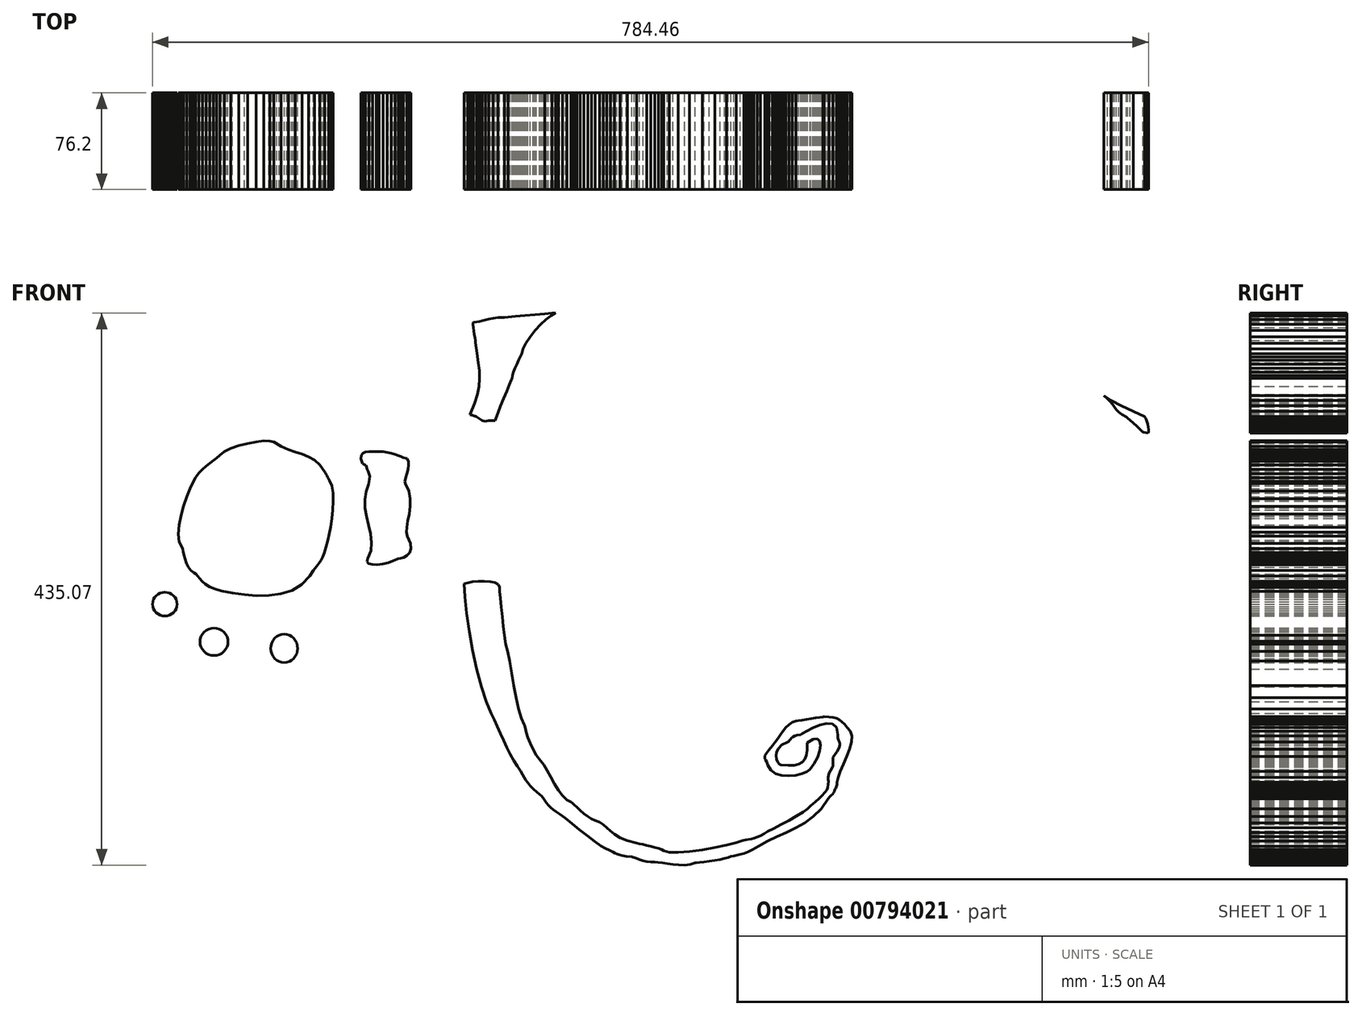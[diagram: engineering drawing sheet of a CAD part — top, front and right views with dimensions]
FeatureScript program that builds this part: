
annotation { "Feature Type Name" : "Feature", "Feature Type Description" : "" }
export const myFeature = defineFeature(function(context is Context, id is Id, definition is map)
    precondition{}
    {
        {
            var Q0;
            Q0=qCreatedBy(makeId("Front.planeOp"),FACE);
            var sketch = newSketch(context, id + "F0", { "sketchPlane" : qUnion([Q0])});
            skLineSegment(sketch, "E0", {"start": v(-208.35, -37.14) * mm, "end": v(-209.4, -40.75) * mm});
            skLineSegment(sketch, "E1", {"start": v(-209.4, -40.75) * mm, "end": v(-211.93, -45.37) * mm});
            skLineSegment(sketch, "E2", {"start": v(-211.93, -45.37) * mm, "end": v(-215.55, -50.61) * mm});
            skLineSegment(sketch, "E3", {"start": v(-215.55, -50.61) * mm, "end": v(-219.86, -56.1) * mm});
            skLineSegment(sketch, "E4", {"start": v(-219.86, -56.1) * mm, "end": v(-224.45, -61.4) * mm});
            skLineSegment(sketch, "E5", {"start": v(-224.45, -61.4) * mm, "end": v(-228.92, -66.17) * mm});
            skLineSegment(sketch, "E6", {"start": v(-228.92, -66.17) * mm, "end": v(-232.89, -69.99) * mm});
            skLineSegment(sketch, "E7", {"start": v(-232.89, -69.99) * mm, "end": v(-235.95, -72.46) * mm});
            skLineSegment(sketch, "E8", {"start": v(-235.95, -72.46) * mm, "end": v(-243.86, -77.98) * mm});
            skLineSegment(sketch, "E9", {"start": v(-243.86, -77.98) * mm, "end": v(-251.56, -83.5) * mm});
            skLineSegment(sketch, "E10", {"start": v(-251.56, -83.5) * mm, "end": v(-259.2, -88.85) * mm});
            skLineSegment(sketch, "E11", {"start": v(-259.2, -88.85) * mm, "end": v(-266.91, -93.92) * mm});
            skLineSegment(sketch, "E12", {"start": v(-266.91, -93.92) * mm, "end": v(-274.89, -98.55) * mm});
            skLineSegment(sketch, "E13", {"start": v(-274.89, -98.55) * mm, "end": v(-283.27, -102.63) * mm});
            skLineSegment(sketch, "E14", {"start": v(-283.27, -102.63) * mm, "end": v(-292.21, -106) * mm});
            skLineSegment(sketch, "E15", {"start": v(-292.21, -106) * mm, "end": v(-301.88, -108.52) * mm});
            skLineSegment(sketch, "E16", {"start": v(-301.88, -108.52) * mm, "end": v(-307.2, -109.6) * mm});
            skLineSegment(sketch, "E17", {"start": v(-307.2, -109.6) * mm, "end": v(-312.55, -110.63) * mm});
            skLineSegment(sketch, "E18", {"start": v(-312.55, -110.63) * mm, "end": v(-317.94, -111.58) * mm});
            skLineSegment(sketch, "E19", {"start": v(-317.94, -111.58) * mm, "end": v(-323.38, -112.42) * mm});
            skLineSegment(sketch, "E20", {"start": v(-323.38, -112.42) * mm, "end": v(-328.86, -113.1) * mm});
            skLineSegment(sketch, "E21", {"start": v(-328.86, -113.1) * mm, "end": v(-334.38, -113.56) * mm});
            skLineSegment(sketch, "E22", {"start": v(-334.38, -113.56) * mm, "end": v(-339.94, -113.79) * mm});
            skLineSegment(sketch, "E23", {"start": v(-339.94, -113.79) * mm, "end": v(-345.54, -113.72) * mm});
            skLineSegment(sketch, "E24", {"start": v(-345.54, -113.72) * mm, "end": v(-350.27, -113.48) * mm});
            skLineSegment(sketch, "E25", {"start": v(-350.27, -113.48) * mm, "end": v(-353.56, -113.18) * mm});
            skLineSegment(sketch, "E26", {"start": v(-353.56, -113.18) * mm, "end": v(-355.78, -112.84) * mm});
            skLineSegment(sketch, "E27", {"start": v(-355.78, -112.84) * mm, "end": v(-357.32, -112.47) * mm});
            skLineSegment(sketch, "E28", {"start": v(-357.32, -112.47) * mm, "end": v(-358.56, -112.08) * mm});
            skLineSegment(sketch, "E29", {"start": v(-358.56, -112.08) * mm, "end": v(-359.89, -111.67) * mm});
            skLineSegment(sketch, "E30", {"start": v(-359.89, -111.67) * mm, "end": v(-361.68, -111.27) * mm});
            skLineSegment(sketch, "E31", {"start": v(-361.68, -111.27) * mm, "end": v(-364.33, -110.87) * mm});
            skLineSegment(sketch, "E32", {"start": v(-364.33, -110.87) * mm, "end": v(-370.95, -109.7) * mm});
            skLineSegment(sketch, "E33", {"start": v(-370.95, -109.7) * mm, "end": v(-378.12, -107.85) * mm});
            skLineSegment(sketch, "E34", {"start": v(-378.12, -107.85) * mm, "end": v(-385.58, -105.38) * mm});
            skLineSegment(sketch, "E35", {"start": v(-385.58, -105.38) * mm, "end": v(-393.1, -102.4) * mm});
            skLineSegment(sketch, "E36", {"start": v(-393.1, -102.4) * mm, "end": v(-400.45, -99.03) * mm});
            skLineSegment(sketch, "E37", {"start": v(-400.45, -99.03) * mm, "end": v(-407.36, -95.36) * mm});
            skLineSegment(sketch, "E38", {"start": v(-407.36, -95.36) * mm, "end": v(-413.61, -91.48) * mm});
            skLineSegment(sketch, "E39", {"start": v(-413.61, -91.48) * mm, "end": v(-418.95, -87.5) * mm});
            skLineSegment(sketch, "E40", {"start": v(-418.95, -87.5) * mm, "end": v(-420.34, -86.72) * mm});
            skLineSegment(sketch, "E41", {"start": v(-420.34, -86.72) * mm, "end": v(-421.81, -86.45) * mm});
            skLineSegment(sketch, "E42", {"start": v(-421.81, -86.45) * mm, "end": v(-423.56, -86.22) * mm});
            skLineSegment(sketch, "E43", {"start": v(-423.56, -86.22) * mm, "end": v(-425.77, -85.58) * mm});
            skLineSegment(sketch, "E44", {"start": v(-425.77, -85.58) * mm, "end": v(-428.66, -84.05) * mm});
            skLineSegment(sketch, "E45", {"start": v(-428.66, -84.05) * mm, "end": v(-432.42, -81.17) * mm});
            skLineSegment(sketch, "E46", {"start": v(-432.42, -81.17) * mm, "end": v(-437.25, -76.48) * mm});
            skLineSegment(sketch, "E47", {"start": v(-437.25, -76.48) * mm, "end": v(-443.34, -69.52) * mm});
            skLineSegment(sketch, "E48", {"start": v(-443.34, -69.52) * mm, "end": v(-446.37, -65.99) * mm});
            skLineSegment(sketch, "E49", {"start": v(-446.37, -65.99) * mm, "end": v(-449.48, -62.55) * mm});
            skLineSegment(sketch, "E50", {"start": v(-449.48, -62.55) * mm, "end": v(-452.63, -59.14) * mm});
            skLineSegment(sketch, "E51", {"start": v(-452.63, -59.14) * mm, "end": v(-455.78, -55.7) * mm});
            skLineSegment(sketch, "E52", {"start": v(-455.78, -55.7) * mm, "end": v(-458.87, -52.18) * mm});
            skLineSegment(sketch, "E53", {"start": v(-458.87, -52.18) * mm, "end": v(-461.86, -48.5) * mm});
            skLineSegment(sketch, "E54", {"start": v(-461.86, -48.5) * mm, "end": v(-464.7, -44.6) * mm});
            skLineSegment(sketch, "E55", {"start": v(-464.7, -44.6) * mm, "end": v(-467.34, -40.43) * mm});
            skLineSegment(sketch, "E56", {"start": v(-467.34, -40.43) * mm, "end": v(-471.05, -34.4) * mm});
            skLineSegment(sketch, "E57", {"start": v(-471.05, -34.4) * mm, "end": v(-474.16, -29.72) * mm});
            skLineSegment(sketch, "E58", {"start": v(-474.16, -29.72) * mm, "end": v(-476.73, -25.85) * mm});
            skLineSegment(sketch, "E59", {"start": v(-476.73, -25.85) * mm, "end": v(-478.83, -22.2) * mm});
            skLineSegment(sketch, "E60", {"start": v(-478.83, -22.2) * mm, "end": v(-480.55, -18.2) * mm});
            skLineSegment(sketch, "E61", {"start": v(-480.55, -18.2) * mm, "end": v(-481.95, -13.26) * mm});
            skLineSegment(sketch, "E62", {"start": v(-481.95, -13.26) * mm, "end": v(-483.1, -6.8) * mm});
            skLineSegment(sketch, "E63", {"start": v(-483.1, -6.8) * mm, "end": v(-484.1, 1.73) * mm});
            skLineSegment(sketch, "E64", {"start": v(-484.1, 1.73) * mm, "end": v(-484.63, 4.71) * mm});
            skLineSegment(sketch, "E65", {"start": v(-484.63, 4.71) * mm, "end": v(-485.63, 8.34) * mm});
            skLineSegment(sketch, "E66", {"start": v(-485.63, 8.34) * mm, "end": v(-486.93, 12.53) * mm});
            skLineSegment(sketch, "E67", {"start": v(-486.93, 12.53) * mm, "end": v(-488.36, 17.21) * mm});
            skLineSegment(sketch, "E68", {"start": v(-488.36, 17.21) * mm, "end": v(-489.76, 22.29) * mm});
            skLineSegment(sketch, "E69", {"start": v(-489.76, 22.29) * mm, "end": v(-490.96, 27.69) * mm});
            skLineSegment(sketch, "E70", {"start": v(-490.96, 27.69) * mm, "end": v(-491.8, 33.33) * mm});
            skLineSegment(sketch, "E71", {"start": v(-491.8, 33.33) * mm, "end": v(-492.12, 39.13) * mm});
            skLineSegment(sketch, "E72", {"start": v(-492.12, 39.13) * mm, "end": v(-492.1, 43.83) * mm});
            skLineSegment(sketch, "E73", {"start": v(-492.1, 43.83) * mm, "end": v(-491.96, 49.13) * mm});
            skLineSegment(sketch, "E74", {"start": v(-491.96, 49.13) * mm, "end": v(-491.67, 54.8) * mm});
            skLineSegment(sketch, "E75", {"start": v(-491.67, 54.8) * mm, "end": v(-491.16, 60.58) * mm});
            skLineSegment(sketch, "E76", {"start": v(-491.16, 60.58) * mm, "end": v(-490.37, 66.27) * mm});
            skLineSegment(sketch, "E77", {"start": v(-490.37, 66.27) * mm, "end": v(-489.23, 71.63) * mm});
            skLineSegment(sketch, "E78", {"start": v(-489.23, 71.63) * mm, "end": v(-487.68, 76.43) * mm});
            skLineSegment(sketch, "E79", {"start": v(-487.68, 76.43) * mm, "end": v(-485.66, 80.43) * mm});
            skLineSegment(sketch, "E80", {"start": v(-485.66, 80.43) * mm, "end": v(-484, 84.07) * mm});
            skLineSegment(sketch, "E81", {"start": v(-484, 84.07) * mm, "end": v(-482.62, 88.9) * mm});
            skLineSegment(sketch, "E82", {"start": v(-482.62, 88.9) * mm, "end": v(-481.28, 94.53) * mm});
            skLineSegment(sketch, "E83", {"start": v(-481.28, 94.53) * mm, "end": v(-479.78, 100.6) * mm});
            skLineSegment(sketch, "E84", {"start": v(-479.78, 100.6) * mm, "end": v(-477.88, 106.75) * mm});
            skLineSegment(sketch, "E85", {"start": v(-477.88, 106.75) * mm, "end": v(-475.38, 112.57) * mm});
            skLineSegment(sketch, "E86", {"start": v(-475.38, 112.57) * mm, "end": v(-472.04, 117.7) * mm});
            skLineSegment(sketch, "E87", {"start": v(-472.04, 117.7) * mm, "end": v(-467.65, 121.78) * mm});
            skLineSegment(sketch, "E88", {"start": v(-467.65, 121.78) * mm, "end": v(-466.26, 123.27) * mm});
            skLineSegment(sketch, "E89", {"start": v(-466.26, 123.27) * mm, "end": v(-464.7, 125.77) * mm});
            skLineSegment(sketch, "E90", {"start": v(-464.7, 125.77) * mm, "end": v(-462.86, 129.05) * mm});
            skLineSegment(sketch, "E91", {"start": v(-462.86, 129.05) * mm, "end": v(-460.63, 132.87) * mm});
            skLineSegment(sketch, "E92", {"start": v(-460.63, 132.87) * mm, "end": v(-457.91, 137.02) * mm});
            skLineSegment(sketch, "E93", {"start": v(-457.91, 137.02) * mm, "end": v(-454.6, 141.25) * mm});
            skLineSegment(sketch, "E94", {"start": v(-454.6, 141.25) * mm, "end": v(-450.57, 145.34) * mm});
            skLineSegment(sketch, "E95", {"start": v(-450.57, 145.34) * mm, "end": v(-445.73, 149.07) * mm});
            skLineSegment(sketch, "E96", {"start": v(-445.73, 149.07) * mm, "end": v(-442.4, 151.6) * mm});
            skLineSegment(sketch, "E97", {"start": v(-442.4, 151.6) * mm, "end": v(-438.2, 155.26) * mm});
            skLineSegment(sketch, "E98", {"start": v(-438.2, 155.26) * mm, "end": v(-433.33, 159.6) * mm});
            skLineSegment(sketch, "E99", {"start": v(-433.33, 159.6) * mm, "end": v(-428.08, 164.2) * mm});
            skLineSegment(sketch, "E100", {"start": v(-428.08, 164.2) * mm, "end": v(-422.67, 168.63) * mm});
            skLineSegment(sketch, "E101", {"start": v(-422.67, 168.63) * mm, "end": v(-417.35, 172.46) * mm});
            skLineSegment(sketch, "E102", {"start": v(-417.35, 172.46) * mm, "end": v(-412.37, 175.25) * mm});
            skLineSegment(sketch, "E103", {"start": v(-412.37, 175.25) * mm, "end": v(-407.98, 176.59) * mm});
            skLineSegment(sketch, "E104", {"start": v(-407.98, 176.59) * mm, "end": v(-407.04, 176.9) * mm});
            skLineSegment(sketch, "E105", {"start": v(-407.04, 176.9) * mm, "end": v(-405.7, 177.63) * mm});
            skLineSegment(sketch, "E106", {"start": v(-405.7, 177.63) * mm, "end": v(-404.1, 178.65) * mm});
            skLineSegment(sketch, "E107", {"start": v(-404.1, 178.65) * mm, "end": v(-402.42, 179.84) * mm});
            skLineSegment(sketch, "E108", {"start": v(-402.42, 179.84) * mm, "end": v(-400.79, 181.1) * mm});
            skLineSegment(sketch, "E109", {"start": v(-400.79, 181.1) * mm, "end": v(-399.35, 182.32) * mm});
            skLineSegment(sketch, "E110", {"start": v(-399.35, 182.32) * mm, "end": v(-398.27, 183.37) * mm});
            skLineSegment(sketch, "E111", {"start": v(-398.27, 183.37) * mm, "end": v(-397.69, 184.15) * mm});
            skLineSegment(sketch, "E112", {"start": v(-397.69, 184.15) * mm, "end": v(-397.28, 184.12) * mm});
            skLineSegment(sketch, "E113", {"start": v(-397.28, 184.12) * mm, "end": v(-396.96, 184.1) * mm});
            skLineSegment(sketch, "E114", {"start": v(-396.96, 184.1) * mm, "end": v(-396.82, 184.1) * mm});
            skLineSegment(sketch, "E115", {"start": v(-396.82, 184.1) * mm, "end": v(-396.68, 184.13) * mm});
            skLineSegment(sketch, "E116", {"start": v(-396.68, 184.13) * mm, "end": v(-396.54, 184.18) * mm});
            skLineSegment(sketch, "E117", {"start": v(-396.54, 184.18) * mm, "end": v(-396.4, 184.27) * mm});
            skLineSegment(sketch, "E118", {"start": v(-396.4, 184.27) * mm, "end": v(-392.15, 186.6) * mm});
            skLineSegment(sketch, "E119", {"start": v(-392.15, 186.6) * mm, "end": v(-387.6, 188.05) * mm});
            skLineSegment(sketch, "E120", {"start": v(-387.6, 188.05) * mm, "end": v(-382.84, 188.9) * mm});
            skLineSegment(sketch, "E121", {"start": v(-382.84, 188.9) * mm, "end": v(-378, 189.41) * mm});
            skLineSegment(sketch, "E122", {"start": v(-378, 189.41) * mm, "end": v(-373.21, 189.91) * mm});
            skLineSegment(sketch, "E123", {"start": v(-373.21, 189.91) * mm, "end": v(-368.57, 190.67) * mm});
            skLineSegment(sketch, "E124", {"start": v(-368.57, 190.67) * mm, "end": v(-364.2, 191.98) * mm});
            skLineSegment(sketch, "E125", {"start": v(-364.2, 191.98) * mm, "end": v(-360.22, 194.13) * mm});
            skLineSegment(sketch, "E126", {"start": v(-360.22, 194.13) * mm, "end": v(-357.32, 195.4) * mm});
            skLineSegment(sketch, "E127", {"start": v(-357.32, 195.4) * mm, "end": v(-353.37, 196.1) * mm});
            skLineSegment(sketch, "E128", {"start": v(-353.37, 196.1) * mm, "end": v(-348.73, 196.36) * mm});
            skLineSegment(sketch, "E129", {"start": v(-348.73, 196.36) * mm, "end": v(-343.75, 196.3) * mm});
            skLineSegment(sketch, "E130", {"start": v(-343.75, 196.3) * mm, "end": v(-338.8, 196.04) * mm});
            skLineSegment(sketch, "E131", {"start": v(-338.8, 196.04) * mm, "end": v(-334.23, 195.72) * mm});
            skLineSegment(sketch, "E132", {"start": v(-334.23, 195.72) * mm, "end": v(-330.4, 195.47) * mm});
            skLineSegment(sketch, "E133", {"start": v(-330.4, 195.47) * mm, "end": v(-327.68, 195.42) * mm});
            skLineSegment(sketch, "E134", {"start": v(-327.68, 195.42) * mm, "end": v(-322.8, 195.26) * mm});
            skLineSegment(sketch, "E135", {"start": v(-322.8, 195.26) * mm, "end": v(-317.16, 194.53) * mm});
            skLineSegment(sketch, "E136", {"start": v(-317.16, 194.53) * mm, "end": v(-311.19, 193.4) * mm});
            skLineSegment(sketch, "E137", {"start": v(-311.19, 193.4) * mm, "end": v(-305.32, 192.08) * mm});
            skLineSegment(sketch, "E138", {"start": v(-305.32, 192.08) * mm, "end": v(-299.98, 190.73) * mm});
            skLineSegment(sketch, "E139", {"start": v(-299.98, 190.73) * mm, "end": v(-295.6, 189.54) * mm});
            skLineSegment(sketch, "E140", {"start": v(-295.6, 189.54) * mm, "end": v(-292.64, 188.7) * mm});
            skLineSegment(sketch, "E141", {"start": v(-292.64, 188.7) * mm, "end": v(-291.5, 188.37) * mm});
            skLineSegment(sketch, "E142", {"start": v(-291.5, 188.37) * mm, "end": v(-288.2, 188.12) * mm});
            skLineSegment(sketch, "E143", {"start": v(-288.2, 188.12) * mm, "end": v(-284.6, 187.19) * mm});
            skLineSegment(sketch, "E144", {"start": v(-284.6, 187.19) * mm, "end": v(-280.81, 185.77) * mm});
            skLineSegment(sketch, "E145", {"start": v(-280.81, 185.77) * mm, "end": v(-276.94, 184.04) * mm});
            skLineSegment(sketch, "E146", {"start": v(-276.94, 184.04) * mm, "end": v(-273.1, 182.17) * mm});
            skLineSegment(sketch, "E147", {"start": v(-273.1, 182.17) * mm, "end": v(-269.41, 180.34) * mm});
            skLineSegment(sketch, "E148", {"start": v(-269.41, 180.34) * mm, "end": v(-265.98, 178.72) * mm});
            skLineSegment(sketch, "E149", {"start": v(-265.98, 178.72) * mm, "end": v(-262.93, 177.49) * mm});
            skLineSegment(sketch, "E150", {"start": v(-262.93, 177.49) * mm, "end": v(-262.03, 176.24) * mm});
            skLineSegment(sketch, "E151", {"start": v(-262.03, 176.24) * mm, "end": v(-259.93, 174.4) * mm});
            skLineSegment(sketch, "E152", {"start": v(-259.93, 174.4) * mm, "end": v(-257, 172.17) * mm});
            skLineSegment(sketch, "E153", {"start": v(-257, 172.17) * mm, "end": v(-253.61, 169.8) * mm});
            skLineSegment(sketch, "E154", {"start": v(-253.61, 169.8) * mm, "end": v(-250.12, 167.5) * mm});
            skLineSegment(sketch, "E155", {"start": v(-250.12, 167.5) * mm, "end": v(-246.89, 165.53) * mm});
            skLineSegment(sketch, "E156", {"start": v(-246.89, 165.53) * mm, "end": v(-244.29, 164.1) * mm});
            skLineSegment(sketch, "E157", {"start": v(-244.29, 164.1) * mm, "end": v(-242.68, 163.43) * mm});
            skLineSegment(sketch, "E158", {"start": v(-242.68, 163.43) * mm, "end": v(-239.6, 161.8) * mm});
            skLineSegment(sketch, "E159", {"start": v(-239.6, 161.8) * mm, "end": v(-235.25, 158.26) * mm});
            skLineSegment(sketch, "E160", {"start": v(-235.25, 158.26) * mm, "end": v(-230.13, 153.46) * mm});
            skLineSegment(sketch, "E161", {"start": v(-230.13, 153.46) * mm, "end": v(-224.7, 148.03) * mm});
            skLineSegment(sketch, "E162", {"start": v(-224.7, 148.03) * mm, "end": v(-219.48, 142.62) * mm});
            skLineSegment(sketch, "E163", {"start": v(-219.48, 142.62) * mm, "end": v(-214.92, 137.88) * mm});
            skLineSegment(sketch, "E164", {"start": v(-214.92, 137.88) * mm, "end": v(-211.52, 134.43) * mm});
            skLineSegment(sketch, "E165", {"start": v(-211.52, 134.43) * mm, "end": v(-209.76, 132.93) * mm});
            skLineSegment(sketch, "E166", {"start": v(-209.76, 132.93) * mm, "end": v(-206.84, 132.26) * mm});
            skLineSegment(sketch, "E167", {"start": v(-206.84, 132.26) * mm, "end": v(-204.6, 133.15) * mm});
            skLineSegment(sketch, "E168", {"start": v(-204.6, 133.15) * mm, "end": v(-202.9, 135.25) * mm});
            skLineSegment(sketch, "E169", {"start": v(-202.9, 135.25) * mm, "end": v(-201.58, 138.19) * mm});
            skLineSegment(sketch, "E170", {"start": v(-201.58, 138.19) * mm, "end": v(-200.52, 141.61) * mm});
            skLineSegment(sketch, "E171", {"start": v(-200.52, 141.61) * mm, "end": v(-199.56, 145.17) * mm});
            skLineSegment(sketch, "E172", {"start": v(-199.56, 145.17) * mm, "end": v(-198.56, 148.5) * mm});
            skLineSegment(sketch, "E173", {"start": v(-198.56, 148.5) * mm, "end": v(-197.38, 151.26) * mm});
            skLineSegment(sketch, "E174", {"start": v(-197.38, 151.26) * mm, "end": v(-195.83, 155.22) * mm});
            skLineSegment(sketch, "E175", {"start": v(-195.83, 155.22) * mm, "end": v(-194.87, 160.31) * mm});
            skLineSegment(sketch, "E176", {"start": v(-194.87, 160.31) * mm, "end": v(-194.47, 166.12) * mm});
            skLineSegment(sketch, "E177", {"start": v(-194.47, 166.12) * mm, "end": v(-194.63, 172.25) * mm});
            skLineSegment(sketch, "E178", {"start": v(-194.63, 172.25) * mm, "end": v(-195.34, 178.29) * mm});
            skLineSegment(sketch, "E179", {"start": v(-195.34, 178.29) * mm, "end": v(-196.59, 183.83) * mm});
            skLineSegment(sketch, "E180", {"start": v(-196.59, 183.83) * mm, "end": v(-198.37, 188.48) * mm});
            skLineSegment(sketch, "E181", {"start": v(-198.37, 188.48) * mm, "end": v(-200.67, 191.82) * mm});
            skLineSegment(sketch, "E182", {"start": v(-200.67, 191.82) * mm, "end": v(-203.2, 194.14) * mm});
            skLineSegment(sketch, "E183", {"start": v(-203.2, 194.14) * mm, "end": v(-206.46, 196.97) * mm});
            skLineSegment(sketch, "E184", {"start": v(-206.46, 196.97) * mm, "end": v(-209.95, 200.1) * mm});
            skLineSegment(sketch, "E185", {"start": v(-209.95, 200.1) * mm, "end": v(-213.15, 203.36) * mm});
            skLineSegment(sketch, "E186", {"start": v(-213.15, 203.36) * mm, "end": v(-215.57, 206.55) * mm});
            skLineSegment(sketch, "E187", {"start": v(-215.57, 206.55) * mm, "end": v(-216.7, 209.49) * mm});
            skLineSegment(sketch, "E188", {"start": v(-216.7, 209.49) * mm, "end": v(-216.06, 211.97) * mm});
            skLineSegment(sketch, "E189", {"start": v(-216.06, 211.97) * mm, "end": v(-213.12, 213.83) * mm});
            skLineSegment(sketch, "E190", {"start": v(-213.12, 213.83) * mm, "end": v(-209.96, 215.34) * mm});
            skLineSegment(sketch, "E191", {"start": v(-209.96, 215.34) * mm, "end": v(-202.14, 216.57) * mm});
            skLineSegment(sketch, "E192", {"start": v(-202.14, 216.57) * mm, "end": v(-191.16, 217.6) * mm});
            skLineSegment(sketch, "E193", {"start": v(-191.16, 217.6) * mm, "end": v(-178.53, 218.51) * mm});
            skLineSegment(sketch, "E194", {"start": v(-178.53, 218.51) * mm, "end": v(-165.72, 219.37) * mm});
            skLineSegment(sketch, "E195", {"start": v(-165.72, 219.37) * mm, "end": v(-154.22, 220.26) * mm});
            skLineSegment(sketch, "E196", {"start": v(-154.22, 220.26) * mm, "end": v(-145.54, 221.25) * mm});
            skLineSegment(sketch, "E197", {"start": v(-145.54, 221.25) * mm, "end": v(-141.16, 222.43) * mm});
            skLineSegment(sketch, "E198", {"start": v(-141.16, 222.43) * mm, "end": v(-137.78, 223.77) * mm});
            skLineSegment(sketch, "E199", {"start": v(-137.78, 223.77) * mm, "end": v(-131.88, 224.98) * mm});
            skLineSegment(sketch, "E200", {"start": v(-131.88, 224.98) * mm, "end": v(-124.22, 226.12) * mm});
            skLineSegment(sketch, "E201", {"start": v(-124.22, 226.12) * mm, "end": v(-115.53, 227.22) * mm});
            skLineSegment(sketch, "E202", {"start": v(-115.53, 227.22) * mm, "end": v(-106.55, 228.34) * mm});
            skLineSegment(sketch, "E203", {"start": v(-106.55, 228.34) * mm, "end": v(-98.01, 229.5) * mm});
            skLineSegment(sketch, "E204", {"start": v(-98.01, 229.5) * mm, "end": v(-90.67, 230.78) * mm});
            skLineSegment(sketch, "E205", {"start": v(-90.67, 230.78) * mm, "end": v(-85.25, 232.19) * mm});
            skLineSegment(sketch, "E206", {"start": v(-85.25, 232.19) * mm, "end": v(-81.66, 233.2) * mm});
            skLineSegment(sketch, "E207", {"start": v(-81.66, 233.2) * mm, "end": v(-75.46, 234.69) * mm});
            skLineSegment(sketch, "E208", {"start": v(-75.46, 234.69) * mm, "end": v(-67.62, 236.36) * mm});
            skLineSegment(sketch, "E209", {"start": v(-67.62, 236.36) * mm, "end": v(-59.07, 237.98) * mm});
            skLineSegment(sketch, "E210", {"start": v(-59.07, 237.98) * mm, "end": v(-50.78, 239.28) * mm});
            skLineSegment(sketch, "E211", {"start": v(-50.78, 239.28) * mm, "end": v(-43.68, 240) * mm});
            skLineSegment(sketch, "E212", {"start": v(-43.68, 240) * mm, "end": v(-38.72, 239.87) * mm});
            skLineSegment(sketch, "E213", {"start": v(-38.72, 239.87) * mm, "end": v(-36.86, 238.65) * mm});
            skLineSegment(sketch, "E214", {"start": v(-36.86, 238.65) * mm, "end": v(-37.05, 235.1) * mm});
            skLineSegment(sketch, "E215", {"start": v(-37.05, 235.1) * mm, "end": v(-37.65, 232.95) * mm});
            skLineSegment(sketch, "E216", {"start": v(-37.65, 232.95) * mm, "end": v(-38.68, 231.73) * mm});
            skLineSegment(sketch, "E217", {"start": v(-38.68, 231.73) * mm, "end": v(-40.17, 231) * mm});
            skLineSegment(sketch, "E218", {"start": v(-40.17, 231) * mm, "end": v(-42.15, 230.3) * mm});
            skLineSegment(sketch, "E219", {"start": v(-42.15, 230.3) * mm, "end": v(-44.64, 229.2) * mm});
            skLineSegment(sketch, "E220", {"start": v(-44.64, 229.2) * mm, "end": v(-47.67, 227.21) * mm});
            skLineSegment(sketch, "E221", {"start": v(-47.67, 227.21) * mm, "end": v(-51.26, 223.92) * mm});
            skLineSegment(sketch, "E222", {"start": v(-51.26, 223.92) * mm, "end": v(-55.17, 220.71) * mm});
            skLineSegment(sketch, "E223", {"start": v(-55.17, 220.71) * mm, "end": v(-60.25, 217.76) * mm});
            skLineSegment(sketch, "E224", {"start": v(-60.25, 217.76) * mm, "end": v(-66.1, 215) * mm});
            skLineSegment(sketch, "E225", {"start": v(-66.1, 215) * mm, "end": v(-72.28, 212.33) * mm});
            skLineSegment(sketch, "E226", {"start": v(-72.28, 212.33) * mm, "end": v(-78.42, 209.7) * mm});
            skLineSegment(sketch, "E227", {"start": v(-78.42, 209.7) * mm, "end": v(-84.1, 207.01) * mm});
            skLineSegment(sketch, "E228", {"start": v(-84.1, 207.01) * mm, "end": v(-88.9, 204.2) * mm});
            skLineSegment(sketch, "E229", {"start": v(-88.9, 204.2) * mm, "end": v(-92.42, 201.18) * mm});
            skLineSegment(sketch, "E230", {"start": v(-92.42, 201.18) * mm, "end": v(-95.18, 198.51) * mm});
            skLineSegment(sketch, "E231", {"start": v(-95.18, 198.51) * mm, "end": v(-98.28, 196.21) * mm});
            skLineSegment(sketch, "E232", {"start": v(-98.28, 196.21) * mm, "end": v(-101.68, 194) * mm});
            skLineSegment(sketch, "E233", {"start": v(-101.68, 194) * mm, "end": v(-105.31, 191.64) * mm});
            skLineSegment(sketch, "E234", {"start": v(-105.31, 191.64) * mm, "end": v(-109.12, 188.84) * mm});
            skLineSegment(sketch, "E235", {"start": v(-109.12, 188.84) * mm, "end": v(-113.06, 185.34) * mm});
            skLineSegment(sketch, "E236", {"start": v(-113.06, 185.34) * mm, "end": v(-117.06, 180.9) * mm});
            skLineSegment(sketch, "E237", {"start": v(-117.06, 180.9) * mm, "end": v(-121.08, 175.22) * mm});
            skLineSegment(sketch, "E238", {"start": v(-121.08, 175.22) * mm, "end": v(-123.48, 171.6) * mm});
            skLineSegment(sketch, "E239", {"start": v(-123.48, 171.6) * mm, "end": v(-125.98, 168.05) * mm});
            skLineSegment(sketch, "E240", {"start": v(-125.98, 168.05) * mm, "end": v(-128.46, 164.5) * mm});
            skLineSegment(sketch, "E241", {"start": v(-128.46, 164.5) * mm, "end": v(-130.82, 160.87) * mm});
            skLineSegment(sketch, "E242", {"start": v(-130.82, 160.87) * mm, "end": v(-132.96, 157.05) * mm});
            skLineSegment(sketch, "E243", {"start": v(-132.96, 157.05) * mm, "end": v(-134.75, 152.98) * mm});
            skLineSegment(sketch, "E244", {"start": v(-134.75, 152.98) * mm, "end": v(-136.1, 148.55) * mm});
            skLineSegment(sketch, "E245", {"start": v(-136.1, 148.55) * mm, "end": v(-136.9, 143.7) * mm});
            skLineSegment(sketch, "E246", {"start": v(-136.9, 143.7) * mm, "end": v(-137.12, 143.45) * mm});
            skLineSegment(sketch, "E247", {"start": v(-137.12, 143.45) * mm, "end": v(-137.73, 142.78) * mm});
            skLineSegment(sketch, "E248", {"start": v(-137.73, 142.78) * mm, "end": v(-138.58, 141.78) * mm});
            skLineSegment(sketch, "E249", {"start": v(-138.58, 141.78) * mm, "end": v(-139.56, 140.5) * mm});
            skLineSegment(sketch, "E250", {"start": v(-139.56, 140.5) * mm, "end": v(-140.52, 139.05) * mm});
            skLineSegment(sketch, "E251", {"start": v(-140.52, 139.05) * mm, "end": v(-141.35, 137.5) * mm});
            skLineSegment(sketch, "E252", {"start": v(-141.35, 137.5) * mm, "end": v(-141.92, 135.9) * mm});
            skLineSegment(sketch, "E253", {"start": v(-141.92, 135.9) * mm, "end": v(-142.1, 134.34) * mm});
            skLineSegment(sketch, "E254", {"start": v(-142.1, 134.34) * mm, "end": v(-142.36, 130.26) * mm});
            skLineSegment(sketch, "E255", {"start": v(-142.36, 130.26) * mm, "end": v(-143.18, 126.12) * mm});
            skLineSegment(sketch, "E256", {"start": v(-143.18, 126.12) * mm, "end": v(-144.16, 122) * mm});
            skLineSegment(sketch, "E257", {"start": v(-144.16, 122) * mm, "end": v(-144.93, 117.97) * mm});
            skLineSegment(sketch, "E258", {"start": v(-144.93, 117.97) * mm, "end": v(-145.07, 114.13) * mm});
            skLineSegment(sketch, "E259", {"start": v(-145.07, 114.13) * mm, "end": v(-144.2, 110.53) * mm});
            skLineSegment(sketch, "E260", {"start": v(-144.2, 110.53) * mm, "end": v(-141.92, 107.28) * mm});
            skLineSegment(sketch, "E261", {"start": v(-141.92, 107.28) * mm, "end": v(-137.83, 104.44) * mm});
            skLineSegment(sketch, "E262", {"start": v(-137.83, 104.44) * mm, "end": v(-137.13, 103.9) * mm});
            skLineSegment(sketch, "E263", {"start": v(-137.13, 103.9) * mm, "end": v(-136.78, 103.32) * mm});
            skLineSegment(sketch, "E264", {"start": v(-136.78, 103.32) * mm, "end": v(-136.48, 102.66) * mm});
            skLineSegment(sketch, "E265", {"start": v(-136.48, 102.66) * mm, "end": v(-135.93, 101.93) * mm});
            skLineSegment(sketch, "E266", {"start": v(-135.93, 101.93) * mm, "end": v(-134.82, 101.12) * mm});
            skLineSegment(sketch, "E267", {"start": v(-134.82, 101.12) * mm, "end": v(-132.85, 100.24) * mm});
            skLineSegment(sketch, "E268", {"start": v(-132.85, 100.24) * mm, "end": v(-129.73, 99.27) * mm});
            skLineSegment(sketch, "E269", {"start": v(-129.73, 99.27) * mm, "end": v(-125.15, 98.2) * mm});
            skLineSegment(sketch, "E270", {"start": v(-125.15, 98.2) * mm, "end": v(-124.24, 98.04) * mm});
            skLineSegment(sketch, "E271", {"start": v(-124.24, 98.04) * mm, "end": v(-122.97, 97.84) * mm});
            skLineSegment(sketch, "E272", {"start": v(-122.97, 97.84) * mm, "end": v(-121.5, 97.62) * mm});
            skLineSegment(sketch, "E273", {"start": v(-121.5, 97.62) * mm, "end": v(-119.96, 97.39) * mm});
            skLineSegment(sketch, "E274", {"start": v(-119.96, 97.39) * mm, "end": v(-118.47, 97.17) * mm});
            skLineSegment(sketch, "E275", {"start": v(-118.47, 97.17) * mm, "end": v(-117.2, 96.98) * mm});
            skLineSegment(sketch, "E276", {"start": v(-117.2, 96.98) * mm, "end": v(-116.25, 96.84) * mm});
            skLineSegment(sketch, "E277", {"start": v(-116.25, 96.84) * mm, "end": v(-115.79, 96.76) * mm});
            skLineSegment(sketch, "E278", {"start": v(-182.98, 129.65) * mm, "end": v(-179.53, 137.98) * mm});
            skLineSegment(sketch, "E279", {"start": v(-179.53, 137.98) * mm, "end": v(-177.27, 145.15) * mm});
            skLineSegment(sketch, "E280", {"start": v(-177.27, 145.15) * mm, "end": v(-176.03, 151.55) * mm});
            skLineSegment(sketch, "E281", {"start": v(-176.03, 151.55) * mm, "end": v(-175.63, 157.58) * mm});
            skLineSegment(sketch, "E282", {"start": v(-175.63, 157.58) * mm, "end": v(-175.88, 163.64) * mm});
            skLineSegment(sketch, "E283", {"start": v(-175.88, 163.64) * mm, "end": v(-176.61, 170.13) * mm});
            skLineSegment(sketch, "E284", {"start": v(-176.61, 170.13) * mm, "end": v(-177.64, 177.46) * mm});
            skLineSegment(sketch, "E285", {"start": v(-177.64, 177.46) * mm, "end": v(-178.79, 186.02) * mm});
            skLineSegment(sketch, "E286", {"start": v(-178.79, 186.02) * mm, "end": v(-179, 187.58) * mm});
            skLineSegment(sketch, "E287", {"start": v(-179, 187.58) * mm, "end": v(-179.35, 189.8) * mm});
            skLineSegment(sketch, "E288", {"start": v(-179.35, 189.8) * mm, "end": v(-179.76, 192.41) * mm});
            skLineSegment(sketch, "E289", {"start": v(-179.76, 192.41) * mm, "end": v(-180.17, 195.15) * mm});
            skLineSegment(sketch, "E290", {"start": v(-180.17, 195.15) * mm, "end": v(-180.52, 197.75) * mm});
            skLineSegment(sketch, "E291", {"start": v(-180.52, 197.75) * mm, "end": v(-180.75, 199.93) * mm});
            skLineSegment(sketch, "E292", {"start": v(-180.75, 199.93) * mm, "end": v(-180.8, 201.44) * mm});
            skLineSegment(sketch, "E293", {"start": v(-180.8, 201.44) * mm, "end": v(-180.63, 202) * mm});
            skLineSegment(sketch, "E294", {"start": v(-180.63, 202) * mm, "end": v(-178.02, 202.16) * mm});
            skLineSegment(sketch, "E295", {"start": v(-178.02, 202.16) * mm, "end": v(-175.69, 202.59) * mm});
            skLineSegment(sketch, "E296", {"start": v(-175.69, 202.59) * mm, "end": v(-173.43, 203.19) * mm});
            skLineSegment(sketch, "E297", {"start": v(-173.43, 203.19) * mm, "end": v(-171.04, 203.88) * mm});
            skLineSegment(sketch, "E298", {"start": v(-171.04, 203.88) * mm, "end": v(-168.33, 204.57) * mm});
            skLineSegment(sketch, "E299", {"start": v(-168.33, 204.57) * mm, "end": v(-165.08, 205.17) * mm});
            skLineSegment(sketch, "E300", {"start": v(-165.08, 205.17) * mm, "end": v(-161.1, 205.6) * mm});
            skLineSegment(sketch, "E301", {"start": v(-161.1, 205.6) * mm, "end": v(-156.2, 205.76) * mm});
            skLineSegment(sketch, "E302", {"start": v(-156.2, 205.76) * mm, "end": v(-153.2, 205.97) * mm});
            skLineSegment(sketch, "E303", {"start": v(-153.2, 205.97) * mm, "end": v(-147.4, 206.51) * mm});
            skLineSegment(sketch, "E304", {"start": v(-147.4, 206.51) * mm, "end": v(-139.93, 207.24) * mm});
            skLineSegment(sketch, "E305", {"start": v(-139.93, 207.24) * mm, "end": v(-131.9, 208) * mm});
            skLineSegment(sketch, "E306", {"start": v(-131.9, 208) * mm, "end": v(-124.45, 208.66) * mm});
            skLineSegment(sketch, "E307", {"start": v(-124.45, 208.66) * mm, "end": v(-118.7, 209.08) * mm});
            skLineSegment(sketch, "E308", {"start": v(-118.7, 209.08) * mm, "end": v(-115.76, 209.1) * mm});
            skLineSegment(sketch, "E309", {"start": v(-115.76, 209.1) * mm, "end": v(-116.77, 208.58) * mm});
            skLineSegment(sketch, "E310", {"start": v(-116.77, 208.58) * mm, "end": v(-119.65, 207.13) * mm});
            skLineSegment(sketch, "E311", {"start": v(-119.65, 207.13) * mm, "end": v(-123.38, 204.2) * mm});
            skLineSegment(sketch, "E312", {"start": v(-123.38, 204.2) * mm, "end": v(-127.57, 200.17) * mm});
            skLineSegment(sketch, "E313", {"start": v(-127.57, 200.17) * mm, "end": v(-131.86, 195.44) * mm});
            skLineSegment(sketch, "E314", {"start": v(-131.86, 195.44) * mm, "end": v(-135.87, 190.38) * mm});
            skLineSegment(sketch, "E315", {"start": v(-135.87, 190.38) * mm, "end": v(-139.23, 185.38) * mm});
            skLineSegment(sketch, "E316", {"start": v(-139.23, 185.38) * mm, "end": v(-141.58, 180.83) * mm});
            skLineSegment(sketch, "E317", {"start": v(-141.58, 180.83) * mm, "end": v(-142.53, 177.1) * mm});
            skLineSegment(sketch, "E318", {"start": v(-142.53, 177.1) * mm, "end": v(-142.86, 176.42) * mm});
            skLineSegment(sketch, "E319", {"start": v(-142.86, 176.42) * mm, "end": v(-143.74, 174.64) * mm});
            skLineSegment(sketch, "E320", {"start": v(-143.74, 174.64) * mm, "end": v(-144.97, 172.08) * mm});
            skLineSegment(sketch, "E321", {"start": v(-144.97, 172.08) * mm, "end": v(-146.37, 169.02) * mm});
            skLineSegment(sketch, "E322", {"start": v(-146.37, 169.02) * mm, "end": v(-147.77, 165.76) * mm});
            skLineSegment(sketch, "E323", {"start": v(-147.77, 165.76) * mm, "end": v(-148.98, 162.62) * mm});
            skLineSegment(sketch, "E324", {"start": v(-148.98, 162.62) * mm, "end": v(-149.81, 159.87) * mm});
            skLineSegment(sketch, "E325", {"start": v(-149.81, 159.87) * mm, "end": v(-150.09, 157.84) * mm});
            skLineSegment(sketch, "E326", {"start": v(-150.09, 157.84) * mm, "end": v(-150.65, 156.44) * mm});
            skLineSegment(sketch, "E327", {"start": v(-150.65, 156.44) * mm, "end": v(-152.14, 152.82) * mm});
            skLineSegment(sketch, "E328", {"start": v(-152.14, 152.82) * mm, "end": v(-154.25, 147.7) * mm});
            skLineSegment(sketch, "E329", {"start": v(-154.25, 147.7) * mm, "end": v(-156.66, 141.79) * mm});
            skLineSegment(sketch, "E330", {"start": v(-156.66, 141.79) * mm, "end": v(-159.08, 135.8) * mm});
            skLineSegment(sketch, "E331", {"start": v(-159.08, 135.8) * mm, "end": v(-161.19, 130.44) * mm});
            skLineSegment(sketch, "E332", {"start": v(-161.19, 130.44) * mm, "end": v(-162.68, 126.43) * mm});
            skLineSegment(sketch, "E333", {"start": v(-162.68, 126.43) * mm, "end": v(-163.24, 124.48) * mm});
            skLineSegment(sketch, "E334", {"start": v(-163.24, 124.48) * mm, "end": v(-166.31, 124.57) * mm});
            skLineSegment(sketch, "E335", {"start": v(-166.31, 124.57) * mm, "end": v(-168.43, 124.39) * mm});
            skLineSegment(sketch, "E336", {"start": v(-168.43, 124.39) * mm, "end": v(-169.92, 124.11) * mm});
            skLineSegment(sketch, "E337", {"start": v(-169.92, 124.11) * mm, "end": v(-171.06, 123.93) * mm});
            skLineSegment(sketch, "E338", {"start": v(-171.06, 123.93) * mm, "end": v(-172.18, 124) * mm});
            skLineSegment(sketch, "E339", {"start": v(-172.18, 124) * mm, "end": v(-173.57, 124.53) * mm});
            skLineSegment(sketch, "E340", {"start": v(-173.57, 124.53) * mm, "end": v(-175.54, 125.69) * mm});
            skLineSegment(sketch, "E341", {"start": v(-175.54, 125.69) * mm, "end": v(-178.4, 127.65) * mm});
            skLineSegment(sketch, "E342", {"start": v(-178.4, 127.65) * mm, "end": v(-178.8, 127.83) * mm});
            skLineSegment(sketch, "E343", {"start": v(-178.8, 127.83) * mm, "end": v(-179.44, 128.03) * mm});
            skLineSegment(sketch, "E344", {"start": v(-179.44, 128.03) * mm, "end": v(-180.24, 128.25) * mm});
            skLineSegment(sketch, "E345", {"start": v(-180.24, 128.25) * mm, "end": v(-181.08, 128.49) * mm});
            skLineSegment(sketch, "E346", {"start": v(-181.08, 128.49) * mm, "end": v(-181.87, 128.75) * mm});
            skLineSegment(sketch, "E347", {"start": v(-181.87, 128.75) * mm, "end": v(-182.52, 129.03) * mm});
            skLineSegment(sketch, "E348", {"start": v(-182.52, 129.03) * mm, "end": v(-182.92, 129.33) * mm});
            skLineSegment(sketch, "E349", {"start": v(-182.92, 129.33) * mm, "end": v(-182.98, 129.65) * mm});
            skLineSegment(sketch, "E350", {"start": v(-297.61, 84.07) * mm, "end": v(-301.34, 89.4) * mm});
            skLineSegment(sketch, "E351", {"start": v(-301.34, 89.4) * mm, "end": v(-305.6, 93.22) * mm});
            skLineSegment(sketch, "E352", {"start": v(-305.6, 93.22) * mm, "end": v(-310.32, 95.94) * mm});
            skLineSegment(sketch, "E353", {"start": v(-310.32, 95.94) * mm, "end": v(-315.4, 97.96) * mm});
            skLineSegment(sketch, "E354", {"start": v(-315.4, 97.96) * mm, "end": v(-320.77, 99.7) * mm});
            skLineSegment(sketch, "E355", {"start": v(-320.77, 99.7) * mm, "end": v(-326.33, 101.6) * mm});
            skLineSegment(sketch, "E356", {"start": v(-326.33, 101.6) * mm, "end": v(-332, 104.04) * mm});
            skLineSegment(sketch, "E357", {"start": v(-332, 104.04) * mm, "end": v(-337.67, 107.44) * mm});
            skLineSegment(sketch, "E358", {"start": v(-337.67, 107.44) * mm, "end": v(-340.72, 108.36) * mm});
            skLineSegment(sketch, "E359", {"start": v(-340.72, 108.36) * mm, "end": v(-345.59, 108.42) * mm});
            skLineSegment(sketch, "E360", {"start": v(-345.59, 108.42) * mm, "end": v(-351.69, 107.74) * mm});
            skLineSegment(sketch, "E361", {"start": v(-351.69, 107.74) * mm, "end": v(-358.44, 106.43) * mm});
            skLineSegment(sketch, "E362", {"start": v(-358.44, 106.43) * mm, "end": v(-365.26, 104.61) * mm});
            skLineSegment(sketch, "E363", {"start": v(-365.26, 104.61) * mm, "end": v(-371.57, 102.4) * mm});
            skLineSegment(sketch, "E364", {"start": v(-371.57, 102.4) * mm, "end": v(-376.78, 99.9) * mm});
            skLineSegment(sketch, "E365", {"start": v(-376.78, 99.9) * mm, "end": v(-380.3, 97.23) * mm});
            skLineSegment(sketch, "E366", {"start": v(-380.3, 97.23) * mm, "end": v(-382.66, 94.97) * mm});
            skLineSegment(sketch, "E367", {"start": v(-382.66, 94.97) * mm, "end": v(-385.32, 92.86) * mm});
            skLineSegment(sketch, "E368", {"start": v(-385.32, 92.86) * mm, "end": v(-388.18, 90.76) * mm});
            skLineSegment(sketch, "E369", {"start": v(-388.18, 90.76) * mm, "end": v(-391.12, 88.53) * mm});
            skLineSegment(sketch, "E370", {"start": v(-391.12, 88.53) * mm, "end": v(-394.04, 86.03) * mm});
            skLineSegment(sketch, "E371", {"start": v(-394.04, 86.03) * mm, "end": v(-396.83, 83.14) * mm});
            skLineSegment(sketch, "E372", {"start": v(-396.83, 83.14) * mm, "end": v(-399.39, 79.71) * mm});
            skLineSegment(sketch, "E373", {"start": v(-399.39, 79.71) * mm, "end": v(-401.6, 75.62) * mm});
            skLineSegment(sketch, "E374", {"start": v(-401.6, 75.62) * mm, "end": v(-403.73, 70.68) * mm});
            skLineSegment(sketch, "E375", {"start": v(-403.73, 70.68) * mm, "end": v(-406.2, 64.4) * mm});
            skLineSegment(sketch, "E376", {"start": v(-406.2, 64.4) * mm, "end": v(-408.66, 57.25) * mm});
            skLineSegment(sketch, "E377", {"start": v(-408.66, 57.25) * mm, "end": v(-410.82, 49.66) * mm});
            skLineSegment(sketch, "E378", {"start": v(-410.82, 49.66) * mm, "end": v(-412.34, 42.09) * mm});
            skLineSegment(sketch, "E379", {"start": v(-412.34, 42.09) * mm, "end": v(-412.9, 34.98) * mm});
            skLineSegment(sketch, "E380", {"start": v(-412.9, 34.98) * mm, "end": v(-412.18, 28.8) * mm});
            skLineSegment(sketch, "E381", {"start": v(-412.18, 28.8) * mm, "end": v(-409.86, 23.97) * mm});
            skLineSegment(sketch, "E382", {"start": v(-409.86, 23.97) * mm, "end": v(-409.57, 23.05) * mm});
            skLineSegment(sketch, "E383", {"start": v(-409.57, 23.05) * mm, "end": v(-409.15, 21.09) * mm});
            skLineSegment(sketch, "E384", {"start": v(-409.15, 21.09) * mm, "end": v(-408.54, 18.4) * mm});
            skLineSegment(sketch, "E385", {"start": v(-408.54, 18.4) * mm, "end": v(-407.69, 15.27) * mm});
            skLineSegment(sketch, "E386", {"start": v(-407.69, 15.27) * mm, "end": v(-406.52, 12) * mm});
            skLineSegment(sketch, "E387", {"start": v(-406.52, 12) * mm, "end": v(-404.97, 8.9) * mm});
            skLineSegment(sketch, "E388", {"start": v(-404.97, 8.9) * mm, "end": v(-402.97, 6.25) * mm});
            skLineSegment(sketch, "E389", {"start": v(-402.97, 6.25) * mm, "end": v(-400.46, 4.36) * mm});
            skLineSegment(sketch, "E390", {"start": v(-400.46, 4.36) * mm, "end": v(-399.1, 3.33) * mm});
            skLineSegment(sketch, "E391", {"start": v(-399.1, 3.33) * mm, "end": v(-397.7, 1.78) * mm});
            skLineSegment(sketch, "E392", {"start": v(-397.7, 1.78) * mm, "end": v(-396.1, -0.14) * mm});
            skLineSegment(sketch, "E393", {"start": v(-396.1, -0.14) * mm, "end": v(-394.12, -2.27) * mm});
            skLineSegment(sketch, "E394", {"start": v(-394.12, -2.27) * mm, "end": v(-391.6, -4.46) * mm});
            skLineSegment(sketch, "E395", {"start": v(-391.6, -4.46) * mm, "end": v(-388.32, -6.55) * mm});
            skLineSegment(sketch, "E396", {"start": v(-388.32, -6.55) * mm, "end": v(-384.13, -8.4) * mm});
            skLineSegment(sketch, "E397", {"start": v(-384.13, -8.4) * mm, "end": v(-378.85, -9.85) * mm});
            skLineSegment(sketch, "E398", {"start": v(-378.85, -9.85) * mm, "end": v(-370.32, -11.46) * mm});
            skLineSegment(sketch, "E399", {"start": v(-370.32, -11.46) * mm, "end": v(-361.01, -12.81) * mm});
            skLineSegment(sketch, "E400", {"start": v(-361.01, -12.81) * mm, "end": v(-351.31, -13.6) * mm});
            skLineSegment(sketch, "E401", {"start": v(-351.31, -13.6) * mm, "end": v(-341.57, -13.5) * mm});
            skLineSegment(sketch, "E402", {"start": v(-341.57, -13.5) * mm, "end": v(-332.15, -12.2) * mm});
            skLineSegment(sketch, "E403", {"start": v(-332.15, -12.2) * mm, "end": v(-323.43, -9.42) * mm});
            skLineSegment(sketch, "E404", {"start": v(-323.43, -9.42) * mm, "end": v(-315.75, -4.82) * mm});
            skLineSegment(sketch, "E405", {"start": v(-315.75, -4.82) * mm, "end": v(-309.48, 1.9) * mm});
            skLineSegment(sketch, "E406", {"start": v(-309.48, 1.9) * mm, "end": v(-306.44, 6.16) * mm});
            skLineSegment(sketch, "E407", {"start": v(-306.44, 6.16) * mm, "end": v(-304.06, 9.36) * mm});
            skLineSegment(sketch, "E408", {"start": v(-304.06, 9.36) * mm, "end": v(-302.19, 11.9) * mm});
            skLineSegment(sketch, "E409", {"start": v(-302.19, 11.9) * mm, "end": v(-300.67, 14.24) * mm});
            skLineSegment(sketch, "E410", {"start": v(-300.67, 14.24) * mm, "end": v(-299.37, 16.8) * mm});
            skLineSegment(sketch, "E411", {"start": v(-299.37, 16.8) * mm, "end": v(-298.14, 20) * mm});
            skLineSegment(sketch, "E412", {"start": v(-298.14, 20) * mm, "end": v(-296.82, 24.26) * mm});
            skLineSegment(sketch, "E413", {"start": v(-296.82, 24.26) * mm, "end": v(-295.26, 30.04) * mm});
            skLineSegment(sketch, "E414", {"start": v(-295.26, 30.04) * mm, "end": v(-294.18, 34.7) * mm});
            skLineSegment(sketch, "E415", {"start": v(-294.18, 34.7) * mm, "end": v(-293.04, 40.53) * mm});
            skLineSegment(sketch, "E416", {"start": v(-293.04, 40.53) * mm, "end": v(-292.01, 47.12) * mm});
            skLineSegment(sketch, "E417", {"start": v(-292.01, 47.12) * mm, "end": v(-291.24, 54.05) * mm});
            skLineSegment(sketch, "E418", {"start": v(-291.24, 54.05) * mm, "end": v(-290.88, 60.93) * mm});
            skLineSegment(sketch, "E419", {"start": v(-290.88, 60.93) * mm, "end": v(-291.07, 67.34) * mm});
            skLineSegment(sketch, "E420", {"start": v(-291.07, 67.34) * mm, "end": v(-291.97, 72.88) * mm});
            skLineSegment(sketch, "E421", {"start": v(-291.97, 72.88) * mm, "end": v(-293.73, 77.15) * mm});
            skLineSegment(sketch, "E422", {"start": v(-293.73, 77.15) * mm, "end": v(-294.02, 77.62) * mm});
            skLineSegment(sketch, "E423", {"start": v(-294.02, 77.62) * mm, "end": v(-294.4, 78.28) * mm});
            skLineSegment(sketch, "E424", {"start": v(-294.4, 78.28) * mm, "end": v(-294.86, 79.08) * mm});
            skLineSegment(sketch, "E425", {"start": v(-294.86, 79.08) * mm, "end": v(-295.37, 80) * mm});
            skLineSegment(sketch, "E426", {"start": v(-295.37, 80) * mm, "end": v(-295.92, 81) * mm});
            skLineSegment(sketch, "E427", {"start": v(-295.92, 81) * mm, "end": v(-296.5, 82.03) * mm});
            skLineSegment(sketch, "E428", {"start": v(-296.5, 82.03) * mm, "end": v(-297.06, 83.07) * mm});
            skLineSegment(sketch, "E429", {"start": v(-297.06, 83.07) * mm, "end": v(-297.61, 84.07) * mm});
            skLineSegment(sketch, "E430", {"start": v(-265.2, 93) * mm, "end": v(-264.93, 89.11) * mm});
            skLineSegment(sketch, "E431", {"start": v(-264.93, 89.11) * mm, "end": v(-264.27, 86.41) * mm});
            skLineSegment(sketch, "E432", {"start": v(-264.27, 86.41) * mm, "end": v(-263.45, 84.42) * mm});
            skLineSegment(sketch, "E433", {"start": v(-263.45, 84.42) * mm, "end": v(-262.7, 82.67) * mm});
            skLineSegment(sketch, "E434", {"start": v(-262.7, 82.67) * mm, "end": v(-262.23, 80.68) * mm});
            skLineSegment(sketch, "E435", {"start": v(-262.23, 80.68) * mm, "end": v(-262.28, 77.99) * mm});
            skLineSegment(sketch, "E436", {"start": v(-262.28, 77.99) * mm, "end": v(-263.08, 74.1) * mm});
            skLineSegment(sketch, "E437", {"start": v(-263.08, 74.1) * mm, "end": v(-264.85, 68.57) * mm});
            skLineSegment(sketch, "E438", {"start": v(-264.85, 68.57) * mm, "end": v(-266.08, 62.28) * mm});
            skLineSegment(sketch, "E439", {"start": v(-266.08, 62.28) * mm, "end": v(-265.8, 55.67) * mm});
            skLineSegment(sketch, "E440", {"start": v(-265.8, 55.67) * mm, "end": v(-264.59, 48.85) * mm});
            skLineSegment(sketch, "E441", {"start": v(-264.59, 48.85) * mm, "end": v(-262.97, 41.95) * mm});
            skLineSegment(sketch, "E442", {"start": v(-262.97, 41.95) * mm, "end": v(-261.52, 35.07) * mm});
            skLineSegment(sketch, "E443", {"start": v(-261.52, 35.07) * mm, "end": v(-260.78, 28.35) * mm});
            skLineSegment(sketch, "E444", {"start": v(-260.78, 28.35) * mm, "end": v(-261.31, 21.9) * mm});
            skLineSegment(sketch, "E445", {"start": v(-261.31, 21.9) * mm, "end": v(-263.66, 15.83) * mm});
            skLineSegment(sketch, "E446", {"start": v(-263.66, 15.83) * mm, "end": v(-264.3, 13.3) * mm});
            skLineSegment(sketch, "E447", {"start": v(-264.3, 13.3) * mm, "end": v(-262.95, 11.73) * mm});
            skLineSegment(sketch, "E448", {"start": v(-262.95, 11.73) * mm, "end": v(-260.1, 10.97) * mm});
            skLineSegment(sketch, "E449", {"start": v(-260.1, 10.97) * mm, "end": v(-256.25, 10.92) * mm});
            skLineSegment(sketch, "E450", {"start": v(-256.25, 10.92) * mm, "end": v(-251.88, 11.45) * mm});
            skLineSegment(sketch, "E451", {"start": v(-251.88, 11.45) * mm, "end": v(-247.5, 12.45) * mm});
            skLineSegment(sketch, "E452", {"start": v(-247.5, 12.45) * mm, "end": v(-243.59, 13.8) * mm});
            skLineSegment(sketch, "E453", {"start": v(-243.59, 13.8) * mm, "end": v(-240.64, 15.36) * mm});
            skLineSegment(sketch, "E454", {"start": v(-240.64, 15.36) * mm, "end": v(-239.86, 15.44) * mm});
            skLineSegment(sketch, "E455", {"start": v(-239.86, 15.44) * mm, "end": v(-237.93, 15.79) * mm});
            skLineSegment(sketch, "E456", {"start": v(-237.93, 15.79) * mm, "end": v(-235.4, 16.57) * mm});
            skLineSegment(sketch, "E457", {"start": v(-235.4, 16.57) * mm, "end": v(-232.8, 17.97) * mm});
            skLineSegment(sketch, "E458", {"start": v(-232.8, 17.97) * mm, "end": v(-230.68, 20.17) * mm});
            skLineSegment(sketch, "E459", {"start": v(-230.68, 20.17) * mm, "end": v(-229.6, 23.37) * mm});
            skLineSegment(sketch, "E460", {"start": v(-229.6, 23.37) * mm, "end": v(-230.07, 27.73) * mm});
            skLineSegment(sketch, "E461", {"start": v(-230.07, 27.73) * mm, "end": v(-232.66, 33.45) * mm});
            skLineSegment(sketch, "E462", {"start": v(-232.66, 33.45) * mm, "end": v(-233.36, 36.37) * mm});
            skLineSegment(sketch, "E463", {"start": v(-233.36, 36.37) * mm, "end": v(-233.05, 40.38) * mm});
            skLineSegment(sketch, "E464", {"start": v(-233.05, 40.38) * mm, "end": v(-232.15, 45.26) * mm});
            skLineSegment(sketch, "E465", {"start": v(-232.15, 45.26) * mm, "end": v(-231.1, 50.78) * mm});
            skLineSegment(sketch, "E466", {"start": v(-231.1, 50.78) * mm, "end": v(-230.33, 56.72) * mm});
            skLineSegment(sketch, "E467", {"start": v(-230.33, 56.72) * mm, "end": v(-230.28, 62.85) * mm});
            skLineSegment(sketch, "E468", {"start": v(-230.28, 62.85) * mm, "end": v(-231.38, 68.95) * mm});
            skLineSegment(sketch, "E469", {"start": v(-231.38, 68.95) * mm, "end": v(-234.07, 74.8) * mm});
            skLineSegment(sketch, "E470", {"start": v(-234.07, 74.8) * mm, "end": v(-234.34, 76.6) * mm});
            skLineSegment(sketch, "E471", {"start": v(-234.34, 76.6) * mm, "end": v(-233.85, 79.31) * mm});
            skLineSegment(sketch, "E472", {"start": v(-233.85, 79.31) * mm, "end": v(-232.97, 82.6) * mm});
            skLineSegment(sketch, "E473", {"start": v(-232.97, 82.6) * mm, "end": v(-232.07, 86.12) * mm});
            skLineSegment(sketch, "E474", {"start": v(-232.07, 86.12) * mm, "end": v(-231.53, 89.5) * mm});
            skLineSegment(sketch, "E475", {"start": v(-231.53, 89.5) * mm, "end": v(-231.72, 92.4) * mm});
            skLineSegment(sketch, "E476", {"start": v(-231.72, 92.4) * mm, "end": v(-233.01, 94.45) * mm});
            skLineSegment(sketch, "E477", {"start": v(-233.01, 94.45) * mm, "end": v(-235.78, 95.3) * mm});
            skLineSegment(sketch, "E478", {"start": v(-235.78, 95.3) * mm, "end": v(-236.28, 95.53) * mm});
            skLineSegment(sketch, "E479", {"start": v(-236.28, 95.53) * mm, "end": v(-237.63, 96.1) * mm});
            skLineSegment(sketch, "E480", {"start": v(-237.63, 96.1) * mm, "end": v(-239.66, 96.9) * mm});
            skLineSegment(sketch, "E481", {"start": v(-239.66, 96.9) * mm, "end": v(-242.23, 97.8) * mm});
            skLineSegment(sketch, "E482", {"start": v(-242.23, 97.8) * mm, "end": v(-245.19, 98.7) * mm});
            skLineSegment(sketch, "E483", {"start": v(-245.19, 98.7) * mm, "end": v(-248.38, 99.44) * mm});
            skLineSegment(sketch, "E484", {"start": v(-248.38, 99.44) * mm, "end": v(-251.65, 99.94) * mm});
            skLineSegment(sketch, "E485", {"start": v(-251.65, 99.94) * mm, "end": v(-254.86, 100.05) * mm});
            skLineSegment(sketch, "E486", {"start": v(-254.86, 100.05) * mm, "end": v(-257.16, 100.06) * mm});
            skLineSegment(sketch, "E487", {"start": v(-257.16, 100.06) * mm, "end": v(-259.9, 100.13) * mm});
            skLineSegment(sketch, "E488", {"start": v(-259.9, 100.13) * mm, "end": v(-262.79, 100.05) * mm});
            skLineSegment(sketch, "E489", {"start": v(-262.79, 100.05) * mm, "end": v(-265.47, 99.63) * mm});
            skLineSegment(sketch, "E490", {"start": v(-265.47, 99.63) * mm, "end": v(-267.63, 98.67) * mm});
            skLineSegment(sketch, "E491", {"start": v(-267.63, 98.67) * mm, "end": v(-268.94, 96.98) * mm});
            skLineSegment(sketch, "E492", {"start": v(-268.94, 96.98) * mm, "end": v(-269.07, 94.36) * mm});
            skLineSegment(sketch, "E493", {"start": v(-269.07, 94.36) * mm, "end": v(-267.7, 90.6) * mm});
            skLineSegment(sketch, "E494", {"start": v(-267.7, 90.6) * mm, "end": v(-267.53, 90.45) * mm});
            skLineSegment(sketch, "E495", {"start": v(-267.53, 90.45) * mm, "end": v(-267.16, 90.22) * mm});
            skLineSegment(sketch, "E496", {"start": v(-267.16, 90.22) * mm, "end": v(-266.65, 89.93) * mm});
            skLineSegment(sketch, "E497", {"start": v(-266.65, 89.93) * mm, "end": v(-266.07, 89.62) * mm});
            skLineSegment(sketch, "E498", {"start": v(-266.07, 89.62) * mm, "end": v(-265.48, 89.32) * mm});
            skLineSegment(sketch, "E499", {"start": v(-265.48, 89.32) * mm, "end": v(-264.94, 89.06) * mm});
            skLineSegment(sketch, "E500", {"start": v(-264.94, 89.06) * mm, "end": v(-264.5, 88.87) * mm});
            skLineSegment(sketch, "E501", {"start": v(-264.5, 88.87) * mm, "end": v(-264.26, 88.77) * mm});
            skLineSegment(sketch, "E502", {"start": v(-208.35, -37.14) * mm, "end": v(-207.25, -36.1) * mm});
            skLineSegment(sketch, "E503", {"start": v(-207.25, -36.1) * mm, "end": v(-205.8, -35.28) * mm});
            skLineSegment(sketch, "E504", {"start": v(-205.8, -35.28) * mm, "end": v(-204.13, -34.85) * mm});
            skLineSegment(sketch, "E505", {"start": v(-204.13, -34.85) * mm, "end": v(-202.43, -34.91) * mm});
            skLineSegment(sketch, "E506", {"start": v(-202.43, -34.91) * mm, "end": v(-200.86, -35.6) * mm});
            skLineSegment(sketch, "E507", {"start": v(-200.86, -35.6) * mm, "end": v(-199.57, -37.05) * mm});
            skLineSegment(sketch, "E508", {"start": v(-199.57, -37.05) * mm, "end": v(-198.72, -39.4) * mm});
            skLineSegment(sketch, "E509", {"start": v(-198.72, -39.4) * mm, "end": v(-198.48, -42.74) * mm});
            skLineSegment(sketch, "E510", {"start": v(-198.48, -42.74) * mm, "end": v(-198.16, -44.16) * mm});
            skLineSegment(sketch, "E511", {"start": v(-198.16, -44.16) * mm, "end": v(-197.3, -47.3) * mm});
            skLineSegment(sketch, "E512", {"start": v(-197.3, -47.3) * mm, "end": v(-196.06, -51.63) * mm});
            skLineSegment(sketch, "E513", {"start": v(-196.06, -51.63) * mm, "end": v(-194.61, -56.58) * mm});
            skLineSegment(sketch, "E514", {"start": v(-194.61, -56.58) * mm, "end": v(-193.13, -61.59) * mm});
            skLineSegment(sketch, "E515", {"start": v(-193.13, -61.59) * mm, "end": v(-191.77, -66.11) * mm});
            skLineSegment(sketch, "E516", {"start": v(-191.77, -66.11) * mm, "end": v(-190.7, -69.6) * mm});
            skLineSegment(sketch, "E517", {"start": v(-190.7, -69.6) * mm, "end": v(-190.1, -71.48) * mm});
            skLineSegment(sketch, "E518", {"start": v(-190.1, -71.48) * mm, "end": v(-188.77, -75.18) * mm});
            skLineSegment(sketch, "E519", {"start": v(-188.77, -75.18) * mm, "end": v(-187.72, -77.8) * mm});
            skLineSegment(sketch, "E520", {"start": v(-187.72, -77.8) * mm, "end": v(-186.87, -79.76) * mm});
            skLineSegment(sketch, "E521", {"start": v(-186.87, -79.76) * mm, "end": v(-186.16, -81.45) * mm});
            skLineSegment(sketch, "E522", {"start": v(-186.16, -81.45) * mm, "end": v(-185.5, -83.28) * mm});
            skLineSegment(sketch, "E523", {"start": v(-185.5, -83.28) * mm, "end": v(-184.8, -85.64) * mm});
            skLineSegment(sketch, "E524", {"start": v(-184.8, -85.64) * mm, "end": v(-184, -88.93) * mm});
            skLineSegment(sketch, "E525", {"start": v(-184, -88.93) * mm, "end": v(-183.02, -93.56) * mm});
            skLineSegment(sketch, "E526", {"start": v(-183.02, -93.56) * mm, "end": v(-181.56, -98.04) * mm});
            skLineSegment(sketch, "E527", {"start": v(-181.56, -98.04) * mm, "end": v(-178.46, -106.08) * mm});
            skLineSegment(sketch, "E528", {"start": v(-178.46, -106.08) * mm, "end": v(-174.23, -116.45) * mm});
            skLineSegment(sketch, "E529", {"start": v(-174.23, -116.45) * mm, "end": v(-169.4, -127.88) * mm});
            skLineSegment(sketch, "E530", {"start": v(-169.4, -127.88) * mm, "end": v(-164.46, -139.12) * mm});
            skLineSegment(sketch, "E531", {"start": v(-164.46, -139.12) * mm, "end": v(-159.96, -148.92) * mm});
            skLineSegment(sketch, "E532", {"start": v(-159.96, -148.92) * mm, "end": v(-156.39, -156.03) * mm});
            skLineSegment(sketch, "E533", {"start": v(-156.39, -156.03) * mm, "end": v(-154.28, -159.18) * mm});
            skLineSegment(sketch, "E534", {"start": v(-154.28, -159.18) * mm, "end": v(-153.54, -160.23) * mm});
            skLineSegment(sketch, "E535", {"start": v(-153.54, -160.23) * mm, "end": v(-151.66, -163) * mm});
            skLineSegment(sketch, "E536", {"start": v(-151.66, -163) * mm, "end": v(-148.89, -166.97) * mm});
            skLineSegment(sketch, "E537", {"start": v(-148.89, -166.97) * mm, "end": v(-145.49, -171.68) * mm});
            skLineSegment(sketch, "E538", {"start": v(-145.49, -171.68) * mm, "end": v(-141.73, -176.63) * mm});
            skLineSegment(sketch, "E539", {"start": v(-141.73, -176.63) * mm, "end": v(-137.86, -181.34) * mm});
            skLineSegment(sketch, "E540", {"start": v(-137.86, -181.34) * mm, "end": v(-134.15, -185.32) * mm});
            skLineSegment(sketch, "E541", {"start": v(-134.15, -185.32) * mm, "end": v(-130.86, -188.08) * mm});
            skLineSegment(sketch, "E542", {"start": v(-130.86, -188.08) * mm, "end": v(-128.36, -190.07) * mm});
            skLineSegment(sketch, "E543", {"start": v(-128.36, -190.07) * mm, "end": v(-125.52, -192.8) * mm});
            skLineSegment(sketch, "E544", {"start": v(-125.52, -192.8) * mm, "end": v(-122.37, -196.02) * mm});
            skLineSegment(sketch, "E545", {"start": v(-122.37, -196.02) * mm, "end": v(-118.93, -199.5) * mm});
            skLineSegment(sketch, "E546", {"start": v(-118.93, -199.5) * mm, "end": v(-115.22, -203.04) * mm});
            skLineSegment(sketch, "E547", {"start": v(-115.22, -203.04) * mm, "end": v(-111.25, -206.39) * mm});
            skLineSegment(sketch, "E548", {"start": v(-111.25, -206.39) * mm, "end": v(-107.05, -209.32) * mm});
            skLineSegment(sketch, "E549", {"start": v(-107.05, -209.32) * mm, "end": v(-102.63, -211.61) * mm});
            skLineSegment(sketch, "E550", {"start": v(-102.63, -211.61) * mm, "end": v(-100.39, -212.67) * mm});
            skLineSegment(sketch, "E551", {"start": v(-100.39, -212.67) * mm, "end": v(-97.24, -214.3) * mm});
            skLineSegment(sketch, "E552", {"start": v(-97.24, -214.3) * mm, "end": v(-93.52, -216.36) * mm});
            skLineSegment(sketch, "E553", {"start": v(-93.52, -216.36) * mm, "end": v(-89.55, -218.65) * mm});
            skLineSegment(sketch, "E554", {"start": v(-89.55, -218.65) * mm, "end": v(-85.65, -221.01) * mm});
            skLineSegment(sketch, "E555", {"start": v(-85.65, -221.01) * mm, "end": v(-82.15, -223.28) * mm});
            skLineSegment(sketch, "E556", {"start": v(-82.15, -223.28) * mm, "end": v(-79.36, -225.28) * mm});
            skLineSegment(sketch, "E557", {"start": v(-79.36, -225.28) * mm, "end": v(-77.61, -226.83) * mm});
            skLineSegment(sketch, "E558", {"start": v(-77.61, -226.83) * mm, "end": v(-75.35, -227.85) * mm});
            skLineSegment(sketch, "E559", {"start": v(-75.35, -227.85) * mm, "end": v(-70.27, -229.48) * mm});
            skLineSegment(sketch, "E560", {"start": v(-70.27, -229.48) * mm, "end": v(-63.27, -231.5) * mm});
            skLineSegment(sketch, "E561", {"start": v(-63.27, -231.5) * mm, "end": v(-55.27, -233.67) * mm});
            skLineSegment(sketch, "E562", {"start": v(-55.27, -233.67) * mm, "end": v(-47.16, -235.76) * mm});
            skLineSegment(sketch, "E563", {"start": v(-47.16, -235.76) * mm, "end": v(-39.87, -237.53) * mm});
            skLineSegment(sketch, "E564", {"start": v(-39.87, -237.53) * mm, "end": v(-34.3, -238.74) * mm});
            skLineSegment(sketch, "E565", {"start": v(-34.3, -238.74) * mm, "end": v(-31.34, -239.17) * mm});
            skLineSegment(sketch, "E566", {"start": v(-31.34, -239.17) * mm, "end": v(-28.5, -239.2) * mm});
            skLineSegment(sketch, "E567", {"start": v(-28.5, -239.2) * mm, "end": v(-25.13, -239.41) * mm});
            skLineSegment(sketch, "E568", {"start": v(-25.13, -239.41) * mm, "end": v(-21.38, -239.68) * mm});
            skLineSegment(sketch, "E569", {"start": v(-21.38, -239.68) * mm, "end": v(-17.41, -239.9) * mm});
            skLineSegment(sketch, "E570", {"start": v(-17.41, -239.9) * mm, "end": v(-13.39, -240) * mm});
            skLineSegment(sketch, "E571", {"start": v(-13.39, -240) * mm, "end": v(-9.46, -239.83) * mm});
            skLineSegment(sketch, "E572", {"start": v(-9.46, -239.83) * mm, "end": v(-5.8, -239.32) * mm});
            skLineSegment(sketch, "E573", {"start": v(-5.8, -239.32) * mm, "end": v(-2.56, -238.35) * mm});
            skLineSegment(sketch, "E574", {"start": v(-2.56, -238.35) * mm, "end": v(0.9, -237.4) * mm});
            skLineSegment(sketch, "E575", {"start": v(0.9, -237.4) * mm, "end": v(6.54, -236.32) * mm});
            skLineSegment(sketch, "E576", {"start": v(6.54, -236.32) * mm, "end": v(13.62, -235.08) * mm});
            skLineSegment(sketch, "E577", {"start": v(13.62, -235.08) * mm, "end": v(21.38, -233.7) * mm});
            skLineSegment(sketch, "E578", {"start": v(21.38, -233.7) * mm, "end": v(29.08, -232.14) * mm});
            skLineSegment(sketch, "E579", {"start": v(29.08, -232.14) * mm, "end": v(35.97, -230.43) * mm});
            skLineSegment(sketch, "E580", {"start": v(35.97, -230.43) * mm, "end": v(41.3, -228.54) * mm});
            skLineSegment(sketch, "E581", {"start": v(41.3, -228.54) * mm, "end": v(44.3, -226.48) * mm});
            skLineSegment(sketch, "E582", {"start": v(44.3, -226.48) * mm, "end": v(45.3, -225.97) * mm});
            skLineSegment(sketch, "E583", {"start": v(45.3, -225.97) * mm, "end": v(47.92, -224.65) * mm});
            skLineSegment(sketch, "E584", {"start": v(47.92, -224.65) * mm, "end": v(51.64, -222.76) * mm});
            skLineSegment(sketch, "E585", {"start": v(51.64, -222.76) * mm, "end": v(55.96, -220.53) * mm});
            skLineSegment(sketch, "E586", {"start": v(55.96, -220.53) * mm, "end": v(60.36, -218.19) * mm});
            skLineSegment(sketch, "E587", {"start": v(60.36, -218.19) * mm, "end": v(64.33, -215.98) * mm});
            skLineSegment(sketch, "E588", {"start": v(64.33, -215.98) * mm, "end": v(67.38, -214.12) * mm});
            skLineSegment(sketch, "E589", {"start": v(67.38, -214.12) * mm, "end": v(68.97, -212.86) * mm});
            skLineSegment(sketch, "E590", {"start": v(68.97, -212.86) * mm, "end": v(70.56, -211.22) * mm});
            skLineSegment(sketch, "E591", {"start": v(70.56, -211.22) * mm, "end": v(72.48, -209.73) * mm});
            skLineSegment(sketch, "E592", {"start": v(72.48, -209.73) * mm, "end": v(74.66, -208.25) * mm});
            skLineSegment(sketch, "E593", {"start": v(74.66, -208.25) * mm, "end": v(77.04, -206.65) * mm});
            skLineSegment(sketch, "E594", {"start": v(77.04, -206.65) * mm, "end": v(79.54, -204.8) * mm});
            skLineSegment(sketch, "E595", {"start": v(79.54, -204.8) * mm, "end": v(82.09, -202.55) * mm});
            skLineSegment(sketch, "E596", {"start": v(82.09, -202.55) * mm, "end": v(84.62, -199.8) * mm});
            skLineSegment(sketch, "E597", {"start": v(84.62, -199.8) * mm, "end": v(87.05, -196.37) * mm});
            skLineSegment(sketch, "E598", {"start": v(87.05, -196.37) * mm, "end": v(87.45, -196.13) * mm});
            skLineSegment(sketch, "E599", {"start": v(87.45, -196.13) * mm, "end": v(88.5, -195.46) * mm});
            skLineSegment(sketch, "E600", {"start": v(88.5, -195.46) * mm, "end": v(90.07, -194.38) * mm});
            skLineSegment(sketch, "E601", {"start": v(90.07, -194.38) * mm, "end": v(92.02, -192.9) * mm});
            skLineSegment(sketch, "E602", {"start": v(92.02, -192.9) * mm, "end": v(94.2, -191.03) * mm});
            skLineSegment(sketch, "E603", {"start": v(94.2, -191.03) * mm, "end": v(96.46, -188.8) * mm});
            skLineSegment(sketch, "E604", {"start": v(96.46, -188.8) * mm, "end": v(98.67, -186.2) * mm});
            skLineSegment(sketch, "E605", {"start": v(98.67, -186.2) * mm, "end": v(100.68, -183.26) * mm});
            skLineSegment(sketch, "E606", {"start": v(100.68, -183.26) * mm, "end": v(102.55, -180.18) * mm});
            skLineSegment(sketch, "E607", {"start": v(102.55, -180.18) * mm, "end": v(104.55, -177) * mm});
            skLineSegment(sketch, "E608", {"start": v(104.55, -177) * mm, "end": v(106.66, -173.8) * mm});
            skLineSegment(sketch, "E609", {"start": v(106.66, -173.8) * mm, "end": v(108.9, -170.62) * mm});
            skLineSegment(sketch, "E610", {"start": v(108.9, -170.62) * mm, "end": v(111.22, -167.54) * mm});
            skLineSegment(sketch, "E611", {"start": v(111.22, -167.54) * mm, "end": v(113.66, -164.6) * mm});
            skLineSegment(sketch, "E612", {"start": v(113.66, -164.6) * mm, "end": v(116.2, -161.9) * mm});
            skLineSegment(sketch, "E613", {"start": v(116.2, -161.9) * mm, "end": v(118.81, -159.46) * mm});
            skLineSegment(sketch, "E614", {"start": v(118.81, -159.46) * mm, "end": v(119.37, -158.55) * mm});
            skLineSegment(sketch, "E615", {"start": v(119.37, -158.55) * mm, "end": v(120.79, -156.15) * mm});
            skLineSegment(sketch, "E616", {"start": v(120.79, -156.15) * mm, "end": v(122.79, -152.73) * mm});
            skLineSegment(sketch, "E617", {"start": v(122.79, -152.73) * mm, "end": v(125.1, -148.72) * mm});
            skLineSegment(sketch, "E618", {"start": v(125.1, -148.72) * mm, "end": v(127.42, -144.57) * mm});
            skLineSegment(sketch, "E619", {"start": v(127.42, -144.57) * mm, "end": v(129.5, -140.74) * mm});
            skLineSegment(sketch, "E620", {"start": v(129.5, -140.74) * mm, "end": v(131.04, -137.65) * mm});
            skLineSegment(sketch, "E621", {"start": v(131.04, -137.65) * mm, "end": v(131.77, -135.77) * mm});
            skLineSegment(sketch, "E622", {"start": v(131.77, -135.77) * mm, "end": v(133.01, -130.16) * mm});
            skLineSegment(sketch, "E623", {"start": v(133.01, -130.16) * mm, "end": v(134.21, -124.63) * mm});
            skLineSegment(sketch, "E624", {"start": v(134.21, -124.63) * mm, "end": v(135, -119.27) * mm});
            skLineSegment(sketch, "E625", {"start": v(135, -119.27) * mm, "end": v(135.02, -114.16) * mm});
            skLineSegment(sketch, "E626", {"start": v(135.02, -114.16) * mm, "end": v(133.9, -109.4) * mm});
            skLineSegment(sketch, "E627", {"start": v(133.9, -109.4) * mm, "end": v(131.28, -105.07) * mm});
            skLineSegment(sketch, "E628", {"start": v(131.28, -105.07) * mm, "end": v(126.79, -101.28) * mm});
            skLineSegment(sketch, "E629", {"start": v(126.79, -101.28) * mm, "end": v(120.06, -98.1) * mm});
            skLineSegment(sketch, "E630", {"start": v(120.06, -98.1) * mm, "end": v(112.64, -96.14) * mm});
            skLineSegment(sketch, "E631", {"start": v(112.64, -96.14) * mm, "end": v(105.05, -95.4) * mm});
            skLineSegment(sketch, "E632", {"start": v(105.05, -95.4) * mm, "end": v(97.4, -95.76) * mm});
            skLineSegment(sketch, "E633", {"start": v(97.4, -95.76) * mm, "end": v(89.83, -97.12) * mm});
            skLineSegment(sketch, "E634", {"start": v(89.83, -97.12) * mm, "end": v(82.45, -99.37) * mm});
            skLineSegment(sketch, "E635", {"start": v(82.45, -99.37) * mm, "end": v(75.38, -102.41) * mm});
            skLineSegment(sketch, "E636", {"start": v(75.38, -102.41) * mm, "end": v(68.73, -106.14) * mm});
            skLineSegment(sketch, "E637", {"start": v(68.73, -106.14) * mm, "end": v(62.62, -110.44) * mm});
            skLineSegment(sketch, "E638", {"start": v(62.62, -110.44) * mm, "end": v(59, -113.04) * mm});
            skLineSegment(sketch, "E639", {"start": v(59, -113.04) * mm, "end": v(55.67, -115.13) * mm});
            skLineSegment(sketch, "E640", {"start": v(55.67, -115.13) * mm, "end": v(52.57, -117.03) * mm});
            skLineSegment(sketch, "E641", {"start": v(52.57, -117.03) * mm, "end": v(49.67, -119.07) * mm});
            skLineSegment(sketch, "E642", {"start": v(49.67, -119.07) * mm, "end": v(46.92, -121.57) * mm});
            skLineSegment(sketch, "E643", {"start": v(46.92, -121.57) * mm, "end": v(44.28, -124.86) * mm});
            skLineSegment(sketch, "E644", {"start": v(44.28, -124.86) * mm, "end": v(41.7, -129.26) * mm});
            skLineSegment(sketch, "E645", {"start": v(41.7, -129.26) * mm, "end": v(39.13, -135.1) * mm});
            skLineSegment(sketch, "E646", {"start": v(39.13, -135.1) * mm, "end": v(38.07, -138.33) * mm});
            skLineSegment(sketch, "E647", {"start": v(38.07, -138.33) * mm, "end": v(37.3, -141.85) * mm});
            skLineSegment(sketch, "E648", {"start": v(37.3, -141.85) * mm, "end": v(36.9, -145.5) * mm});
            skLineSegment(sketch, "E649", {"start": v(36.9, -145.5) * mm, "end": v(36.92, -149.15) * mm});
            skLineSegment(sketch, "E650", {"start": v(36.92, -149.15) * mm, "end": v(37.47, -152.65) * mm});
            skLineSegment(sketch, "E651", {"start": v(37.47, -152.65) * mm, "end": v(38.61, -155.86) * mm});
            skLineSegment(sketch, "E652", {"start": v(38.61, -155.86) * mm, "end": v(40.42, -158.65) * mm});
            skLineSegment(sketch, "E653", {"start": v(40.42, -158.65) * mm, "end": v(42.97, -160.87) * mm});
            skLineSegment(sketch, "E654", {"start": v(42.97, -160.87) * mm, "end": v(44.2, -161.45) * mm});
            skLineSegment(sketch, "E655", {"start": v(44.2, -161.45) * mm, "end": v(45.53, -161.75) * mm});
            skLineSegment(sketch, "E656", {"start": v(45.53, -161.75) * mm, "end": v(47, -161.93) * mm});
            skLineSegment(sketch, "E657", {"start": v(47, -161.93) * mm, "end": v(48.67, -162.13) * mm});
            skLineSegment(sketch, "E658", {"start": v(48.67, -162.13) * mm, "end": v(50.6, -162.5) * mm});
            skLineSegment(sketch, "E659", {"start": v(50.6, -162.5) * mm, "end": v(52.85, -163.2) * mm});
            skLineSegment(sketch, "E660", {"start": v(52.85, -163.2) * mm, "end": v(55.47, -164.4) * mm});
            skLineSegment(sketch, "E661", {"start": v(55.47, -164.4) * mm, "end": v(58.52, -166.22) * mm});
            skLineSegment(sketch, "E662", {"start": v(58.52, -166.22) * mm, "end": v(60.3, -166.88) * mm});
            skLineSegment(sketch, "E663", {"start": v(60.3, -166.88) * mm, "end": v(63.43, -167.73) * mm});
            skLineSegment(sketch, "E664", {"start": v(63.43, -167.73) * mm, "end": v(67.18, -168.82) * mm});
            skLineSegment(sketch, "E665", {"start": v(67.18, -168.82) * mm, "end": v(70.8, -170.2) * mm});
            skLineSegment(sketch, "E666", {"start": v(70.8, -170.2) * mm, "end": v(73.56, -171.9) * mm});
            skLineSegment(sketch, "E667", {"start": v(73.56, -171.9) * mm, "end": v(74.71, -173.96) * mm});
            skLineSegment(sketch, "E668", {"start": v(74.71, -173.96) * mm, "end": v(73.5, -176.44) * mm});
            skLineSegment(sketch, "E669", {"start": v(73.5, -176.44) * mm, "end": v(69.2, -179.38) * mm});
            skLineSegment(sketch, "E670", {"start": v(69.2, -179.38) * mm, "end": v(67.6, -180.1) * mm});
            skLineSegment(sketch, "E671", {"start": v(67.6, -180.1) * mm, "end": v(64.95, -181.17) * mm});
            skLineSegment(sketch, "E672", {"start": v(64.95, -181.17) * mm, "end": v(61.62, -182.47) * mm});
            skLineSegment(sketch, "E673", {"start": v(61.62, -182.47) * mm, "end": v(58.02, -183.86) * mm});
            skLineSegment(sketch, "E674", {"start": v(58.02, -183.86) * mm, "end": v(54.53, -185.2) * mm});
            skLineSegment(sketch, "E675", {"start": v(54.53, -185.2) * mm, "end": v(51.55, -186.33) * mm});
            skLineSegment(sketch, "E676", {"start": v(51.55, -186.33) * mm, "end": v(49.47, -187.14) * mm});
            skLineSegment(sketch, "E677", {"start": v(49.47, -187.14) * mm, "end": v(48.69, -187.49) * mm});
            skLineSegment(sketch, "E678", {"start": v(48.69, -187.49) * mm, "end": v(46.2, -192.08) * mm});
            skLineSegment(sketch, "E679", {"start": v(46.2, -192.08) * mm, "end": v(40.24, -195.94) * mm});
            skLineSegment(sketch, "E680", {"start": v(40.24, -195.94) * mm, "end": v(31.78, -199.1) * mm});
            skLineSegment(sketch, "E681", {"start": v(31.78, -199.1) * mm, "end": v(21.8, -201.62) * mm});
            skLineSegment(sketch, "E682", {"start": v(21.8, -201.62) * mm, "end": v(11.26, -203.5) * mm});
            skLineSegment(sketch, "E683", {"start": v(11.26, -203.5) * mm, "end": v(1.14, -204.81) * mm});
            skLineSegment(sketch, "E684", {"start": v(1.14, -204.81) * mm, "end": v(-7.59, -205.57) * mm});
            skLineSegment(sketch, "E685", {"start": v(-7.59, -205.57) * mm, "end": v(-13.96, -205.81) * mm});
            skLineSegment(sketch, "E686", {"start": v(-13.96, -205.81) * mm, "end": v(-25.06, -205.5) * mm});
            skLineSegment(sketch, "E687", {"start": v(-25.06, -205.5) * mm, "end": v(-33.97, -204.57) * mm});
            skLineSegment(sketch, "E688", {"start": v(-33.97, -204.57) * mm, "end": v(-41.35, -202.97) * mm});
            skLineSegment(sketch, "E689", {"start": v(-41.35, -202.97) * mm, "end": v(-47.87, -200.68) * mm});
            skLineSegment(sketch, "E690", {"start": v(-47.87, -200.68) * mm, "end": v(-54.2, -197.66) * mm});
            skLineSegment(sketch, "E691", {"start": v(-54.2, -197.66) * mm, "end": v(-61.02, -193.88) * mm});
            skLineSegment(sketch, "E692", {"start": v(-61.02, -193.88) * mm, "end": v(-69, -189.3) * mm});
            skLineSegment(sketch, "E693", {"start": v(-69, -189.3) * mm, "end": v(-78.8, -183.92) * mm});
            skLineSegment(sketch, "E694", {"start": v(-78.8, -183.92) * mm, "end": v(-82.85, -181.15) * mm});
            skLineSegment(sketch, "E695", {"start": v(-82.85, -181.15) * mm, "end": v(-87.4, -177.06) * mm});
            skLineSegment(sketch, "E696", {"start": v(-87.4, -177.06) * mm, "end": v(-92.2, -172.02) * mm});
            skLineSegment(sketch, "E697", {"start": v(-92.2, -172.02) * mm, "end": v(-97.04, -166.4) * mm});
            skLineSegment(sketch, "E698", {"start": v(-97.04, -166.4) * mm, "end": v(-101.65, -160.58) * mm});
            skLineSegment(sketch, "E699", {"start": v(-101.65, -160.58) * mm, "end": v(-105.83, -154.93) * mm});
            skLineSegment(sketch, "E700", {"start": v(-105.83, -154.93) * mm, "end": v(-109.3, -149.82) * mm});
            skLineSegment(sketch, "E701", {"start": v(-109.3, -149.82) * mm, "end": v(-111.87, -145.63) * mm});
            skLineSegment(sketch, "E702", {"start": v(-111.87, -145.63) * mm, "end": v(-113.89, -142.39) * mm});
            skLineSegment(sketch, "E703", {"start": v(-113.89, -142.39) * mm, "end": v(-115.65, -140.08) * mm});
            skLineSegment(sketch, "E704", {"start": v(-115.65, -140.08) * mm, "end": v(-117.2, -138.3) * mm});
            skLineSegment(sketch, "E705", {"start": v(-117.2, -138.3) * mm, "end": v(-118.6, -136.65) * mm});
            skLineSegment(sketch, "E706", {"start": v(-118.6, -136.65) * mm, "end": v(-119.85, -134.71) * mm});
            skLineSegment(sketch, "E707", {"start": v(-119.85, -134.71) * mm, "end": v(-121.03, -132.08) * mm});
            skLineSegment(sketch, "E708", {"start": v(-121.03, -132.08) * mm, "end": v(-122.17, -128.34) * mm});
            skLineSegment(sketch, "E709", {"start": v(-122.17, -128.34) * mm, "end": v(-123.3, -123.08) * mm});
            skLineSegment(sketch, "E710", {"start": v(-123.3, -123.08) * mm, "end": v(-123.77, -121.24) * mm});
            skLineSegment(sketch, "E711", {"start": v(-123.77, -121.24) * mm, "end": v(-124.63, -118.23) * mm});
            skLineSegment(sketch, "E712", {"start": v(-124.63, -118.23) * mm, "end": v(-125.77, -114.4) * mm});
            skLineSegment(sketch, "E713", {"start": v(-125.77, -114.4) * mm, "end": v(-127.04, -110.15) * mm});
            skLineSegment(sketch, "E714", {"start": v(-127.04, -110.15) * mm, "end": v(-128.32, -105.84) * mm});
            skLineSegment(sketch, "E715", {"start": v(-128.32, -105.84) * mm, "end": v(-129.45, -101.86) * mm});
            skLineSegment(sketch, "E716", {"start": v(-129.45, -101.86) * mm, "end": v(-130.32, -98.56) * mm});
            skLineSegment(sketch, "E717", {"start": v(-130.32, -98.56) * mm, "end": v(-130.78, -96.34) * mm});
            skLineSegment(sketch, "E718", {"start": v(-130.78, -96.34) * mm, "end": v(-131.78, -90.17) * mm});
            skLineSegment(sketch, "E719", {"start": v(-131.78, -90.17) * mm, "end": v(-132.9, -84.56) * mm});
            skLineSegment(sketch, "E720", {"start": v(-132.9, -84.56) * mm, "end": v(-134.08, -79.27) * mm});
            skLineSegment(sketch, "E721", {"start": v(-134.08, -79.27) * mm, "end": v(-135.23, -74.05) * mm});
            skLineSegment(sketch, "E722", {"start": v(-135.23, -74.05) * mm, "end": v(-136.26, -68.64) * mm});
            skLineSegment(sketch, "E723", {"start": v(-136.26, -68.64) * mm, "end": v(-137.1, -62.81) * mm});
            skLineSegment(sketch, "E724", {"start": v(-137.1, -62.81) * mm, "end": v(-137.67, -56.31) * mm});
            skLineSegment(sketch, "E725", {"start": v(-137.67, -56.31) * mm, "end": v(-137.87, -48.89) * mm});
            skLineSegment(sketch, "E726", {"start": v(-137.87, -48.89) * mm, "end": v(-138.03, -42.72) * mm});
            skLineSegment(sketch, "E727", {"start": v(-138.03, -42.72) * mm, "end": v(-138.46, -36.14) * mm});
            skLineSegment(sketch, "E728", {"start": v(-138.46, -36.14) * mm, "end": v(-139.06, -29.27) * mm});
            skLineSegment(sketch, "E729", {"start": v(-139.06, -29.27) * mm, "end": v(-139.75, -22.22) * mm});
            skLineSegment(sketch, "E730", {"start": v(-139.75, -22.22) * mm, "end": v(-140.44, -15.1) * mm});
            skLineSegment(sketch, "E731", {"start": v(-140.44, -15.1) * mm, "end": v(-141.04, -8.03) * mm});
            skLineSegment(sketch, "E732", {"start": v(-141.04, -8.03) * mm, "end": v(-141.47, -1.11) * mm});
            skLineSegment(sketch, "E733", {"start": v(-141.47, -1.11) * mm, "end": v(-141.63, 5.53) * mm});
            skLineSegment(sketch, "E734", {"start": v(-141.63, 5.53) * mm, "end": v(-141.3, 11.04) * mm});
            skLineSegment(sketch, "E735", {"start": v(-141.3, 11.04) * mm, "end": v(-140.36, 15.76) * mm});
            skLineSegment(sketch, "E736", {"start": v(-140.36, 15.76) * mm, "end": v(-138.82, 19.84) * mm});
            skLineSegment(sketch, "E737", {"start": v(-138.82, 19.84) * mm, "end": v(-136.73, 23.44) * mm});
            skLineSegment(sketch, "E738", {"start": v(-136.73, 23.44) * mm, "end": v(-134.1, 26.73) * mm});
            skLineSegment(sketch, "E739", {"start": v(-134.1, 26.73) * mm, "end": v(-131, 29.87) * mm});
            skLineSegment(sketch, "E740", {"start": v(-131, 29.87) * mm, "end": v(-127.43, 33) * mm});
            skLineSegment(sketch, "E741", {"start": v(-127.43, 33) * mm, "end": v(-123.43, 36.31) * mm});
            skLineSegment(sketch, "E742", {"start": v(-123.43, 36.31) * mm, "end": v(-120.12, 38.2) * mm});
            skLineSegment(sketch, "E743", {"start": v(-120.12, 38.2) * mm, "end": v(-115.75, 39.54) * mm});
            skLineSegment(sketch, "E744", {"start": v(-115.75, 39.54) * mm, "end": v(-110.62, 40.45) * mm});
            skLineSegment(sketch, "E745", {"start": v(-110.62, 40.45) * mm, "end": v(-105.05, 41) * mm});
            skLineSegment(sketch, "E746", {"start": v(-105.05, 41) * mm, "end": v(-99.36, 41.27) * mm});
            skLineSegment(sketch, "E747", {"start": v(-99.36, 41.27) * mm, "end": v(-93.88, 41.35) * mm});
            skLineSegment(sketch, "E748", {"start": v(-93.88, 41.35) * mm, "end": v(-88.91, 41.34) * mm});
            skLineSegment(sketch, "E749", {"start": v(-88.91, 41.34) * mm, "end": v(-84.78, 41.32) * mm});
            skLineSegment(sketch, "E750", {"start": v(-187.67, -4.26) * mm, "end": v(-184.96, -3.37) * mm});
            skLineSegment(sketch, "E751", {"start": v(-184.96, -3.37) * mm, "end": v(-181.1, -2.65) * mm});
            skLineSegment(sketch, "E752", {"start": v(-181.1, -2.65) * mm, "end": v(-176.57, -2.2) * mm});
            skLineSegment(sketch, "E753", {"start": v(-176.57, -2.2) * mm, "end": v(-171.83, -2.1) * mm});
            skLineSegment(sketch, "E754", {"start": v(-171.83, -2.1) * mm, "end": v(-167.33, -2.46) * mm});
            skLineSegment(sketch, "E755", {"start": v(-167.33, -2.46) * mm, "end": v(-163.54, -3.35) * mm});
            skLineSegment(sketch, "E756", {"start": v(-163.54, -3.35) * mm, "end": v(-160.93, -4.87) * mm});
            skLineSegment(sketch, "E757", {"start": v(-160.93, -4.87) * mm, "end": v(-159.95, -7.11) * mm});
            skLineSegment(sketch, "E758", {"start": v(-159.95, -7.11) * mm, "end": v(-159.77, -10.1) * mm});
            skLineSegment(sketch, "E759", {"start": v(-159.77, -10.1) * mm, "end": v(-159.28, -15.54) * mm});
            skLineSegment(sketch, "E760", {"start": v(-159.28, -15.54) * mm, "end": v(-158.58, -22.57) * mm});
            skLineSegment(sketch, "E761", {"start": v(-158.58, -22.57) * mm, "end": v(-157.76, -30.32) * mm});
            skLineSegment(sketch, "E762", {"start": v(-157.76, -30.32) * mm, "end": v(-156.92, -37.97) * mm});
            skLineSegment(sketch, "E763", {"start": v(-156.92, -37.97) * mm, "end": v(-156.13, -44.65) * mm});
            skLineSegment(sketch, "E764", {"start": v(-156.13, -44.65) * mm, "end": v(-155.5, -49.51) * mm});
            skLineSegment(sketch, "E765", {"start": v(-155.5, -49.51) * mm, "end": v(-155.13, -51.7) * mm});
            skLineSegment(sketch, "E766", {"start": v(-155.13, -51.7) * mm, "end": v(-153.51, -57.4) * mm});
            skLineSegment(sketch, "E767", {"start": v(-153.51, -57.4) * mm, "end": v(-151.94, -65.25) * mm});
            skLineSegment(sketch, "E768", {"start": v(-151.94, -65.25) * mm, "end": v(-150.35, -74.5) * mm});
            skLineSegment(sketch, "E769", {"start": v(-150.35, -74.5) * mm, "end": v(-148.7, -84.38) * mm});
            skLineSegment(sketch, "E770", {"start": v(-148.7, -84.38) * mm, "end": v(-146.92, -94.15) * mm});
            skLineSegment(sketch, "E771", {"start": v(-146.92, -94.15) * mm, "end": v(-144.97, -103.06) * mm});
            skLineSegment(sketch, "E772", {"start": v(-144.97, -103.06) * mm, "end": v(-142.8, -110.35) * mm});
            skLineSegment(sketch, "E773", {"start": v(-142.8, -110.35) * mm, "end": v(-140.34, -115.26) * mm});
            skLineSegment(sketch, "E774", {"start": v(-140.34, -115.26) * mm, "end": v(-140.18, -116.05) * mm});
            skLineSegment(sketch, "E775", {"start": v(-140.18, -116.05) * mm, "end": v(-139.7, -118.17) * mm});
            skLineSegment(sketch, "E776", {"start": v(-139.7, -118.17) * mm, "end": v(-138.86, -121.36) * mm});
            skLineSegment(sketch, "E777", {"start": v(-138.86, -121.36) * mm, "end": v(-137.62, -125.34) * mm});
            skLineSegment(sketch, "E778", {"start": v(-137.62, -125.34) * mm, "end": v(-135.9, -129.84) * mm});
            skLineSegment(sketch, "E779", {"start": v(-135.9, -129.84) * mm, "end": v(-133.68, -134.6) * mm});
            skLineSegment(sketch, "E780", {"start": v(-133.68, -134.6) * mm, "end": v(-130.9, -139.34) * mm});
            skLineSegment(sketch, "E781", {"start": v(-130.9, -139.34) * mm, "end": v(-127.5, -143.8) * mm});
            skLineSegment(sketch, "E782", {"start": v(-127.5, -143.8) * mm, "end": v(-125.04, -147.14) * mm});
            skLineSegment(sketch, "E783", {"start": v(-125.04, -147.14) * mm, "end": v(-122.38, -151.56) * mm});
            skLineSegment(sketch, "E784", {"start": v(-122.38, -151.56) * mm, "end": v(-119.54, -156.63) * mm});
            skLineSegment(sketch, "E785", {"start": v(-119.54, -156.63) * mm, "end": v(-116.54, -161.9) * mm});
            skLineSegment(sketch, "E786", {"start": v(-116.54, -161.9) * mm, "end": v(-113.43, -166.93) * mm});
            skLineSegment(sketch, "E787", {"start": v(-113.43, -166.93) * mm, "end": v(-110.22, -171.3) * mm});
            skLineSegment(sketch, "E788", {"start": v(-110.22, -171.3) * mm, "end": v(-106.94, -174.55) * mm});
            skLineSegment(sketch, "E789", {"start": v(-106.94, -174.55) * mm, "end": v(-103.61, -176.25) * mm});
            skLineSegment(sketch, "E790", {"start": v(-103.61, -176.25) * mm, "end": v(-102.67, -176.9) * mm});
            skLineSegment(sketch, "E791", {"start": v(-102.67, -176.9) * mm, "end": v(-101.03, -178.4) * mm});
            skLineSegment(sketch, "E792", {"start": v(-101.03, -178.4) * mm, "end": v(-98.84, -180.5) * mm});
            skLineSegment(sketch, "E793", {"start": v(-98.84, -180.5) * mm, "end": v(-96.24, -182.94) * mm});
            skLineSegment(sketch, "E794", {"start": v(-96.24, -182.94) * mm, "end": v(-93.39, -185.44) * mm});
            skLineSegment(sketch, "E795", {"start": v(-93.39, -185.44) * mm, "end": v(-90.42, -187.76) * mm});
            skLineSegment(sketch, "E796", {"start": v(-90.42, -187.76) * mm, "end": v(-87.5, -189.62) * mm});
            skLineSegment(sketch, "E797", {"start": v(-87.5, -189.62) * mm, "end": v(-84.74, -190.78) * mm});
            skLineSegment(sketch, "E798", {"start": v(-84.74, -190.78) * mm, "end": v(-81.21, -192.18) * mm});
            skLineSegment(sketch, "E799", {"start": v(-81.21, -192.18) * mm, "end": v(-78.28, -194.14) * mm});
            skLineSegment(sketch, "E800", {"start": v(-78.28, -194.14) * mm, "end": v(-75.56, -196.5) * mm});
            skLineSegment(sketch, "E801", {"start": v(-75.56, -196.5) * mm, "end": v(-72.67, -199.1) * mm});
            skLineSegment(sketch, "E802", {"start": v(-72.67, -199.1) * mm, "end": v(-69.24, -201.78) * mm});
            skLineSegment(sketch, "E803", {"start": v(-69.24, -201.78) * mm, "end": v(-64.89, -204.39) * mm});
            skLineSegment(sketch, "E804", {"start": v(-64.89, -204.39) * mm, "end": v(-59.23, -206.76) * mm});
            skLineSegment(sketch, "E805", {"start": v(-59.23, -206.76) * mm, "end": v(-51.9, -208.75) * mm});
            skLineSegment(sketch, "E806", {"start": v(-51.9, -208.75) * mm, "end": v(-49.81, -209.18) * mm});
            skLineSegment(sketch, "E807", {"start": v(-49.81, -209.18) * mm, "end": v(-47.13, -209.74) * mm});
            skLineSegment(sketch, "E808", {"start": v(-47.13, -209.74) * mm, "end": v(-44.05, -210.4) * mm});
            skLineSegment(sketch, "E809", {"start": v(-44.05, -210.4) * mm, "end": v(-40.8, -211.15) * mm});
            skLineSegment(sketch, "E810", {"start": v(-40.8, -211.15) * mm, "end": v(-37.62, -211.97) * mm});
            skLineSegment(sketch, "E811", {"start": v(-37.62, -211.97) * mm, "end": v(-34.72, -212.83) * mm});
            skLineSegment(sketch, "E812", {"start": v(-34.72, -212.83) * mm, "end": v(-32.31, -213.72) * mm});
            skLineSegment(sketch, "E813", {"start": v(-32.31, -213.72) * mm, "end": v(-30.63, -214.62) * mm});
            skLineSegment(sketch, "E814", {"start": v(-30.63, -214.62) * mm, "end": v(-26.32, -215.85) * mm});
            skLineSegment(sketch, "E815", {"start": v(-26.32, -215.85) * mm, "end": v(-19.22, -215.99) * mm});
            skLineSegment(sketch, "E816", {"start": v(-19.22, -215.99) * mm, "end": v(-10.22, -215.26) * mm});
            skLineSegment(sketch, "E817", {"start": v(-10.22, -215.26) * mm, "end": v(-0.25, -213.91) * mm});
            skLineSegment(sketch, "E818", {"start": v(-0.25, -213.91) * mm, "end": v(9.8, -212.16) * mm});
            skLineSegment(sketch, "E819", {"start": v(9.8, -212.16) * mm, "end": v(19, -210.25) * mm});
            skLineSegment(sketch, "E820", {"start": v(19, -210.25) * mm, "end": v(26.46, -208.41) * mm});
            skLineSegment(sketch, "E821", {"start": v(26.46, -208.41) * mm, "end": v(31.27, -206.87) * mm});
            skLineSegment(sketch, "E822", {"start": v(31.27, -206.87) * mm, "end": v(32.59, -206.46) * mm});
            skLineSegment(sketch, "E823", {"start": v(32.59, -206.46) * mm, "end": v(34.18, -206.13) * mm});
            skLineSegment(sketch, "E824", {"start": v(34.18, -206.13) * mm, "end": v(36.02, -205.81) * mm});
            skLineSegment(sketch, "E825", {"start": v(36.02, -205.81) * mm, "end": v(38.1, -205.4) * mm});
            skLineSegment(sketch, "E826", {"start": v(38.1, -205.4) * mm, "end": v(40.38, -204.84) * mm});
            skLineSegment(sketch, "E827", {"start": v(40.38, -204.84) * mm, "end": v(42.85, -204) * mm});
            skLineSegment(sketch, "E828", {"start": v(42.85, -204) * mm, "end": v(45.5, -202.83) * mm});
            skLineSegment(sketch, "E829", {"start": v(45.5, -202.83) * mm, "end": v(48.3, -201.23) * mm});
            skLineSegment(sketch, "E830", {"start": v(48.3, -201.23) * mm, "end": v(51.26, -199.55) * mm});
            skLineSegment(sketch, "E831", {"start": v(51.26, -199.55) * mm, "end": v(55.95, -197.07) * mm});
            skLineSegment(sketch, "E832", {"start": v(55.95, -197.07) * mm, "end": v(61.72, -194.05) * mm});
            skLineSegment(sketch, "E833", {"start": v(61.72, -194.05) * mm, "end": v(67.93, -190.75) * mm});
            skLineSegment(sketch, "E834", {"start": v(67.93, -190.75) * mm, "end": v(73.95, -187.4) * mm});
            skLineSegment(sketch, "E835", {"start": v(73.95, -187.4) * mm, "end": v(79.14, -184.25) * mm});
            skLineSegment(sketch, "E836", {"start": v(79.14, -184.25) * mm, "end": v(82.85, -181.57) * mm});
            skLineSegment(sketch, "E837", {"start": v(82.85, -181.57) * mm, "end": v(84.44, -179.58) * mm});
            skLineSegment(sketch, "E838", {"start": v(84.44, -179.58) * mm, "end": v(85.13, -179.08) * mm});
            skLineSegment(sketch, "E839", {"start": v(85.13, -179.08) * mm, "end": v(86.79, -177.76) * mm});
            skLineSegment(sketch, "E840", {"start": v(86.79, -177.76) * mm, "end": v(89.08, -175.85) * mm});
            skLineSegment(sketch, "E841", {"start": v(89.08, -175.85) * mm, "end": v(91.66, -173.55) * mm});
            skLineSegment(sketch, "E842", {"start": v(91.66, -173.55) * mm, "end": v(94.22, -171.1) * mm});
            skLineSegment(sketch, "E843", {"start": v(94.22, -171.1) * mm, "end": v(96.43, -168.7) * mm});
            skLineSegment(sketch, "E844", {"start": v(96.43, -168.7) * mm, "end": v(97.95, -166.57) * mm});
            skLineSegment(sketch, "E845", {"start": v(97.95, -166.57) * mm, "end": v(98.45, -164.94) * mm});
            skLineSegment(sketch, "E846", {"start": v(103.62, -168.22) * mm, "end": v(104, -167.2) * mm});
            skLineSegment(sketch, "E847", {"start": v(104, -167.2) * mm, "end": v(104.4, -166.23) * mm});
            skLineSegment(sketch, "E848", {"start": v(104.4, -166.23) * mm, "end": v(104.8, -165.3) * mm});
            skLineSegment(sketch, "E849", {"start": v(104.8, -165.3) * mm, "end": v(105.16, -164.41) * mm});
            skLineSegment(sketch, "E850", {"start": v(105.16, -164.41) * mm, "end": v(105.49, -163.53) * mm});
            skLineSegment(sketch, "E851", {"start": v(105.49, -163.53) * mm, "end": v(105.74, -162.63) * mm});
            skLineSegment(sketch, "E852", {"start": v(105.74, -162.63) * mm, "end": v(105.9, -161.7) * mm});
            skLineSegment(sketch, "E853", {"start": v(105.9, -161.7) * mm, "end": v(105.97, -160.7) * mm});
            skLineSegment(sketch, "E854", {"start": v(105.97, -160.7) * mm, "end": v(106.67, -156.93) * mm});
            skLineSegment(sketch, "E855", {"start": v(106.67, -156.93) * mm, "end": v(108.48, -152.06) * mm});
            skLineSegment(sketch, "E856", {"start": v(108.48, -152.06) * mm, "end": v(110.92, -146.47) * mm});
            skLineSegment(sketch, "E857", {"start": v(110.92, -146.47) * mm, "end": v(113.52, -140.52) * mm});
            skLineSegment(sketch, "E858", {"start": v(113.52, -140.52) * mm, "end": v(115.82, -134.58) * mm});
            skLineSegment(sketch, "E859", {"start": v(115.82, -134.58) * mm, "end": v(117.35, -129) * mm});
            skLineSegment(sketch, "E860", {"start": v(117.35, -129) * mm, "end": v(117.64, -124.16) * mm});
            skLineSegment(sketch, "E861", {"start": v(117.64, -124.16) * mm, "end": v(116.22, -120.42) * mm});
            skLineSegment(sketch, "E862", {"start": v(116.22, -120.42) * mm, "end": v(113.85, -117.44) * mm});
            skLineSegment(sketch, "E863", {"start": v(113.85, -117.44) * mm, "end": v(111.76, -114.97) * mm});
            skLineSegment(sketch, "E864", {"start": v(111.76, -114.97) * mm, "end": v(109.79, -113) * mm});
            skLineSegment(sketch, "E865", {"start": v(109.79, -113) * mm, "end": v(107.76, -111.46) * mm});
            skLineSegment(sketch, "E866", {"start": v(107.76, -111.46) * mm, "end": v(105.5, -110.34) * mm});
            skLineSegment(sketch, "E867", {"start": v(105.5, -110.34) * mm, "end": v(102.83, -109.58) * mm});
            skLineSegment(sketch, "E868", {"start": v(102.83, -109.58) * mm, "end": v(99.59, -109.16) * mm});
            skLineSegment(sketch, "E869", {"start": v(99.59, -109.16) * mm, "end": v(95.6, -109.03) * mm});
            skLineSegment(sketch, "E870", {"start": v(95.6, -109.03) * mm, "end": v(94.65, -109.15) * mm});
            skLineSegment(sketch, "E871", {"start": v(94.65, -109.15) * mm, "end": v(92.37, -109.48) * mm});
            skLineSegment(sketch, "E872", {"start": v(92.37, -109.48) * mm, "end": v(89.16, -109.96) * mm});
            skLineSegment(sketch, "E873", {"start": v(89.16, -109.96) * mm, "end": v(85.44, -110.52) * mm});
            skLineSegment(sketch, "E874", {"start": v(85.44, -110.52) * mm, "end": v(81.61, -111.1) * mm});
            skLineSegment(sketch, "E875", {"start": v(81.61, -111.1) * mm, "end": v(78.09, -111.65) * mm});
            skLineSegment(sketch, "E876", {"start": v(78.09, -111.65) * mm, "end": v(75.28, -112.08) * mm});
            skLineSegment(sketch, "E877", {"start": v(75.28, -112.08) * mm, "end": v(73.6, -112.36) * mm});
            skLineSegment(sketch, "E878", {"start": v(73.6, -112.36) * mm, "end": v(70.62, -113.35) * mm});
            skLineSegment(sketch, "E879", {"start": v(70.62, -113.35) * mm, "end": v(67.94, -115.14) * mm});
            skLineSegment(sketch, "E880", {"start": v(67.94, -115.14) * mm, "end": v(65.5, -117.54) * mm});
            skLineSegment(sketch, "E881", {"start": v(65.5, -117.54) * mm, "end": v(63.26, -120.35) * mm});
            skLineSegment(sketch, "E882", {"start": v(63.26, -120.35) * mm, "end": v(61.15, -123.39) * mm});
            skLineSegment(sketch, "E883", {"start": v(61.15, -123.39) * mm, "end": v(59.11, -126.45) * mm});
            skLineSegment(sketch, "E884", {"start": v(59.11, -126.45) * mm, "end": v(57.1, -129.35) * mm});
            skLineSegment(sketch, "E885", {"start": v(57.1, -129.35) * mm, "end": v(55.07, -131.89) * mm});
            skLineSegment(sketch, "E886", {"start": v(55.07, -131.89) * mm, "end": v(52.08, -135.32) * mm});
            skLineSegment(sketch, "E887", {"start": v(52.08, -135.32) * mm, "end": v(50.18, -137.82) * mm});
            skLineSegment(sketch, "E888", {"start": v(50.18, -137.82) * mm, "end": v(49.18, -139.62) * mm});
            skLineSegment(sketch, "E889", {"start": v(49.18, -139.62) * mm, "end": v(48.9, -140.98) * mm});
            skLineSegment(sketch, "E890", {"start": v(48.9, -140.98) * mm, "end": v(49.16, -142.14) * mm});
            skLineSegment(sketch, "E891", {"start": v(49.16, -142.14) * mm, "end": v(49.78, -143.36) * mm});
            skLineSegment(sketch, "E892", {"start": v(49.78, -143.36) * mm, "end": v(50.59, -144.89) * mm});
            skLineSegment(sketch, "E893", {"start": v(50.59, -144.89) * mm, "end": v(51.39, -146.96) * mm});
            skLineSegment(sketch, "E894", {"start": v(51.39, -146.96) * mm, "end": v(53.81, -151.22) * mm});
            skLineSegment(sketch, "E895", {"start": v(53.81, -151.22) * mm, "end": v(57.67, -153.95) * mm});
            skLineSegment(sketch, "E896", {"start": v(57.67, -153.95) * mm, "end": v(62.5, -155.37) * mm});
            skLineSegment(sketch, "E897", {"start": v(62.5, -155.37) * mm, "end": v(67.8, -155.7) * mm});
            skLineSegment(sketch, "E898", {"start": v(67.8, -155.7) * mm, "end": v(73.13, -155.17) * mm});
            skLineSegment(sketch, "E899", {"start": v(73.13, -155.17) * mm, "end": v(78, -153.97) * mm});
            skLineSegment(sketch, "E900", {"start": v(78, -153.97) * mm, "end": v(81.96, -152.34) * mm});
            skLineSegment(sketch, "E901", {"start": v(81.96, -152.34) * mm, "end": v(84.52, -150.5) * mm});
            skLineSegment(sketch, "E902", {"start": v(84.52, -150.5) * mm, "end": v(87.91, -145.92) * mm});
            skLineSegment(sketch, "E903", {"start": v(87.91, -145.92) * mm, "end": v(90.5, -140.9) * mm});
            skLineSegment(sketch, "E904", {"start": v(90.5, -140.9) * mm, "end": v(92.14, -135.94) * mm});
            skLineSegment(sketch, "E905", {"start": v(92.14, -135.94) * mm, "end": v(92.75, -131.54) * mm});
            skLineSegment(sketch, "E906", {"start": v(92.75, -131.54) * mm, "end": v(92.2, -128.21) * mm});
            skLineSegment(sketch, "E907", {"start": v(92.2, -128.21) * mm, "end": v(90.38, -126.46) * mm});
            skLineSegment(sketch, "E908", {"start": v(90.38, -126.46) * mm, "end": v(87.18, -126.78) * mm});
            skLineSegment(sketch, "E909", {"start": v(87.18, -126.78) * mm, "end": v(82.48, -129.7) * mm});
            skLineSegment(sketch, "E910", {"start": v(82.48, -129.7) * mm, "end": v(82.27, -135.14) * mm});
            skLineSegment(sketch, "E911", {"start": v(82.27, -135.14) * mm, "end": v(81.6, -139.42) * mm});
            skLineSegment(sketch, "E912", {"start": v(81.6, -139.42) * mm, "end": v(80.35, -142.65) * mm});
            skLineSegment(sketch, "E913", {"start": v(80.35, -142.65) * mm, "end": v(78.41, -144.96) * mm});
            skLineSegment(sketch, "E914", {"start": v(78.41, -144.96) * mm, "end": v(75.7, -146.45) * mm});
            skLineSegment(sketch, "E915", {"start": v(75.7, -146.45) * mm, "end": v(72.1, -147.23) * mm});
            skLineSegment(sketch, "E916", {"start": v(72.1, -147.23) * mm, "end": v(67.5, -147.42) * mm});
            skLineSegment(sketch, "E917", {"start": v(67.5, -147.42) * mm, "end": v(61.8, -147.12) * mm});
            skLineSegment(sketch, "E918", {"start": v(61.8, -147.12) * mm, "end": v(60.47, -146.46) * mm});
            skLineSegment(sketch, "E919", {"start": v(60.47, -146.46) * mm, "end": v(59.23, -144.85) * mm});
            skLineSegment(sketch, "E920", {"start": v(59.23, -144.85) * mm, "end": v(58.3, -142.54) * mm});
            skLineSegment(sketch, "E921", {"start": v(58.3, -142.54) * mm, "end": v(57.9, -139.78) * mm});
            skLineSegment(sketch, "E922", {"start": v(57.9, -139.78) * mm, "end": v(58.3, -136.8) * mm});
            skLineSegment(sketch, "E923", {"start": v(58.3, -136.8) * mm, "end": v(59.7, -133.87) * mm});
            skLineSegment(sketch, "E924", {"start": v(59.7, -133.87) * mm, "end": v(62.36, -131.22) * mm});
            skLineSegment(sketch, "E925", {"start": v(62.36, -131.22) * mm, "end": v(66.5, -129.1) * mm});
            skLineSegment(sketch, "E926", {"start": v(66.5, -129.1) * mm, "end": v(67.7, -128.5) * mm});
            skLineSegment(sketch, "E927", {"start": v(67.7, -128.5) * mm, "end": v(68.55, -127.7) * mm});
            skLineSegment(sketch, "E928", {"start": v(68.55, -127.7) * mm, "end": v(69.26, -126.8) * mm});
            skLineSegment(sketch, "E929", {"start": v(69.26, -126.8) * mm, "end": v(70.02, -125.87) * mm});
            skLineSegment(sketch, "E930", {"start": v(70.02, -125.87) * mm, "end": v(71, -124.97) * mm});
            skLineSegment(sketch, "E931", {"start": v(71, -124.97) * mm, "end": v(72.42, -124.18) * mm});
            skLineSegment(sketch, "E932", {"start": v(72.42, -124.18) * mm, "end": v(74.46, -123.55) * mm});
            skLineSegment(sketch, "E933", {"start": v(74.46, -123.55) * mm, "end": v(77.3, -123.16) * mm});
            skLineSegment(sketch, "E934", {"start": v(77.3, -123.16) * mm, "end": v(78.64, -122.33) * mm});
            skLineSegment(sketch, "E935", {"start": v(78.64, -122.33) * mm, "end": v(82.03, -120.33) * mm});
            skLineSegment(sketch, "E936", {"start": v(82.03, -120.33) * mm, "end": v(86.8, -117.85) * mm});
            skLineSegment(sketch, "E937", {"start": v(86.8, -117.85) * mm, "end": v(92.23, -115.6) * mm});
            skLineSegment(sketch, "E938", {"start": v(92.23, -115.6) * mm, "end": v(97.6, -114.3) * mm});
            skLineSegment(sketch, "E939", {"start": v(97.6, -114.3) * mm, "end": v(102.24, -114.65) * mm});
            skLineSegment(sketch, "E940", {"start": v(102.24, -114.65) * mm, "end": v(105.42, -117.36) * mm});
            skLineSegment(sketch, "E941", {"start": v(105.42, -117.36) * mm, "end": v(106.44, -123.12) * mm});
            skLineSegment(sketch, "E942", {"start": v(106.44, -123.12) * mm, "end": v(106.58, -125.79) * mm});
            skLineSegment(sketch, "E943", {"start": v(106.58, -125.79) * mm, "end": v(107.1, -127.6) * mm});
            skLineSegment(sketch, "E944", {"start": v(107.1, -127.6) * mm, "end": v(107.7, -128.9) * mm});
            skLineSegment(sketch, "E945", {"start": v(107.7, -128.9) * mm, "end": v(108.13, -130.1) * mm});
            skLineSegment(sketch, "E946", {"start": v(108.13, -130.1) * mm, "end": v(108.13, -131.54) * mm});
            skLineSegment(sketch, "E947", {"start": v(108.13, -131.54) * mm, "end": v(107.4, -133.6) * mm});
            skLineSegment(sketch, "E948", {"start": v(107.4, -133.6) * mm, "end": v(105.7, -136.67) * mm});
            skLineSegment(sketch, "E949", {"start": v(105.7, -136.67) * mm, "end": v(102.76, -141.1) * mm});
            skLineSegment(sketch, "E950", {"start": v(102.76, -141.1) * mm, "end": v(102.1, -142.18) * mm});
            skLineSegment(sketch, "E951", {"start": v(102.1, -142.18) * mm, "end": v(101.35, -143.66) * mm});
            skLineSegment(sketch, "E952", {"start": v(101.35, -143.66) * mm, "end": v(100.49, -145.44) * mm});
            skLineSegment(sketch, "E953", {"start": v(100.49, -145.44) * mm, "end": v(99.5, -147.45) * mm});
            skLineSegment(sketch, "E954", {"start": v(99.5, -147.45) * mm, "end": v(98.4, -149.6) * mm});
            skLineSegment(sketch, "E955", {"start": v(98.4, -149.6) * mm, "end": v(97.18, -151.79) * mm});
            skLineSegment(sketch, "E956", {"start": v(97.18, -151.79) * mm, "end": v(95.83, -153.94) * mm});
            skLineSegment(sketch, "E957", {"start": v(95.83, -153.94) * mm, "end": v(94.34, -155.97) * mm});
            skLineSegment(sketch, "E958", {"start": v(94.34, -155.97) * mm, "end": v(91.57, -159.34) * mm});
            skLineSegment(sketch, "E959", {"start": v(91.57, -159.34) * mm, "end": v(89.55, -161.53) * mm});
            skLineSegment(sketch, "E960", {"start": v(89.55, -161.53) * mm, "end": v(87.98, -162.9) * mm});
            skLineSegment(sketch, "E961", {"start": v(87.98, -162.9) * mm, "end": v(86.54, -163.77) * mm});
            skLineSegment(sketch, "E962", {"start": v(86.54, -163.77) * mm, "end": v(84.92, -164.48) * mm});
            skLineSegment(sketch, "E963", {"start": v(84.92, -164.48) * mm, "end": v(82.8, -165.37) * mm});
            skLineSegment(sketch, "E964", {"start": v(82.8, -165.37) * mm, "end": v(79.85, -166.78) * mm});
            skLineSegment(sketch, "E965", {"start": v(79.85, -166.78) * mm, "end": v(75.78, -169.04) * mm});
            skLineSegment(sketch, "E966", {"start": v(75.78, -169.04) * mm, "end": v(75.51, -169.15) * mm});
            skLineSegment(sketch, "E967", {"start": v(75.51, -169.15) * mm, "end": v(75.2, -169.2) * mm});
            skLineSegment(sketch, "E968", {"start": v(75.2, -169.2) * mm, "end": v(74.87, -169.22) * mm});
            skLineSegment(sketch, "E969", {"start": v(74.87, -169.22) * mm, "end": v(74.52, -169.23) * mm});
            skLineSegment(sketch, "E970", {"start": v(74.52, -169.23) * mm, "end": v(74.15, -169.26) * mm});
            skLineSegment(sketch, "E971", {"start": v(74.15, -169.26) * mm, "end": v(73.78, -169.31) * mm});
            skLineSegment(sketch, "E972", {"start": v(73.78, -169.31) * mm, "end": v(73.42, -169.43) * mm});
            skLineSegment(sketch, "E973", {"start": v(73.42, -169.43) * mm, "end": v(73.08, -169.63) * mm});
            skLineSegment(sketch, "E974", {"start": v(98.45, -164.94) * mm, "end": v(98.94, -162.26) * mm});
            skLineSegment(sketch, "E975", {"start": v(98.94, -162.26) * mm, "end": v(99.08, -160.17) * mm});
            skLineSegment(sketch, "E976", {"start": v(99.08, -160.17) * mm, "end": v(99.04, -158.47) * mm});
            skLineSegment(sketch, "E977", {"start": v(99.04, -158.47) * mm, "end": v(99, -156.95) * mm});
            skLineSegment(sketch, "E978", {"start": v(99, -156.95) * mm, "end": v(99.14, -155.4) * mm});
            skLineSegment(sketch, "E979", {"start": v(99.14, -155.4) * mm, "end": v(99.63, -153.62) * mm});
            skLineSegment(sketch, "E980", {"start": v(99.63, -153.62) * mm, "end": v(100.65, -151.4) * mm});
            skLineSegment(sketch, "E981", {"start": v(100.65, -151.4) * mm, "end": v(102.37, -148.53) * mm});
            skLineSegment(sketch, "E982", {"start": v(102.37, -148.53) * mm, "end": v(102.58, -147.97) * mm});
            skLineSegment(sketch, "E983", {"start": v(102.58, -147.97) * mm, "end": v(102.7, -147.14) * mm});
            skLineSegment(sketch, "E984", {"start": v(102.7, -147.14) * mm, "end": v(102.73, -146.14) * mm});
            skLineSegment(sketch, "E985", {"start": v(102.73, -146.14) * mm, "end": v(102.72, -145.03) * mm});
            skLineSegment(sketch, "E986", {"start": v(102.72, -145.03) * mm, "end": v(102.7, -143.9) * mm});
            skLineSegment(sketch, "E987", {"start": v(102.7, -143.9) * mm, "end": v(102.67, -142.8) * mm});
            skLineSegment(sketch, "E988", {"start": v(102.67, -142.8) * mm, "end": v(102.69, -141.85) * mm});
            skLineSegment(sketch, "E989", {"start": v(102.69, -141.85) * mm, "end": v(102.76, -141.1) * mm});
            skLineSegment(sketch, "E990", {"start": v(-187.67, -4.26) * mm, "end": v(-187.2, -14.68) * mm});
            skLineSegment(sketch, "E991", {"start": v(-187.2, -14.68) * mm, "end": v(-185.85, -27.47) * mm});
            skLineSegment(sketch, "E992", {"start": v(-185.85, -27.47) * mm, "end": v(-183.75, -41.8) * mm});
            skLineSegment(sketch, "E993", {"start": v(-183.75, -41.8) * mm, "end": v(-181.04, -56.79) * mm});
            skLineSegment(sketch, "E994", {"start": v(-181.04, -56.79) * mm, "end": v(-177.84, -71.6) * mm});
            skLineSegment(sketch, "E995", {"start": v(-177.84, -71.6) * mm, "end": v(-174.27, -85.39) * mm});
            skLineSegment(sketch, "E996", {"start": v(-174.27, -85.39) * mm, "end": v(-170.46, -97.28) * mm});
            skLineSegment(sketch, "E997", {"start": v(-170.46, -97.28) * mm, "end": v(-166.53, -106.45) * mm});
            skLineSegment(sketch, "E998", {"start": v(-166.53, -106.45) * mm, "end": v(-164.1, -111.34) * mm});
            skLineSegment(sketch, "E999", {"start": v(-164.1, -111.34) * mm, "end": v(-161.66, -116.63) * mm});
            skLineSegment(sketch, "E1000", {"start": v(-161.66, -116.63) * mm, "end": v(-159.2, -122.15) * mm});
            skLineSegment(sketch, "E1001", {"start": v(-159.2, -122.15) * mm, "end": v(-156.7, -127.76) * mm});
            skLineSegment(sketch, "E1002", {"start": v(-156.7, -127.76) * mm, "end": v(-154.12, -133.3) * mm});
            skLineSegment(sketch, "E1003", {"start": v(-154.12, -133.3) * mm, "end": v(-151.48, -138.62) * mm});
            skLineSegment(sketch, "E1004", {"start": v(-151.48, -138.62) * mm, "end": v(-148.73, -143.56) * mm});
            skLineSegment(sketch, "E1005", {"start": v(-148.73, -143.56) * mm, "end": v(-145.86, -147.98) * mm});
            skLineSegment(sketch, "E1006", {"start": v(-145.86, -147.98) * mm, "end": v(-143.36, -151.68) * mm});
            skLineSegment(sketch, "E1007", {"start": v(-143.36, -151.68) * mm, "end": v(-141.64, -154.56) * mm});
            skLineSegment(sketch, "E1008", {"start": v(-141.64, -154.56) * mm, "end": v(-140.36, -156.9) * mm});
            skLineSegment(sketch, "E1009", {"start": v(-140.36, -156.9) * mm, "end": v(-139.17, -158.97) * mm});
            skLineSegment(sketch, "E1010", {"start": v(-139.17, -158.97) * mm, "end": v(-137.73, -161.05) * mm});
            skLineSegment(sketch, "E1011", {"start": v(-137.73, -161.05) * mm, "end": v(-135.7, -163.4) * mm});
            skLineSegment(sketch, "E1012", {"start": v(-135.7, -163.4) * mm, "end": v(-132.72, -166.32) * mm});
            skLineSegment(sketch, "E1013", {"start": v(-132.72, -166.32) * mm, "end": v(-128.48, -170.06) * mm});
            skLineSegment(sketch, "E1014", {"start": v(-128.48, -170.06) * mm, "end": v(-127, -171.53) * mm});
            skLineSegment(sketch, "E1015", {"start": v(-127, -171.53) * mm, "end": v(-125.63, -173.22) * mm});
            skLineSegment(sketch, "E1016", {"start": v(-125.63, -173.22) * mm, "end": v(-124.3, -175.05) * mm});
            skLineSegment(sketch, "E1017", {"start": v(-124.3, -175.05) * mm, "end": v(-122.94, -176.95) * mm});
            skLineSegment(sketch, "E1018", {"start": v(-122.94, -176.95) * mm, "end": v(-121.43, -178.85) * mm});
            skLineSegment(sketch, "E1019", {"start": v(-121.43, -178.85) * mm, "end": v(-119.71, -180.68) * mm});
            skLineSegment(sketch, "E1020", {"start": v(-119.71, -180.68) * mm, "end": v(-117.69, -182.35) * mm});
            skLineSegment(sketch, "E1021", {"start": v(-117.69, -182.35) * mm, "end": v(-115.28, -183.8) * mm});
            skLineSegment(sketch, "E1022", {"start": v(-115.28, -183.8) * mm, "end": v(-112.56, -185.62) * mm});
            skLineSegment(sketch, "E1023", {"start": v(-112.56, -185.62) * mm, "end": v(-108.25, -188.92) * mm});
            skLineSegment(sketch, "E1024", {"start": v(-108.25, -188.92) * mm, "end": v(-102.87, -193.24) * mm});
            skLineSegment(sketch, "E1025", {"start": v(-102.87, -193.24) * mm, "end": v(-96.87, -198.08) * mm});
            skLineSegment(sketch, "E1026", {"start": v(-96.87, -198.08) * mm, "end": v(-90.77, -202.94) * mm});
            skLineSegment(sketch, "E1027", {"start": v(-90.77, -202.94) * mm, "end": v(-85.04, -207.33) * mm});
            skLineSegment(sketch, "E1028", {"start": v(-85.04, -207.33) * mm, "end": v(-80.16, -210.76) * mm});
            skLineSegment(sketch, "E1029", {"start": v(-80.16, -210.76) * mm, "end": v(-76.63, -212.74) * mm});
            skLineSegment(sketch, "E1030", {"start": v(-76.63, -212.74) * mm, "end": v(-73.17, -214.25) * mm});
            skLineSegment(sketch, "E1031", {"start": v(-73.17, -214.25) * mm, "end": v(-70.74, -215.5) * mm});
            skLineSegment(sketch, "E1032", {"start": v(-70.74, -215.5) * mm, "end": v(-68.93, -216.5) * mm});
            skLineSegment(sketch, "E1033", {"start": v(-68.93, -216.5) * mm, "end": v(-67.37, -217.33) * mm});
            skLineSegment(sketch, "E1034", {"start": v(-67.37, -217.33) * mm, "end": v(-65.65, -218) * mm});
            skLineSegment(sketch, "E1035", {"start": v(-65.65, -218) * mm, "end": v(-63.38, -218.53) * mm});
            skLineSegment(sketch, "E1036", {"start": v(-63.38, -218.53) * mm, "end": v(-60.18, -219) * mm});
            skLineSegment(sketch, "E1037", {"start": v(-60.18, -219) * mm, "end": v(-55.65, -219.4) * mm});
            skLineSegment(sketch, "E1038", {"start": v(-55.65, -219.4) * mm, "end": v(-55.18, -219.6) * mm});
            skLineSegment(sketch, "E1039", {"start": v(-55.18, -219.6) * mm, "end": v(-53.92, -220.1) * mm});
            skLineSegment(sketch, "E1040", {"start": v(-53.92, -220.1) * mm, "end": v(-52.02, -220.83) * mm});
            skLineSegment(sketch, "E1041", {"start": v(-52.02, -220.83) * mm, "end": v(-49.6, -221.65) * mm});
            skLineSegment(sketch, "E1042", {"start": v(-49.6, -221.65) * mm, "end": v(-46.84, -222.45) * mm});
            skLineSegment(sketch, "E1043", {"start": v(-46.84, -222.45) * mm, "end": v(-43.85, -223.13) * mm});
            skLineSegment(sketch, "E1044", {"start": v(-43.85, -223.13) * mm, "end": v(-40.8, -223.57) * mm});
            skLineSegment(sketch, "E1045", {"start": v(-40.8, -223.57) * mm, "end": v(-37.8, -223.66) * mm});
            skLineSegment(sketch, "E1046", {"start": v(-37.8, -223.66) * mm, "end": v(-35.1, -223.8) * mm});
            skLineSegment(sketch, "E1047", {"start": v(-35.1, -223.8) * mm, "end": v(-31.66, -224.27) * mm});
            skLineSegment(sketch, "E1048", {"start": v(-31.66, -224.27) * mm, "end": v(-27.68, -224.9) * mm});
            skLineSegment(sketch, "E1049", {"start": v(-27.68, -224.9) * mm, "end": v(-23.32, -225.5) * mm});
            skLineSegment(sketch, "E1050", {"start": v(-23.32, -225.5) * mm, "end": v(-18.78, -225.92) * mm});
            skLineSegment(sketch, "E1051", {"start": v(-18.78, -225.92) * mm, "end": v(-14.23, -225.97) * mm});
            skLineSegment(sketch, "E1052", {"start": v(-14.23, -225.97) * mm, "end": v(-9.86, -225.47) * mm});
            skLineSegment(sketch, "E1053", {"start": v(-9.86, -225.47) * mm, "end": v(-5.85, -224.26) * mm});
            skLineSegment(sketch, "E1054", {"start": v(-5.85, -224.26) * mm, "end": v(-4.93, -224.15) * mm});
            skLineSegment(sketch, "E1055", {"start": v(-4.93, -224.15) * mm, "end": v(-2.5, -223.88) * mm});
            skLineSegment(sketch, "E1056", {"start": v(-2.5, -223.88) * mm, "end": v(1, -223.46) * mm});
            skLineSegment(sketch, "E1057", {"start": v(1, -223.46) * mm, "end": v(5.16, -222.93) * mm});
            skLineSegment(sketch, "E1058", {"start": v(5.16, -222.93) * mm, "end": v(9.56, -222.3) * mm});
            skLineSegment(sketch, "E1059", {"start": v(9.56, -222.3) * mm, "end": v(13.78, -221.58) * mm});
            skLineSegment(sketch, "E1060", {"start": v(13.78, -221.58) * mm, "end": v(17.4, -220.82) * mm});
            skLineSegment(sketch, "E1061", {"start": v(17.4, -220.82) * mm, "end": v(20, -220.03) * mm});
            skLineSegment(sketch, "E1062", {"start": v(20, -220.03) * mm, "end": v(22.37, -219.21) * mm});
            skLineSegment(sketch, "E1063", {"start": v(22.37, -219.21) * mm, "end": v(24.71, -218.67) * mm});
            skLineSegment(sketch, "E1064", {"start": v(24.71, -218.67) * mm, "end": v(27.11, -218.21) * mm});
            skLineSegment(sketch, "E1065", {"start": v(27.11, -218.21) * mm, "end": v(29.7, -217.68) * mm});
            skLineSegment(sketch, "E1066", {"start": v(29.7, -217.68) * mm, "end": v(32.57, -216.88) * mm});
            skLineSegment(sketch, "E1067", {"start": v(32.57, -216.88) * mm, "end": v(35.85, -215.65) * mm});
            skLineSegment(sketch, "E1068", {"start": v(35.85, -215.65) * mm, "end": v(39.65, -213.8) * mm});
            skLineSegment(sketch, "E1069", {"start": v(39.65, -213.8) * mm, "end": v(44.07, -211.17) * mm});
            skLineSegment(sketch, "E1070", {"start": v(44.07, -211.17) * mm, "end": v(51.12, -207.13) * mm});
            skLineSegment(sketch, "E1071", {"start": v(51.12, -207.13) * mm, "end": v(58.47, -203.6) * mm});
            skLineSegment(sketch, "E1072", {"start": v(58.47, -203.6) * mm, "end": v(65.94, -200.24) * mm});
            skLineSegment(sketch, "E1073", {"start": v(65.94, -200.24) * mm, "end": v(73.35, -196.7) * mm});
            skLineSegment(sketch, "E1074", {"start": v(73.35, -196.7) * mm, "end": v(80.53, -192.64) * mm});
            skLineSegment(sketch, "E1075", {"start": v(80.53, -192.64) * mm, "end": v(87.27, -187.7) * mm});
            skLineSegment(sketch, "E1076", {"start": v(87.27, -187.7) * mm, "end": v(93.41, -181.55) * mm});
            skLineSegment(sketch, "E1077", {"start": v(93.41, -181.55) * mm, "end": v(98.76, -173.82) * mm});
            skLineSegment(sketch, "E1078", {"start": v(98.76, -173.82) * mm, "end": v(99.17, -173.27) * mm});
            skLineSegment(sketch, "E1079", {"start": v(99.17, -173.27) * mm, "end": v(99.8, -172.57) * mm});
            skLineSegment(sketch, "E1080", {"start": v(99.8, -172.57) * mm, "end": v(100.59, -171.79) * mm});
            skLineSegment(sketch, "E1081", {"start": v(100.59, -171.79) * mm, "end": v(101.43, -170.96) * mm});
            skLineSegment(sketch, "E1082", {"start": v(101.43, -170.96) * mm, "end": v(102.24, -170.14) * mm});
            skLineSegment(sketch, "E1083", {"start": v(102.24, -170.14) * mm, "end": v(102.93, -169.38) * mm});
            skLineSegment(sketch, "E1084", {"start": v(102.93, -169.38) * mm, "end": v(103.42, -168.72) * mm});
            skLineSegment(sketch, "E1085", {"start": v(103.42, -168.72) * mm, "end": v(103.62, -168.22) * mm});
            skLineSegment(sketch, "E1086", {"start": v(-115.79, 96.76) * mm, "end": v(-106.48, 96.1) * mm});
            skLineSegment(sketch, "E1087", {"start": v(-106.48, 96.1) * mm, "end": v(-95.86, 96.31) * mm});
            skLineSegment(sketch, "E1088", {"start": v(-95.86, 96.31) * mm, "end": v(-84.32, 97.14) * mm});
            skLineSegment(sketch, "E1089", {"start": v(-84.32, 97.14) * mm, "end": v(-72.28, 98.32) * mm});
            skLineSegment(sketch, "E1090", {"start": v(-72.28, 98.32) * mm, "end": v(-60.17, 99.6) * mm});
            skLineSegment(sketch, "E1091", {"start": v(-60.17, 99.6) * mm, "end": v(-48.38, 100.72) * mm});
            skLineSegment(sketch, "E1092", {"start": v(-48.38, 100.72) * mm, "end": v(-37.34, 101.43) * mm});
            skLineSegment(sketch, "E1093", {"start": v(-37.34, 101.43) * mm, "end": v(-27.46, 101.46) * mm});
            skLineSegment(sketch, "E1094", {"start": v(-27.46, 101.46) * mm, "end": v(-24.86, 101.5) * mm});
            skLineSegment(sketch, "E1095", {"start": v(-24.86, 101.5) * mm, "end": v(-21, 101.73) * mm});
            skLineSegment(sketch, "E1096", {"start": v(-21, 101.73) * mm, "end": v(-16.26, 102.1) * mm});
            skLineSegment(sketch, "E1097", {"start": v(-16.26, 102.1) * mm, "end": v(-11.03, 102.55) * mm});
            skLineSegment(sketch, "E1098", {"start": v(-11.03, 102.55) * mm, "end": v(-5.67, 103) * mm});
            skLineSegment(sketch, "E1099", {"start": v(-5.67, 103) * mm, "end": v(-0.58, 103.4) * mm});
            skLineSegment(sketch, "E1100", {"start": v(-0.58, 103.4) * mm, "end": v(3.87, 103.7) * mm});
            skLineSegment(sketch, "E1101", {"start": v(3.87, 103.7) * mm, "end": v(7.3, 103.8) * mm});
            skLineSegment(sketch, "E1102", {"start": v(7.3, 103.8) * mm, "end": v(10.77, 103.82) * mm});
            skLineSegment(sketch, "E1103", {"start": v(10.77, 103.82) * mm, "end": v(14.48, 103.9) * mm});
            skLineSegment(sketch, "E1104", {"start": v(14.48, 103.9) * mm, "end": v(18.35, 104.03) * mm});
            skLineSegment(sketch, "E1105", {"start": v(18.35, 104.03) * mm, "end": v(22.28, 104.26) * mm});
            skLineSegment(sketch, "E1106", {"start": v(22.28, 104.26) * mm, "end": v(26.18, 104.6) * mm});
            skLineSegment(sketch, "E1107", {"start": v(26.18, 104.6) * mm, "end": v(29.96, 105.08) * mm});
            skLineSegment(sketch, "E1108", {"start": v(29.96, 105.08) * mm, "end": v(33.53, 105.7) * mm});
            skLineSegment(sketch, "E1109", {"start": v(33.53, 105.7) * mm, "end": v(36.78, 106.5) * mm});
            skLineSegment(sketch, "E1110", {"start": v(36.78, 106.5) * mm, "end": v(38.54, 106.74) * mm});
            skLineSegment(sketch, "E1111", {"start": v(38.54, 106.74) * mm, "end": v(41.29, 106.83) * mm});
            skLineSegment(sketch, "E1112", {"start": v(41.29, 106.83) * mm, "end": v(44.83, 106.84) * mm});
            skLineSegment(sketch, "E1113", {"start": v(44.83, 106.84) * mm, "end": v(48.97, 106.85) * mm});
            skLineSegment(sketch, "E1114", {"start": v(48.97, 106.85) * mm, "end": v(53.5, 106.95) * mm});
            skLineSegment(sketch, "E1115", {"start": v(53.5, 106.95) * mm, "end": v(58.2, 107.21) * mm});
            skLineSegment(sketch, "E1116", {"start": v(58.2, 107.21) * mm, "end": v(62.91, 107.72) * mm});
            skLineSegment(sketch, "E1117", {"start": v(62.91, 107.72) * mm, "end": v(67.4, 108.54) * mm});
            skLineSegment(sketch, "E1118", {"start": v(67.4, 108.54) * mm, "end": v(71.63, 109) * mm});
            skLineSegment(sketch, "E1119", {"start": v(71.63, 109) * mm, "end": v(78.54, 109.2) * mm});
            skLineSegment(sketch, "E1120", {"start": v(78.54, 109.2) * mm, "end": v(87.35, 109.24) * mm});
            skLineSegment(sketch, "E1121", {"start": v(87.35, 109.24) * mm, "end": v(97.29, 109.24) * mm});
            skLineSegment(sketch, "E1122", {"start": v(97.29, 109.24) * mm, "end": v(107.57, 109.3) * mm});
            skLineSegment(sketch, "E1123", {"start": v(107.57, 109.3) * mm, "end": v(117.42, 109.52) * mm});
            skLineSegment(sketch, "E1124", {"start": v(117.42, 109.52) * mm, "end": v(126.06, 110.02) * mm});
            skLineSegment(sketch, "E1125", {"start": v(126.06, 110.02) * mm, "end": v(132.7, 110.9) * mm});
            skLineSegment(sketch, "E1126", {"start": v(132.7, 110.9) * mm, "end": v(137.72, 111.47) * mm});
            skLineSegment(sketch, "E1127", {"start": v(137.72, 111.47) * mm, "end": v(144.91, 111.8) * mm});
            skLineSegment(sketch, "E1128", {"start": v(144.91, 111.8) * mm, "end": v(153.5, 112) * mm});
            skLineSegment(sketch, "E1129", {"start": v(153.5, 112) * mm, "end": v(162.71, 112.2) * mm});
            skLineSegment(sketch, "E1130", {"start": v(162.71, 112.2) * mm, "end": v(171.76, 112.53) * mm});
            skLineSegment(sketch, "E1131", {"start": v(171.76, 112.53) * mm, "end": v(179.88, 113.09) * mm});
            skLineSegment(sketch, "E1132", {"start": v(179.88, 113.09) * mm, "end": v(186.28, 114.01) * mm});
            skLineSegment(sketch, "E1133", {"start": v(186.28, 114.01) * mm, "end": v(190.19, 115.43) * mm});
            skLineSegment(sketch, "E1134", {"start": v(190.19, 115.43) * mm, "end": v(191.41, 115.61) * mm});
            skLineSegment(sketch, "E1135", {"start": v(191.41, 115.61) * mm, "end": v(194.3, 115.84) * mm});
            skLineSegment(sketch, "E1136", {"start": v(194.3, 115.84) * mm, "end": v(198.32, 116.1) * mm});
            skLineSegment(sketch, "E1137", {"start": v(198.32, 116.1) * mm, "end": v(202.93, 116.36) * mm});
            skLineSegment(sketch, "E1138", {"start": v(202.93, 116.36) * mm, "end": v(207.6, 116.6) * mm});
            skLineSegment(sketch, "E1139", {"start": v(207.6, 116.6) * mm, "end": v(211.78, 116.8) * mm});
            skLineSegment(sketch, "E1140", {"start": v(211.78, 116.8) * mm, "end": v(214.94, 116.92) * mm});
            skLineSegment(sketch, "E1141", {"start": v(214.94, 116.92) * mm, "end": v(216.54, 116.96) * mm});
            skLineSegment(sketch, "E1142", {"start": v(216.54, 116.96) * mm, "end": v(224.63, 116.87) * mm});
            skLineSegment(sketch, "E1143", {"start": v(224.63, 116.87) * mm, "end": v(233.29, 116.97) * mm});
            skLineSegment(sketch, "E1144", {"start": v(233.29, 116.97) * mm, "end": v(242.3, 117.22) * mm});
            skLineSegment(sketch, "E1145", {"start": v(242.3, 117.22) * mm, "end": v(251.52, 117.6) * mm});
            skLineSegment(sketch, "E1146", {"start": v(251.52, 117.6) * mm, "end": v(260.72, 118.07) * mm});
            skLineSegment(sketch, "E1147", {"start": v(260.72, 118.07) * mm, "end": v(269.73, 118.62) * mm});
            skLineSegment(sketch, "E1148", {"start": v(269.73, 118.62) * mm, "end": v(278.36, 119.21) * mm});
            skLineSegment(sketch, "E1149", {"start": v(278.36, 119.21) * mm, "end": v(286.42, 119.82) * mm});
            skLineSegment(sketch, "E1150", {"start": v(286.42, 119.82) * mm, "end": v(288.83, 119.93) * mm});
            skLineSegment(sketch, "E1151", {"start": v(288.83, 119.93) * mm, "end": v(291.32, 119.93) * mm});
            skLineSegment(sketch, "E1152", {"start": v(291.32, 119.93) * mm, "end": v(293.89, 119.9) * mm});
            skLineSegment(sketch, "E1153", {"start": v(293.89, 119.9) * mm, "end": v(296.48, 119.89) * mm});
            skLineSegment(sketch, "E1154", {"start": v(296.48, 119.89) * mm, "end": v(299.08, 119.98) * mm});
            skLineSegment(sketch, "E1155", {"start": v(299.08, 119.98) * mm, "end": v(301.65, 120.24) * mm});
            skLineSegment(sketch, "E1156", {"start": v(301.65, 120.24) * mm, "end": v(304.16, 120.74) * mm});
            skLineSegment(sketch, "E1157", {"start": v(304.16, 120.74) * mm, "end": v(306.58, 121.54) * mm});
            skLineSegment(sketch, "E1158", {"start": v(306.58, 121.54) * mm, "end": v(307.26, 121.64) * mm});
            skLineSegment(sketch, "E1159", {"start": v(307.26, 121.64) * mm, "end": v(308.53, 121.7) * mm});
            skLineSegment(sketch, "E1160", {"start": v(308.53, 121.7) * mm, "end": v(310.22, 121.72) * mm});
            skLineSegment(sketch, "E1161", {"start": v(310.22, 121.72) * mm, "end": v(312.14, 121.72) * mm});
            skLineSegment(sketch, "E1162", {"start": v(312.14, 121.72) * mm, "end": v(314.1, 121.7) * mm});
            skLineSegment(sketch, "E1163", {"start": v(314.1, 121.7) * mm, "end": v(315.9, 121.69) * mm});
            skLineSegment(sketch, "E1164", {"start": v(315.9, 121.69) * mm, "end": v(317.38, 121.67) * mm});
            skLineSegment(sketch, "E1165", {"start": v(317.38, 121.67) * mm, "end": v(318.33, 121.66) * mm});
            skLineSegment(sketch, "E1166", {"start": v(318.33, 121.66) * mm, "end": v(316.98, 124.34) * mm});
            skLineSegment(sketch, "E1167", {"start": v(316.98, 124.34) * mm, "end": v(313.56, 128.3) * mm});
            skLineSegment(sketch, "E1168", {"start": v(313.56, 128.3) * mm, "end": v(309, 133.05) * mm});
            skLineSegment(sketch, "E1169", {"start": v(309, 133.05) * mm, "end": v(304.23, 138.12) * mm});
            skLineSegment(sketch, "E1170", {"start": v(304.23, 138.12) * mm, "end": v(300.2, 143.05) * mm});
            skLineSegment(sketch, "E1171", {"start": v(300.2, 143.05) * mm, "end": v(297.84, 147.36) * mm});
            skLineSegment(sketch, "E1172", {"start": v(297.84, 147.36) * mm, "end": v(298.09, 150.58) * mm});
            skLineSegment(sketch, "E1173", {"start": v(298.09, 150.58) * mm, "end": v(301.89, 152.24) * mm});
            skLineSegment(sketch, "E1174", {"start": v(301.89, 152.24) * mm, "end": v(306.58, 152.46) * mm});
            skLineSegment(sketch, "E1175", {"start": v(306.58, 152.46) * mm, "end": v(312.93, 152.26) * mm});
            skLineSegment(sketch, "E1176", {"start": v(312.93, 152.26) * mm, "end": v(320.35, 151.7) * mm});
            skLineSegment(sketch, "E1177", {"start": v(320.35, 151.7) * mm, "end": v(328.25, 150.82) * mm});
            skLineSegment(sketch, "E1178", {"start": v(328.25, 150.82) * mm, "end": v(336.03, 149.69) * mm});
            skLineSegment(sketch, "E1179", {"start": v(336.03, 149.69) * mm, "end": v(343.1, 148.35) * mm});
            skLineSegment(sketch, "E1180", {"start": v(343.1, 148.35) * mm, "end": v(348.87, 146.86) * mm});
            skLineSegment(sketch, "E1181", {"start": v(348.87, 146.86) * mm, "end": v(352.75, 145.27) * mm});
            skLineSegment(sketch, "E1182", {"start": v(352.75, 145.27) * mm, "end": v(355.03, 144.61) * mm});
            skLineSegment(sketch, "E1183", {"start": v(355.03, 144.61) * mm, "end": v(360.28, 143.33) * mm});
            skLineSegment(sketch, "E1184", {"start": v(360.28, 143.33) * mm, "end": v(367.53, 141.64) * mm});
            skLineSegment(sketch, "E1185", {"start": v(367.53, 141.64) * mm, "end": v(375.8, 139.77) * mm});
            skLineSegment(sketch, "E1186", {"start": v(375.8, 139.77) * mm, "end": v(384.1, 137.93) * mm});
            skLineSegment(sketch, "E1187", {"start": v(384.1, 137.93) * mm, "end": v(391.45, 136.35) * mm});
            skLineSegment(sketch, "E1188", {"start": v(391.45, 136.35) * mm, "end": v(396.87, 135.23) * mm});
            skLineSegment(sketch, "E1189", {"start": v(396.87, 135.23) * mm, "end": v(399.38, 134.81) * mm});
            skLineSegment(sketch, "E1190", {"start": v(399.38, 134.81) * mm, "end": v(405.32, 134.32) * mm});
            skLineSegment(sketch, "E1191", {"start": v(405.32, 134.32) * mm, "end": v(412.27, 133) * mm});
            skLineSegment(sketch, "E1192", {"start": v(412.27, 133) * mm, "end": v(419.8, 131.16) * mm});
            skLineSegment(sketch, "E1193", {"start": v(419.8, 131.16) * mm, "end": v(427.5, 129.05) * mm});
            skLineSegment(sketch, "E1194", {"start": v(427.5, 129.05) * mm, "end": v(434.92, 126.96) * mm});
            skLineSegment(sketch, "E1195", {"start": v(434.92, 126.96) * mm, "end": v(441.64, 125.16) * mm});
            skLineSegment(sketch, "E1196", {"start": v(441.64, 125.16) * mm, "end": v(447.24, 123.93) * mm});
            skLineSegment(sketch, "E1197", {"start": v(447.24, 123.93) * mm, "end": v(451.3, 123.54) * mm});
            skLineSegment(sketch, "E1198", {"start": v(451.3, 123.54) * mm, "end": v(451.68, 123.55) * mm});
            skLineSegment(sketch, "E1199", {"start": v(451.68, 123.55) * mm, "end": v(451.91, 123.54) * mm});
            skLineSegment(sketch, "E1200", {"start": v(451.91, 123.54) * mm, "end": v(452.03, 123.51) * mm});
            skLineSegment(sketch, "E1201", {"start": v(452.03, 123.51) * mm, "end": v(452.08, 123.46) * mm});
            skLineSegment(sketch, "E1202", {"start": v(452.08, 123.46) * mm, "end": v(452.12, 123.4) * mm});
            skLineSegment(sketch, "E1203", {"start": v(452.12, 123.4) * mm, "end": v(452.2, 123.3) * mm});
            skLineSegment(sketch, "E1204", {"start": v(452.2, 123.3) * mm, "end": v(452.38, 123.2) * mm});
            skLineSegment(sketch, "E1205", {"start": v(452.38, 123.2) * mm, "end": v(452.7, 123.07) * mm});
            skLineSegment(sketch, "E1206", {"start": v(-84.78, 41.32) * mm, "end": v(-76.98, 43.6) * mm});
            skLineSegment(sketch, "E1207", {"start": v(-76.98, 43.6) * mm, "end": v(-69.26, 44.77) * mm});
            skLineSegment(sketch, "E1208", {"start": v(-69.26, 44.77) * mm, "end": v(-61.64, 45.15) * mm});
            skLineSegment(sketch, "E1209", {"start": v(-61.64, 45.15) * mm, "end": v(-54.11, 45.07) * mm});
            skLineSegment(sketch, "E1210", {"start": v(-54.11, 45.07) * mm, "end": v(-46.67, 44.87) * mm});
            skLineSegment(sketch, "E1211", {"start": v(-46.67, 44.87) * mm, "end": v(-39.3, 44.87) * mm});
            skLineSegment(sketch, "E1212", {"start": v(-39.3, 44.87) * mm, "end": v(-32.02, 45.42) * mm});
            skLineSegment(sketch, "E1213", {"start": v(-32.02, 45.42) * mm, "end": v(-24.8, 46.84) * mm});
            skLineSegment(sketch, "E1214", {"start": v(-24.8, 46.84) * mm, "end": v(-21.58, 47.48) * mm});
            skLineSegment(sketch, "E1215", {"start": v(-21.58, 47.48) * mm, "end": v(-17.2, 48.03) * mm});
            skLineSegment(sketch, "E1216", {"start": v(-17.2, 48.03) * mm, "end": v(-11.99, 48.52) * mm});
            skLineSegment(sketch, "E1217", {"start": v(-11.99, 48.52) * mm, "end": v(-6.22, 49) * mm});
            skLineSegment(sketch, "E1218", {"start": v(-6.22, 49) * mm, "end": v(-0.2, 49.51) * mm});
            skLineSegment(sketch, "E1219", {"start": v(-0.2, 49.51) * mm, "end": v(5.75, 50.08) * mm});
            skLineSegment(sketch, "E1220", {"start": v(5.75, 50.08) * mm, "end": v(11.34, 50.74) * mm});
            skLineSegment(sketch, "E1221", {"start": v(11.34, 50.74) * mm, "end": v(16.27, 51.53) * mm});
            skLineSegment(sketch, "E1222", {"start": v(16.27, 51.53) * mm, "end": v(21.14, 52.25) * mm});
            skLineSegment(sketch, "E1223", {"start": v(21.14, 52.25) * mm, "end": v(27.46, 52.9) * mm});
            skLineSegment(sketch, "E1224", {"start": v(27.46, 52.9) * mm, "end": v(34.72, 53.53) * mm});
            skLineSegment(sketch, "E1225", {"start": v(34.72, 53.53) * mm, "end": v(42.42, 54.19) * mm});
            skLineSegment(sketch, "E1226", {"start": v(42.42, 54.19) * mm, "end": v(50.04, 54.92) * mm});
            skLineSegment(sketch, "E1227", {"start": v(50.04, 54.92) * mm, "end": v(57.1, 55.79) * mm});
            skLineSegment(sketch, "E1228", {"start": v(57.1, 55.79) * mm, "end": v(63.06, 56.83) * mm});
            skLineSegment(sketch, "E1229", {"start": v(63.06, 56.83) * mm, "end": v(67.44, 58.11) * mm});
            skLineSegment(sketch, "E1230", {"start": v(67.44, 58.11) * mm, "end": v(70.42, 58.66) * mm});
            skLineSegment(sketch, "E1231", {"start": v(70.42, 58.66) * mm, "end": v(74.8, 58.7) * mm});
            skLineSegment(sketch, "E1232", {"start": v(74.8, 58.7) * mm, "end": v(80.24, 58.4) * mm});
            skLineSegment(sketch, "E1233", {"start": v(80.24, 58.4) * mm, "end": v(86.35, 58.04) * mm});
            skLineSegment(sketch, "E1234", {"start": v(86.35, 58.04) * mm, "end": v(92.76, 57.8) * mm});
            skLineSegment(sketch, "E1235", {"start": v(92.76, 57.8) * mm, "end": v(99.12, 57.89) * mm});
            skLineSegment(sketch, "E1236", {"start": v(99.12, 57.89) * mm, "end": v(105.05, 58.55) * mm});
            skLineSegment(sketch, "E1237", {"start": v(105.05, 58.55) * mm, "end": v(110.2, 60) * mm});
            skLineSegment(sketch, "E1238", {"start": v(110.2, 60) * mm, "end": v(111.98, 60.08) * mm});
            skLineSegment(sketch, "E1239", {"start": v(111.98, 60.08) * mm, "end": v(116.48, 60.22) * mm});
            skLineSegment(sketch, "E1240", {"start": v(116.48, 60.22) * mm, "end": v(122.87, 60.4) * mm});
            skLineSegment(sketch, "E1241", {"start": v(122.87, 60.4) * mm, "end": v(130.32, 60.6) * mm});
            skLineSegment(sketch, "E1242", {"start": v(130.32, 60.6) * mm, "end": v(138.02, 60.83) * mm});
            skLineSegment(sketch, "E1243", {"start": v(138.02, 60.83) * mm, "end": v(145.14, 61.07) * mm});
            skLineSegment(sketch, "E1244", {"start": v(145.14, 61.07) * mm, "end": v(150.86, 61.32) * mm});
            skLineSegment(sketch, "E1245", {"start": v(150.86, 61.32) * mm, "end": v(154.36, 61.56) * mm});
            skLineSegment(sketch, "E1246", {"start": v(154.36, 61.56) * mm, "end": v(157.87, 61.9) * mm});
            skLineSegment(sketch, "E1247", {"start": v(157.87, 61.9) * mm, "end": v(160.1, 62.04) * mm});
            skLineSegment(sketch, "E1248", {"start": v(160.1, 62.04) * mm, "end": v(161.5, 62.06) * mm});
            skLineSegment(sketch, "E1249", {"start": v(161.5, 62.06) * mm, "end": v(162.51, 62.08) * mm});
            skLineSegment(sketch, "E1250", {"start": v(162.51, 62.08) * mm, "end": v(163.58, 62.2) * mm});
            skLineSegment(sketch, "E1251", {"start": v(163.58, 62.2) * mm, "end": v(165.15, 62.52) * mm});
            skLineSegment(sketch, "E1252", {"start": v(165.15, 62.52) * mm, "end": v(167.67, 63.16) * mm});
            skLineSegment(sketch, "E1253", {"start": v(167.67, 63.16) * mm, "end": v(171.58, 64.22) * mm});
            skLineSegment(sketch, "E1254", {"start": v(171.58, 64.22) * mm, "end": v(173.6, 64.58) * mm});
            skLineSegment(sketch, "E1255", {"start": v(173.6, 64.58) * mm, "end": v(175.5, 64.62) * mm});
            skLineSegment(sketch, "E1256", {"start": v(175.5, 64.62) * mm, "end": v(177.42, 64.5) * mm});
            skLineSegment(sketch, "E1257", {"start": v(177.42, 64.5) * mm, "end": v(179.45, 64.34) * mm});
            skLineSegment(sketch, "E1258", {"start": v(179.45, 64.34) * mm, "end": v(181.71, 64.32) * mm});
            skLineSegment(sketch, "E1259", {"start": v(181.71, 64.32) * mm, "end": v(184.32, 64.58) * mm});
            skLineSegment(sketch, "E1260", {"start": v(184.32, 64.58) * mm, "end": v(187.38, 65.28) * mm});
            skLineSegment(sketch, "E1261", {"start": v(187.38, 65.28) * mm, "end": v(191, 66.57) * mm});
            skLineSegment(sketch, "E1262", {"start": v(191, 66.57) * mm, "end": v(194.14, 67.13) * mm});
            skLineSegment(sketch, "E1263", {"start": v(194.14, 67.13) * mm, "end": v(199.57, 67.45) * mm});
            skLineSegment(sketch, "E1264", {"start": v(199.57, 67.45) * mm, "end": v(206.63, 67.66) * mm});
            skLineSegment(sketch, "E1265", {"start": v(206.63, 67.66) * mm, "end": v(214.7, 67.9) * mm});
            skLineSegment(sketch, "E1266", {"start": v(214.7, 67.9) * mm, "end": v(223.11, 68.28) * mm});
            skLineSegment(sketch, "E1267", {"start": v(223.11, 68.28) * mm, "end": v(231.24, 68.96) * mm});
            skLineSegment(sketch, "E1268", {"start": v(231.24, 68.96) * mm, "end": v(238.44, 70.07) * mm});
            skLineSegment(sketch, "E1269", {"start": v(238.44, 70.07) * mm, "end": v(244.06, 71.74) * mm});
            skLineSegment(sketch, "E1270", {"start": v(244.06, 71.74) * mm, "end": v(245.82, 71.81) * mm});
            skLineSegment(sketch, "E1271", {"start": v(245.82, 71.81) * mm, "end": v(250.4, 71.98) * mm});
            skLineSegment(sketch, "E1272", {"start": v(250.4, 71.98) * mm, "end": v(257, 72.26) * mm});
            skLineSegment(sketch, "E1273", {"start": v(257, 72.26) * mm, "end": v(264.74, 72.66) * mm});
            skLineSegment(sketch, "E1274", {"start": v(264.74, 72.66) * mm, "end": v(272.8, 73.17) * mm});
            skLineSegment(sketch, "E1275", {"start": v(272.8, 73.17) * mm, "end": v(280.36, 73.8) * mm});
            skLineSegment(sketch, "E1276", {"start": v(280.36, 73.8) * mm, "end": v(286.58, 74.58) * mm});
            skLineSegment(sketch, "E1277", {"start": v(286.58, 74.58) * mm, "end": v(290.61, 75.5) * mm});
            skLineSegment(sketch, "E1278", {"start": v(290.61, 75.5) * mm, "end": v(292.48, 75.58) * mm});
            skLineSegment(sketch, "E1279", {"start": v(292.48, 75.58) * mm, "end": v(297.35, 75.76) * mm});
            skLineSegment(sketch, "E1280", {"start": v(297.35, 75.76) * mm, "end": v(304.26, 76) * mm});
            skLineSegment(sketch, "E1281", {"start": v(304.26, 76) * mm, "end": v(312.29, 76.28) * mm});
            skLineSegment(sketch, "E1282", {"start": v(312.29, 76.28) * mm, "end": v(320.48, 76.56) * mm});
            skLineSegment(sketch, "E1283", {"start": v(320.48, 76.56) * mm, "end": v(327.9, 76.8) * mm});
            skLineSegment(sketch, "E1284", {"start": v(327.9, 76.8) * mm, "end": v(333.6, 76.96) * mm});
            skLineSegment(sketch, "E1285", {"start": v(333.6, 76.96) * mm, "end": v(336.65, 77.02) * mm});
            skLineSegment(sketch, "E1286", {"start": v(336.65, 77.02) * mm, "end": v(337.92, 76.78) * mm});
            skLineSegment(sketch, "E1287", {"start": v(337.92, 76.78) * mm, "end": v(338.95, 76.05) * mm});
            skLineSegment(sketch, "E1288", {"start": v(338.95, 76.05) * mm, "end": v(339.65, 74.97) * mm});
            skLineSegment(sketch, "E1289", {"start": v(339.65, 74.97) * mm, "end": v(339.9, 73.65) * mm});
            skLineSegment(sketch, "E1290", {"start": v(339.9, 73.65) * mm, "end": v(339.6, 72.22) * mm});
            skLineSegment(sketch, "E1291", {"start": v(339.6, 72.22) * mm, "end": v(338.65, 70.82) * mm});
            skLineSegment(sketch, "E1292", {"start": v(338.65, 70.82) * mm, "end": v(336.93, 69.56) * mm});
            skLineSegment(sketch, "E1293", {"start": v(336.93, 69.56) * mm, "end": v(334.34, 68.57) * mm});
            skLineSegment(sketch, "E1294", {"start": v(334.34, 68.57) * mm, "end": v(333.28, 67.58) * mm});
            skLineSegment(sketch, "E1295", {"start": v(333.28, 67.58) * mm, "end": v(330.8, 65.06) * mm});
            skLineSegment(sketch, "E1296", {"start": v(330.8, 65.06) * mm, "end": v(327.38, 61.46) * mm});
            skLineSegment(sketch, "E1297", {"start": v(327.38, 61.46) * mm, "end": v(323.51, 57.27) * mm});
            skLineSegment(sketch, "E1298", {"start": v(323.51, 57.27) * mm, "end": v(319.68, 52.97) * mm});
            skLineSegment(sketch, "E1299", {"start": v(319.68, 52.97) * mm, "end": v(316.35, 49.03) * mm});
            skLineSegment(sketch, "E1300", {"start": v(316.35, 49.03) * mm, "end": v(314.02, 45.93) * mm});
            skLineSegment(sketch, "E1301", {"start": v(314.02, 45.93) * mm, "end": v(313.16, 44.14) * mm});
            skLineSegment(sketch, "E1302", {"start": v(313.16, 44.14) * mm, "end": v(313.35, 41.9) * mm});
            skLineSegment(sketch, "E1303", {"start": v(313.35, 41.9) * mm, "end": v(313.75, 40.43) * mm});
            skLineSegment(sketch, "E1304", {"start": v(313.75, 40.43) * mm, "end": v(314.45, 39.55) * mm});
            skLineSegment(sketch, "E1305", {"start": v(314.45, 39.55) * mm, "end": v(315.55, 39.14) * mm});
            skLineSegment(sketch, "E1306", {"start": v(315.55, 39.14) * mm, "end": v(317.15, 39.06) * mm});
            skLineSegment(sketch, "E1307", {"start": v(317.15, 39.06) * mm, "end": v(319.33, 39.18) * mm});
            skLineSegment(sketch, "E1308", {"start": v(319.33, 39.18) * mm, "end": v(322.2, 39.35) * mm});
            skLineSegment(sketch, "E1309", {"start": v(322.2, 39.35) * mm, "end": v(325.85, 39.44) * mm});
            skLineSegment(sketch, "E1310", {"start": v(325.85, 39.44) * mm, "end": v(329.96, 40.44) * mm});
            skLineSegment(sketch, "E1311", {"start": v(329.96, 40.44) * mm, "end": v(337.93, 43.12) * mm});
            skLineSegment(sketch, "E1312", {"start": v(337.93, 43.12) * mm, "end": v(348.6, 46.97) * mm});
            skLineSegment(sketch, "E1313", {"start": v(348.6, 46.97) * mm, "end": v(360.8, 51.52) * mm});
            skLineSegment(sketch, "E1314", {"start": v(360.8, 51.52) * mm, "end": v(373.33, 56.27) * mm});
            skLineSegment(sketch, "E1315", {"start": v(373.33, 56.27) * mm, "end": v(385.03, 60.73) * mm});
            skLineSegment(sketch, "E1316", {"start": v(385.03, 60.73) * mm, "end": v(394.74, 64.4) * mm});
            skLineSegment(sketch, "E1317", {"start": v(394.74, 64.4) * mm, "end": v(401.26, 66.8) * mm});
            skLineSegment(sketch, "E1318", {"start": v(401.26, 66.8) * mm, "end": v(405.56, 68.6) * mm});
            skLineSegment(sketch, "E1319", {"start": v(405.56, 68.6) * mm, "end": v(412.03, 71.63) * mm});
            skLineSegment(sketch, "E1320", {"start": v(412.03, 71.63) * mm, "end": v(419.9, 75.42) * mm});
            skLineSegment(sketch, "E1321", {"start": v(419.9, 75.42) * mm, "end": v(428.39, 79.53) * mm});
            skLineSegment(sketch, "E1322", {"start": v(428.39, 79.53) * mm, "end": v(436.7, 83.51) * mm});
            skLineSegment(sketch, "E1323", {"start": v(436.7, 83.51) * mm, "end": v(444.04, 86.92) * mm});
            skLineSegment(sketch, "E1324", {"start": v(444.04, 86.92) * mm, "end": v(449.64, 89.29) * mm});
            skLineSegment(sketch, "E1325", {"start": v(449.64, 89.29) * mm, "end": v(452.7, 90.18) * mm});
            skLineSegment(sketch, "E1326", {"start": v(452.7, 90.18) * mm, "end": v(453.76, 90.58) * mm});
            skLineSegment(sketch, "E1327", {"start": v(453.76, 90.58) * mm, "end": v(456.51, 91.57) * mm});
            skLineSegment(sketch, "E1328", {"start": v(456.51, 91.57) * mm, "end": v(460.45, 93) * mm});
            skLineSegment(sketch, "E1329", {"start": v(460.45, 93) * mm, "end": v(465.1, 94.7) * mm});
            skLineSegment(sketch, "E1330", {"start": v(465.1, 94.7) * mm, "end": v(469.96, 96.54) * mm});
            skLineSegment(sketch, "E1331", {"start": v(469.96, 96.54) * mm, "end": v(474.56, 98.35) * mm});
            skLineSegment(sketch, "E1332", {"start": v(474.56, 98.35) * mm, "end": v(478.39, 100) * mm});
            skLineSegment(sketch, "E1333", {"start": v(478.39, 100) * mm, "end": v(480.97, 101.3) * mm});
            skLineSegment(sketch, "E1334", {"start": v(480.97, 101.3) * mm, "end": v(482.43, 101.9) * mm});
            skLineSegment(sketch, "E1335", {"start": v(482.43, 101.9) * mm, "end": v(484.72, 102.67) * mm});
            skLineSegment(sketch, "E1336", {"start": v(484.72, 102.67) * mm, "end": v(487.33, 103.64) * mm});
            skLineSegment(sketch, "E1337", {"start": v(487.33, 103.64) * mm, "end": v(489.76, 104.84) * mm});
            skLineSegment(sketch, "E1338", {"start": v(489.76, 104.84) * mm, "end": v(491.53, 106.3) * mm});
            skLineSegment(sketch, "E1339", {"start": v(491.53, 106.3) * mm, "end": v(492.12, 108.06) * mm});
            skLineSegment(sketch, "E1340", {"start": v(492.12, 108.06) * mm, "end": v(491.05, 110.15) * mm});
            skLineSegment(sketch, "E1341", {"start": v(491.05, 110.15) * mm, "end": v(487.82, 112.61) * mm});
            skLineSegment(sketch, "E1342", {"start": v(487.82, 112.61) * mm, "end": v(487.2, 112.66) * mm});
            skLineSegment(sketch, "E1343", {"start": v(487.2, 112.66) * mm, "end": v(485.6, 112.79) * mm});
            skLineSegment(sketch, "E1344", {"start": v(485.6, 112.79) * mm, "end": v(483.25, 113.04) * mm});
            skLineSegment(sketch, "E1345", {"start": v(483.25, 113.04) * mm, "end": v(480.45, 113.45) * mm});
            skLineSegment(sketch, "E1346", {"start": v(480.45, 113.45) * mm, "end": v(477.45, 114.04) * mm});
            skLineSegment(sketch, "E1347", {"start": v(477.45, 114.04) * mm, "end": v(474.51, 114.86) * mm});
            skLineSegment(sketch, "E1348", {"start": v(474.51, 114.86) * mm, "end": v(471.92, 115.94) * mm});
            skLineSegment(sketch, "E1349", {"start": v(471.92, 115.94) * mm, "end": v(469.92, 117.3) * mm});
            skLineSegment(sketch, "E1350", {"start": v(469.92, 117.3) * mm, "end": v(468.53, 118.38) * mm});
            skLineSegment(sketch, "E1351", {"start": v(468.53, 118.38) * mm, "end": v(466.68, 119.41) * mm});
            skLineSegment(sketch, "E1352", {"start": v(466.68, 119.41) * mm, "end": v(464.5, 120.38) * mm});
            skLineSegment(sketch, "E1353", {"start": v(464.5, 120.38) * mm, "end": v(462.16, 121.26) * mm});
            skLineSegment(sketch, "E1354", {"start": v(462.16, 121.26) * mm, "end": v(459.76, 122) * mm});
            skLineSegment(sketch, "E1355", {"start": v(459.76, 122) * mm, "end": v(457.45, 122.57) * mm});
            skLineSegment(sketch, "E1356", {"start": v(457.45, 122.57) * mm, "end": v(455.36, 122.94) * mm});
            skLineSegment(sketch, "E1357", {"start": v(455.36, 122.94) * mm, "end": v(453.64, 123.07) * mm});
            skLineSegment(sketch, "E1358", {"start": v(353.57, 88.77) * mm, "end": v(352.21, 87.4) * mm});
            skLineSegment(sketch, "E1359", {"start": v(352.21, 87.4) * mm, "end": v(350.22, 84.36) * mm});
            skLineSegment(sketch, "E1360", {"start": v(350.22, 84.36) * mm, "end": v(347.8, 80.17) * mm});
            skLineSegment(sketch, "E1361", {"start": v(347.8, 80.17) * mm, "end": v(345.2, 75.4) * mm});
            skLineSegment(sketch, "E1362", {"start": v(345.2, 75.4) * mm, "end": v(342.66, 70.6) * mm});
            skLineSegment(sketch, "E1363", {"start": v(342.66, 70.6) * mm, "end": v(340.39, 66.34) * mm});
            skLineSegment(sketch, "E1364", {"start": v(340.39, 66.34) * mm, "end": v(338.62, 63.17) * mm});
            skLineSegment(sketch, "E1365", {"start": v(338.62, 63.17) * mm, "end": v(337.6, 61.64) * mm});
            skLineSegment(sketch, "E1366", {"start": v(337.6, 61.64) * mm, "end": v(335.56, 59.65) * mm});
            skLineSegment(sketch, "E1367", {"start": v(335.56, 59.65) * mm, "end": v(335.76, 59.37) * mm});
            skLineSegment(sketch, "E1368", {"start": v(335.76, 59.37) * mm, "end": v(337.58, 60.37) * mm});
            skLineSegment(sketch, "E1369", {"start": v(337.58, 60.37) * mm, "end": v(340.42, 62.21) * mm});
            skLineSegment(sketch, "E1370", {"start": v(340.42, 62.21) * mm, "end": v(343.7, 64.44) * mm});
            skLineSegment(sketch, "E1371", {"start": v(343.7, 64.44) * mm, "end": v(346.82, 66.62) * mm});
            skLineSegment(sketch, "E1372", {"start": v(346.82, 66.62) * mm, "end": v(349.17, 68.3) * mm});
            skLineSegment(sketch, "E1373", {"start": v(349.17, 68.3) * mm, "end": v(350.16, 69.04) * mm});
            skLineSegment(sketch, "E1374", {"start": v(350.16, 69.04) * mm, "end": v(354.37, 73.15) * mm});
            skLineSegment(sketch, "E1375", {"start": v(354.37, 73.15) * mm, "end": v(358.73, 76.6) * mm});
            skLineSegment(sketch, "E1376", {"start": v(358.73, 76.6) * mm, "end": v(363.1, 79.58) * mm});
            skLineSegment(sketch, "E1377", {"start": v(363.1, 79.58) * mm, "end": v(367.32, 82.35) * mm});
            skLineSegment(sketch, "E1378", {"start": v(367.32, 82.35) * mm, "end": v(371.22, 85.12) * mm});
            skLineSegment(sketch, "E1379", {"start": v(371.22, 85.12) * mm, "end": v(374.65, 88.12) * mm});
            skLineSegment(sketch, "E1380", {"start": v(374.65, 88.12) * mm, "end": v(377.46, 91.59) * mm});
            skLineSegment(sketch, "E1381", {"start": v(377.46, 91.59) * mm, "end": v(379.49, 95.74) * mm});
            skLineSegment(sketch, "E1382", {"start": v(379.49, 95.74) * mm, "end": v(385.24, 97.43) * mm});
            skLineSegment(sketch, "E1383", {"start": v(385.24, 97.43) * mm, "end": v(388.1, 99.37) * mm});
            skLineSegment(sketch, "E1384", {"start": v(388.1, 99.37) * mm, "end": v(388.7, 101.44) * mm});
            skLineSegment(sketch, "E1385", {"start": v(388.7, 101.44) * mm, "end": v(387.66, 103.53) * mm});
            skLineSegment(sketch, "E1386", {"start": v(387.66, 103.53) * mm, "end": v(385.6, 105.52) * mm});
            skLineSegment(sketch, "E1387", {"start": v(385.6, 105.52) * mm, "end": v(383.18, 107.3) * mm});
            skLineSegment(sketch, "E1388", {"start": v(383.18, 107.3) * mm, "end": v(381, 108.74) * mm});
            skLineSegment(sketch, "E1389", {"start": v(381, 108.74) * mm, "end": v(379.72, 109.75) * mm});
            skLineSegment(sketch, "E1390", {"start": v(379.72, 109.75) * mm, "end": v(374.96, 113.79) * mm});
            skLineSegment(sketch, "E1391", {"start": v(374.96, 113.79) * mm, "end": v(367.74, 118.13) * mm});
            skLineSegment(sketch, "E1392", {"start": v(367.74, 118.13) * mm, "end": v(358.85, 122.66) * mm});
            skLineSegment(sketch, "E1393", {"start": v(358.85, 122.66) * mm, "end": v(349.04, 127.26) * mm});
            skLineSegment(sketch, "E1394", {"start": v(349.04, 127.26) * mm, "end": v(339.08, 131.84) * mm});
            skLineSegment(sketch, "E1395", {"start": v(339.08, 131.84) * mm, "end": v(329.74, 136.26) * mm});
            skLineSegment(sketch, "E1396", {"start": v(329.74, 136.26) * mm, "end": v(321.78, 140.42) * mm});
            skLineSegment(sketch, "E1397", {"start": v(321.78, 140.42) * mm, "end": v(315.98, 144.21) * mm});
            skLineSegment(sketch, "E1398", {"start": v(315.98, 144.21) * mm, "end": v(319.03, 141.67) * mm});
            skLineSegment(sketch, "E1399", {"start": v(319.03, 141.67) * mm, "end": v(321.23, 139.33) * mm});
            skLineSegment(sketch, "E1400", {"start": v(321.23, 139.33) * mm, "end": v(322.9, 137.14) * mm});
            skLineSegment(sketch, "E1401", {"start": v(322.9, 137.14) * mm, "end": v(324.33, 135.07) * mm});
            skLineSegment(sketch, "E1402", {"start": v(324.33, 135.07) * mm, "end": v(325.83, 133.08) * mm});
            skLineSegment(sketch, "E1403", {"start": v(325.83, 133.08) * mm, "end": v(327.69, 131.12) * mm});
            skLineSegment(sketch, "E1404", {"start": v(327.69, 131.12) * mm, "end": v(330.22, 129.17) * mm});
            skLineSegment(sketch, "E1405", {"start": v(330.22, 129.17) * mm, "end": v(333.71, 127.18) * mm});
            skLineSegment(sketch, "E1406", {"start": v(333.71, 127.18) * mm, "end": v(334.85, 126.35) * mm});
            skLineSegment(sketch, "E1407", {"start": v(334.85, 126.35) * mm, "end": v(336.76, 124.72) * mm});
            skLineSegment(sketch, "E1408", {"start": v(336.76, 124.72) * mm, "end": v(339.14, 122.56) * mm});
            skLineSegment(sketch, "E1409", {"start": v(339.14, 122.56) * mm, "end": v(341.72, 120.15) * mm});
            skLineSegment(sketch, "E1410", {"start": v(341.72, 120.15) * mm, "end": v(344.22, 117.78) * mm});
            skLineSegment(sketch, "E1411", {"start": v(344.22, 117.78) * mm, "end": v(346.35, 115.72) * mm});
            skLineSegment(sketch, "E1412", {"start": v(346.35, 115.72) * mm, "end": v(347.84, 114.26) * mm});
            skLineSegment(sketch, "E1413", {"start": v(347.84, 114.26) * mm, "end": v(348.4, 113.67) * mm});
            skLineSegment(sketch, "E1414", {"start": v(300.52, 75.87) * mm, "end": v(300.5, 80.74) * mm});
            skLineSegment(sketch, "E1415", {"start": v(300.5, 80.74) * mm, "end": v(300.5, 85.63) * mm});
            skLineSegment(sketch, "E1416", {"start": v(300.5, 85.63) * mm, "end": v(300.5, 90.53) * mm});
            skLineSegment(sketch, "E1417", {"start": v(300.5, 90.53) * mm, "end": v(300.43, 95.42) * mm});
            skLineSegment(sketch, "E1418", {"start": v(300.43, 95.42) * mm, "end": v(300.25, 100.28) * mm});
            skLineSegment(sketch, "E1419", {"start": v(300.25, 100.28) * mm, "end": v(299.91, 105.1) * mm});
            skLineSegment(sketch, "E1420", {"start": v(299.91, 105.1) * mm, "end": v(299.36, 109.87) * mm});
            skLineSegment(sketch, "E1421", {"start": v(299.36, 109.87) * mm, "end": v(298.56, 114.57) * mm});
            skLineSegment(sketch, "E1422", {"start": v(298.56, 114.57) * mm, "end": v(298.44, 115.49) * mm});
            skLineSegment(sketch, "E1423", {"start": v(298.44, 115.49) * mm, "end": v(298.5, 116.04) * mm});
            skLineSegment(sketch, "E1424", {"start": v(298.5, 116.04) * mm, "end": v(298.64, 116.36) * mm});
            skLineSegment(sketch, "E1425", {"start": v(298.64, 116.36) * mm, "end": v(298.73, 116.61) * mm});
            skLineSegment(sketch, "E1426", {"start": v(298.73, 116.61) * mm, "end": v(298.68, 116.94) * mm});
            skLineSegment(sketch, "E1427", {"start": v(298.68, 116.94) * mm, "end": v(298.38, 117.5) * mm});
            skLineSegment(sketch, "E1428", {"start": v(298.38, 117.5) * mm, "end": v(297.72, 118.43) * mm});
            skLineSegment(sketch, "E1429", {"start": v(297.72, 118.43) * mm, "end": v(296.6, 119.89) * mm});
            skLineSegment(sketch, "E1430", {"start": v(298.4, 117.46) * mm, "end": v(301.73, 117.7) * mm});
            skLineSegment(sketch, "E1431", {"start": v(301.73, 117.7) * mm, "end": v(307.8, 117.63) * mm});
            skLineSegment(sketch, "E1432", {"start": v(307.8, 117.63) * mm, "end": v(315.7, 117.33) * mm});
            skLineSegment(sketch, "E1433", {"start": v(315.7, 117.33) * mm, "end": v(324.54, 116.86) * mm});
            skLineSegment(sketch, "E1434", {"start": v(324.54, 116.86) * mm, "end": v(333.4, 116.3) * mm});
            skLineSegment(sketch, "E1435", {"start": v(333.4, 116.3) * mm, "end": v(341.38, 115.7) * mm});
            skLineSegment(sketch, "E1436", {"start": v(341.38, 115.7) * mm, "end": v(347.58, 115.12) * mm});
            skLineSegment(sketch, "E1437", {"start": v(347.58, 115.12) * mm, "end": v(351.1, 114.65) * mm});
            skLineSegment(sketch, "E1438", {"start": v(351.1, 114.65) * mm, "end": v(351.25, 115.88) * mm});
            skLineSegment(sketch, "E1439", {"start": v(351.25, 115.88) * mm, "end": v(351.18, 117.55) * mm});
            skLineSegment(sketch, "E1440", {"start": v(351.18, 117.55) * mm, "end": v(350.94, 119.5) * mm});
            skLineSegment(sketch, "E1441", {"start": v(350.94, 119.5) * mm, "end": v(350.55, 121.56) * mm});
            skLineSegment(sketch, "E1442", {"start": v(350.55, 121.56) * mm, "end": v(350.05, 123.56) * mm});
            skLineSegment(sketch, "E1443", {"start": v(350.05, 123.56) * mm, "end": v(349.48, 125.35) * mm});
            skLineSegment(sketch, "E1444", {"start": v(349.48, 125.35) * mm, "end": v(348.87, 126.76) * mm});
            skLineSegment(sketch, "E1445", {"start": v(348.87, 126.76) * mm, "end": v(348.26, 127.62) * mm});
            skLineSegment(sketch, "E1446", {"start": v(300.52, 75.87) * mm, "end": v(303.1, 76.99) * mm});
            skLineSegment(sketch, "E1447", {"start": v(303.1, 76.99) * mm, "end": v(306.33, 77.68) * mm});
            skLineSegment(sketch, "E1448", {"start": v(306.33, 77.68) * mm, "end": v(310.08, 78.09) * mm});
            skLineSegment(sketch, "E1449", {"start": v(310.08, 78.09) * mm, "end": v(314.24, 78.38) * mm});
            skLineSegment(sketch, "E1450", {"start": v(314.24, 78.38) * mm, "end": v(318.68, 78.7) * mm});
            skLineSegment(sketch, "E1451", {"start": v(318.68, 78.7) * mm, "end": v(323.28, 79.2) * mm});
            skLineSegment(sketch, "E1452", {"start": v(323.28, 79.2) * mm, "end": v(327.9, 80.04) * mm});
            skLineSegment(sketch, "E1453", {"start": v(327.9, 80.04) * mm, "end": v(332.43, 81.37) * mm});
            skLineSegment(sketch, "E1454", {"start": v(332.43, 81.37) * mm, "end": v(334.28, 82.08) * mm});
            skLineSegment(sketch, "E1455", {"start": v(334.28, 82.08) * mm, "end": v(337.16, 83.17) * mm});
            skLineSegment(sketch, "E1456", {"start": v(337.16, 83.17) * mm, "end": v(340.68, 84.46) * mm});
            skLineSegment(sketch, "E1457", {"start": v(340.68, 84.46) * mm, "end": v(344.44, 85.75) * mm});
            skLineSegment(sketch, "E1458", {"start": v(344.44, 85.75) * mm, "end": v(348.05, 86.83) * mm});
            skLineSegment(sketch, "E1459", {"start": v(348.05, 86.83) * mm, "end": v(351.11, 87.52) * mm});
            skLineSegment(sketch, "E1460", {"start": v(351.11, 87.52) * mm, "end": v(353.24, 87.6) * mm});
            skLineSegment(sketch, "E1461", {"start": v(353.24, 87.6) * mm, "end": v(354.04, 86.9) * mm});
            skLineSegment(sketch, "E1462", {"start": v(354.04, 86.9) * mm, "end": v(354.07, 85.6) * mm});
            skLineSegment(sketch, "E1463", {"start": v(354.07, 85.6) * mm, "end": v(354.16, 84.03) * mm});
            skLineSegment(sketch, "E1464", {"start": v(354.16, 84.03) * mm, "end": v(354.3, 82.26) * mm});
            skLineSegment(sketch, "E1465", {"start": v(354.3, 82.26) * mm, "end": v(354.51, 80.42) * mm});
            skLineSegment(sketch, "E1466", {"start": v(354.51, 80.42) * mm, "end": v(354.78, 78.61) * mm});
            skLineSegment(sketch, "E1467", {"start": v(354.78, 78.61) * mm, "end": v(355.1, 76.94) * mm});
            skLineSegment(sketch, "E1468", {"start": v(355.1, 76.94) * mm, "end": v(355.48, 75.52) * mm});
            skLineSegment(sketch, "E1469", {"start": v(355.48, 75.52) * mm, "end": v(355.92, 74.45) * mm});
            skLineSegment(sketch, "E1470", {"start": v(-413.94, -20.27) * mm, "end": v(-414.13, -18.43) * mm});
            skLineSegment(sketch, "E1471", {"start": v(-414.13, -18.43) * mm, "end": v(-414.68, -16.67) * mm});
            skLineSegment(sketch, "E1472", {"start": v(-414.68, -16.67) * mm, "end": v(-415.57, -15.05) * mm});
            skLineSegment(sketch, "E1473", {"start": v(-415.57, -15.05) * mm, "end": v(-416.76, -13.62) * mm});
            skLineSegment(sketch, "E1474", {"start": v(-416.76, -13.62) * mm, "end": v(-418.22, -12.45) * mm});
            skLineSegment(sketch, "E1475", {"start": v(-418.22, -12.45) * mm, "end": v(-419.89, -11.59) * mm});
            skLineSegment(sketch, "E1476", {"start": v(-419.89, -11.59) * mm, "end": v(-421.7, -11.05) * mm});
            skLineSegment(sketch, "E1477", {"start": v(-421.7, -11.05) * mm, "end": v(-423.57, -10.87) * mm});
            skLineSegment(sketch, "E1478", {"start": v(-423.57, -10.87) * mm, "end": v(-425.45, -11.05) * mm});
            skLineSegment(sketch, "E1479", {"start": v(-425.45, -11.05) * mm, "end": v(-427.26, -11.59) * mm});
            skLineSegment(sketch, "E1480", {"start": v(-427.26, -11.59) * mm, "end": v(-428.92, -12.45) * mm});
            skLineSegment(sketch, "E1481", {"start": v(-428.92, -12.45) * mm, "end": v(-430.38, -13.62) * mm});
            skLineSegment(sketch, "E1482", {"start": v(-430.38, -13.62) * mm, "end": v(-431.58, -15.05) * mm});
            skLineSegment(sketch, "E1483", {"start": v(-431.58, -15.05) * mm, "end": v(-432.47, -16.67) * mm});
            skLineSegment(sketch, "E1484", {"start": v(-432.47, -16.67) * mm, "end": v(-433.02, -18.43) * mm});
            skLineSegment(sketch, "E1485", {"start": v(-433.02, -18.43) * mm, "end": v(-433.2, -20.27) * mm});
            skLineSegment(sketch, "E1486", {"start": v(-433.2, -20.27) * mm, "end": v(-433.02, -22.1) * mm});
            skLineSegment(sketch, "E1487", {"start": v(-433.02, -22.1) * mm, "end": v(-432.47, -23.86) * mm});
            skLineSegment(sketch, "E1488", {"start": v(-432.47, -23.86) * mm, "end": v(-431.58, -25.49) * mm});
            skLineSegment(sketch, "E1489", {"start": v(-431.58, -25.49) * mm, "end": v(-430.38, -26.91) * mm});
            skLineSegment(sketch, "E1490", {"start": v(-430.38, -26.91) * mm, "end": v(-428.92, -28.08) * mm});
            skLineSegment(sketch, "E1491", {"start": v(-428.92, -28.08) * mm, "end": v(-427.26, -28.95) * mm});
            skLineSegment(sketch, "E1492", {"start": v(-427.26, -28.95) * mm, "end": v(-425.45, -29.48) * mm});
            skLineSegment(sketch, "E1493", {"start": v(-425.45, -29.48) * mm, "end": v(-423.57, -29.66) * mm});
            skLineSegment(sketch, "E1494", {"start": v(-423.57, -29.66) * mm, "end": v(-421.7, -29.48) * mm});
            skLineSegment(sketch, "E1495", {"start": v(-421.7, -29.48) * mm, "end": v(-419.89, -28.95) * mm});
            skLineSegment(sketch, "E1496", {"start": v(-419.89, -28.95) * mm, "end": v(-418.22, -28.08) * mm});
            skLineSegment(sketch, "E1497", {"start": v(-418.22, -28.08) * mm, "end": v(-416.76, -26.91) * mm});
            skLineSegment(sketch, "E1498", {"start": v(-416.76, -26.91) * mm, "end": v(-415.57, -25.49) * mm});
            skLineSegment(sketch, "E1499", {"start": v(-415.57, -25.49) * mm, "end": v(-414.68, -23.86) * mm});
            skLineSegment(sketch, "E1500", {"start": v(-414.68, -23.86) * mm, "end": v(-414.13, -22.1) * mm});
            skLineSegment(sketch, "E1501", {"start": v(-414.13, -22.1) * mm, "end": v(-413.94, -20.27) * mm});
            skLineSegment(sketch, "E1502", {"start": v(-373.8, -50) * mm, "end": v(-374.01, -47.89) * mm});
            skLineSegment(sketch, "E1503", {"start": v(-374.01, -47.89) * mm, "end": v(-374.64, -45.86) * mm});
            skLineSegment(sketch, "E1504", {"start": v(-374.64, -45.86) * mm, "end": v(-375.66, -44) * mm});
            skLineSegment(sketch, "E1505", {"start": v(-375.66, -44) * mm, "end": v(-377.03, -42.36) * mm});
            skLineSegment(sketch, "E1506", {"start": v(-377.03, -42.36) * mm, "end": v(-378.7, -41.01) * mm});
            skLineSegment(sketch, "E1507", {"start": v(-378.7, -41.01) * mm, "end": v(-380.62, -40.01) * mm});
            skLineSegment(sketch, "E1508", {"start": v(-380.62, -40.01) * mm, "end": v(-382.69, -39.4) * mm});
            skLineSegment(sketch, "E1509", {"start": v(-382.69, -39.4) * mm, "end": v(-384.84, -39.2) * mm});
            skLineSegment(sketch, "E1510", {"start": v(-384.84, -39.2) * mm, "end": v(-387, -39.4) * mm});
            skLineSegment(sketch, "E1511", {"start": v(-387, -39.4) * mm, "end": v(-389.07, -40.01) * mm});
            skLineSegment(sketch, "E1512", {"start": v(-389.07, -40.01) * mm, "end": v(-390.98, -41.01) * mm});
            skLineSegment(sketch, "E1513", {"start": v(-390.98, -41.01) * mm, "end": v(-392.65, -42.36) * mm});
            skLineSegment(sketch, "E1514", {"start": v(-392.65, -42.36) * mm, "end": v(-394.02, -44) * mm});
            skLineSegment(sketch, "E1515", {"start": v(-394.02, -44) * mm, "end": v(-395.04, -45.86) * mm});
            skLineSegment(sketch, "E1516", {"start": v(-395.04, -45.86) * mm, "end": v(-395.67, -47.89) * mm});
            skLineSegment(sketch, "E1517", {"start": v(-395.67, -47.89) * mm, "end": v(-395.88, -50) * mm});
            skLineSegment(sketch, "E1518", {"start": v(-395.88, -50) * mm, "end": v(-395.67, -52.1) * mm});
            skLineSegment(sketch, "E1519", {"start": v(-395.67, -52.1) * mm, "end": v(-395.04, -54.13) * mm});
            skLineSegment(sketch, "E1520", {"start": v(-395.04, -54.13) * mm, "end": v(-394.02, -56) * mm});
            skLineSegment(sketch, "E1521", {"start": v(-394.02, -56) * mm, "end": v(-392.65, -57.64) * mm});
            skLineSegment(sketch, "E1522", {"start": v(-392.65, -57.64) * mm, "end": v(-390.98, -58.98) * mm});
            skLineSegment(sketch, "E1523", {"start": v(-390.98, -58.98) * mm, "end": v(-389.07, -59.98) * mm});
            skLineSegment(sketch, "E1524", {"start": v(-389.07, -59.98) * mm, "end": v(-387, -60.6) * mm});
            skLineSegment(sketch, "E1525", {"start": v(-387, -60.6) * mm, "end": v(-384.84, -60.8) * mm});
            skLineSegment(sketch, "E1526", {"start": v(-384.84, -60.8) * mm, "end": v(-382.69, -60.6) * mm});
            skLineSegment(sketch, "E1527", {"start": v(-382.69, -60.6) * mm, "end": v(-380.62, -59.98) * mm});
            skLineSegment(sketch, "E1528", {"start": v(-380.62, -59.98) * mm, "end": v(-378.7, -58.98) * mm});
            skLineSegment(sketch, "E1529", {"start": v(-378.7, -58.98) * mm, "end": v(-377.03, -57.64) * mm});
            skLineSegment(sketch, "E1530", {"start": v(-377.03, -57.64) * mm, "end": v(-375.66, -56) * mm});
            skLineSegment(sketch, "E1531", {"start": v(-375.66, -56) * mm, "end": v(-374.64, -54.13) * mm});
            skLineSegment(sketch, "E1532", {"start": v(-374.64, -54.13) * mm, "end": v(-374.01, -52.1) * mm});
            skLineSegment(sketch, "E1533", {"start": v(-374.01, -52.1) * mm, "end": v(-373.8, -50) * mm});
            skLineSegment(sketch, "E1534", {"start": v(-329.5, -43.87) * mm, "end": v(-331.56, -44.09) * mm});
            skLineSegment(sketch, "E1535", {"start": v(-331.56, -44.09) * mm, "end": v(-333.54, -44.73) * mm});
            skLineSegment(sketch, "E1536", {"start": v(-333.54, -44.73) * mm, "end": v(-335.37, -45.77) * mm});
            skLineSegment(sketch, "E1537", {"start": v(-335.37, -45.77) * mm, "end": v(-336.97, -47.17) * mm});
            skLineSegment(sketch, "E1538", {"start": v(-336.97, -47.17) * mm, "end": v(-338.29, -48.88) * mm});
            skLineSegment(sketch, "E1539", {"start": v(-338.29, -48.88) * mm, "end": v(-339.26, -50.83) * mm});
            skLineSegment(sketch, "E1540", {"start": v(-339.26, -50.83) * mm, "end": v(-339.86, -52.95) * mm});
            skLineSegment(sketch, "E1541", {"start": v(-339.86, -52.95) * mm, "end": v(-340.07, -55.15) * mm});
            skLineSegment(sketch, "E1542", {"start": v(-340.07, -55.15) * mm, "end": v(-339.86, -57.35) * mm});
            skLineSegment(sketch, "E1543", {"start": v(-339.86, -57.35) * mm, "end": v(-339.26, -59.46) * mm});
            skLineSegment(sketch, "E1544", {"start": v(-339.26, -59.46) * mm, "end": v(-338.29, -61.41) * mm});
            skLineSegment(sketch, "E1545", {"start": v(-338.29, -61.41) * mm, "end": v(-336.97, -63.12) * mm});
            skLineSegment(sketch, "E1546", {"start": v(-336.97, -63.12) * mm, "end": v(-335.37, -64.52) * mm});
            skLineSegment(sketch, "E1547", {"start": v(-335.37, -64.52) * mm, "end": v(-333.54, -65.56) * mm});
            skLineSegment(sketch, "E1548", {"start": v(-333.54, -65.56) * mm, "end": v(-331.56, -66.2) * mm});
            skLineSegment(sketch, "E1549", {"start": v(-331.56, -66.2) * mm, "end": v(-329.5, -66.42) * mm});
            skLineSegment(sketch, "E1550", {"start": v(-329.5, -66.42) * mm, "end": v(-327.43, -66.2) * mm});
            skLineSegment(sketch, "E1551", {"start": v(-327.43, -66.2) * mm, "end": v(-325.45, -65.56) * mm});
            skLineSegment(sketch, "E1552", {"start": v(-325.45, -65.56) * mm, "end": v(-323.62, -64.52) * mm});
            skLineSegment(sketch, "E1553", {"start": v(-323.62, -64.52) * mm, "end": v(-322.02, -63.12) * mm});
            skLineSegment(sketch, "E1554", {"start": v(-322.02, -63.12) * mm, "end": v(-320.7, -61.41) * mm});
            skLineSegment(sketch, "E1555", {"start": v(-320.7, -61.41) * mm, "end": v(-319.73, -59.46) * mm});
            skLineSegment(sketch, "E1556", {"start": v(-319.73, -59.46) * mm, "end": v(-319.13, -57.35) * mm});
            skLineSegment(sketch, "E1557", {"start": v(-319.13, -57.35) * mm, "end": v(-318.92, -55.15) * mm});
            skLineSegment(sketch, "E1558", {"start": v(-318.92, -55.15) * mm, "end": v(-319.13, -52.95) * mm});
            skLineSegment(sketch, "E1559", {"start": v(-319.13, -52.95) * mm, "end": v(-319.73, -50.83) * mm});
            skLineSegment(sketch, "E1560", {"start": v(-319.73, -50.83) * mm, "end": v(-320.7, -48.88) * mm});
            skLineSegment(sketch, "E1561", {"start": v(-320.7, -48.88) * mm, "end": v(-322.02, -47.17) * mm});
            skLineSegment(sketch, "E1562", {"start": v(-322.02, -47.17) * mm, "end": v(-323.62, -45.77) * mm});
            skLineSegment(sketch, "E1563", {"start": v(-323.62, -45.77) * mm, "end": v(-325.45, -44.73) * mm});
            skLineSegment(sketch, "E1564", {"start": v(-325.45, -44.73) * mm, "end": v(-327.43, -44.09) * mm});
            skLineSegment(sketch, "E1565", {"start": v(-327.43, -44.09) * mm, "end": v(-329.5, -43.87) * mm});
            skSolve(sketch);
        }
        {
            var Q0;
            Q0 = qSketchRegion(id + "F0", true);
            extrude(context, id + "F1", {"entities" : qUnion([Q0]), "depth" : 76.2 * mm, "offsetDistance" : 25.4 * mm});
        }
    });
